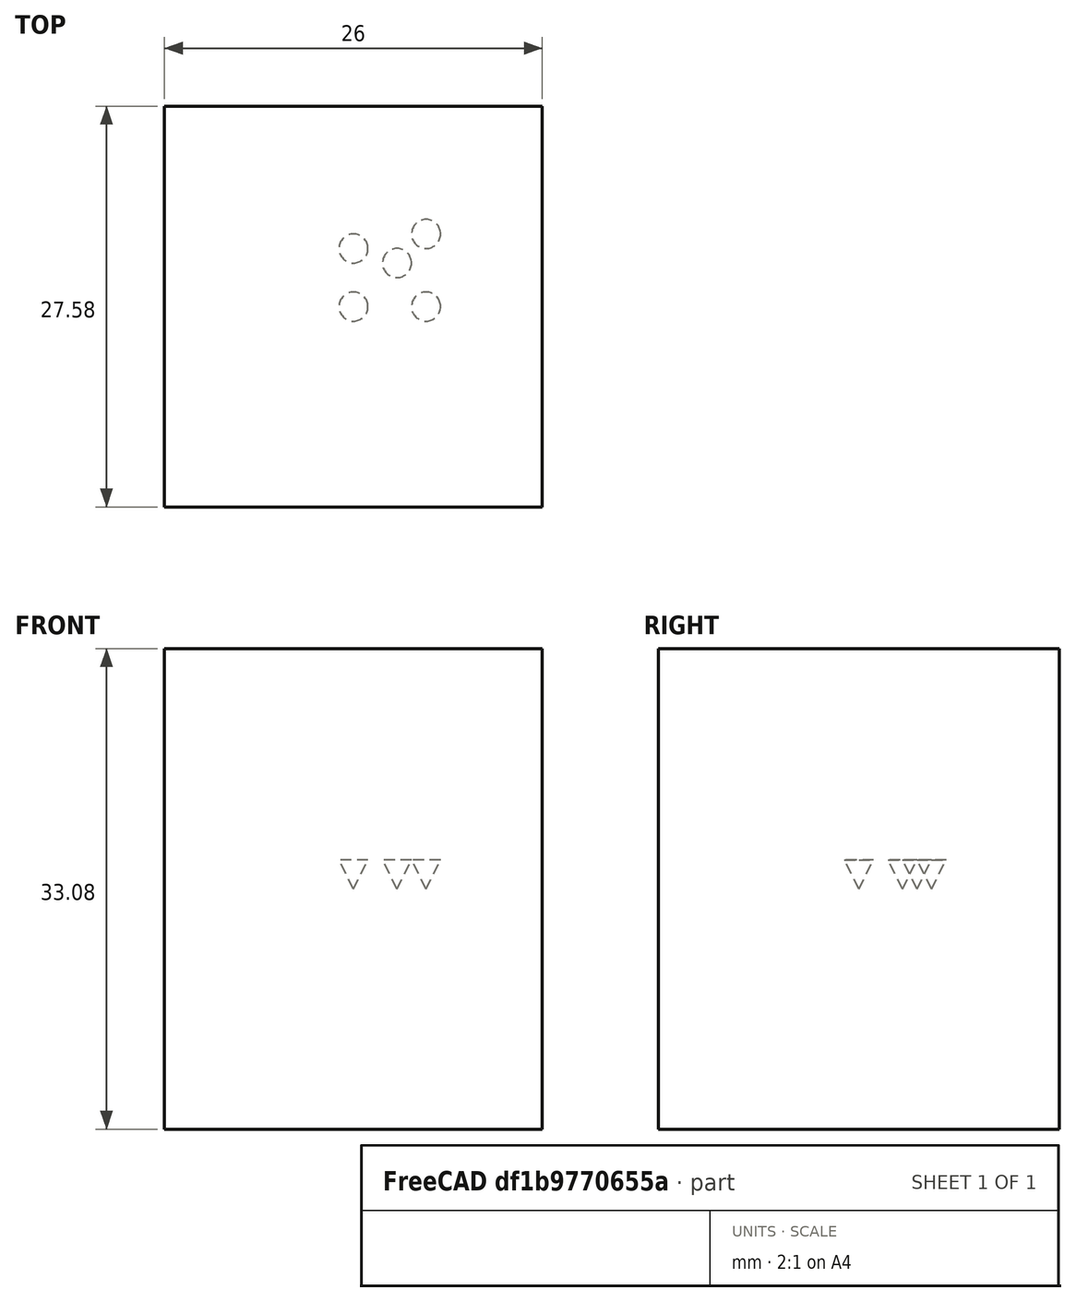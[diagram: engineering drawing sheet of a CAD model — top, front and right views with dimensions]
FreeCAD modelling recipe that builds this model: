
FCSTD DOCUMENT  (FreeCAD 0.21R33694 (Git))
Label: PointArray
License: All rights reserved
objects: App::DocumentObjectGroupPython×1251, Part::Vertex×5, Part::FeaturePython×2, App::Part×2, Part::Cone×1, Part::Compound×1
note: 9 computed .brp shape members not serialized (recipe doc carries the construction recipe); baked Part::Feature solids carry a one-line shape summary decoded from their .brp

FEATURE [App::DocumentObjectGroupPython] HALFPI  # scripted group (container) (typed FeaturePython)
  name = HALFPI
  value = pi/2.
FEATURE [App::DocumentObjectGroupPython] PI  # scripted group (container) (typed FeaturePython)
  name = PI
  value = 1.*pi
FEATURE [App::DocumentObjectGroupPython] TWOPI  # scripted group (container) (typed FeaturePython)
  name = TWOPI
  value = 2.*pi
FEATURE [App::DocumentObjectGroupPython] Constants  # scripted group (container) (typed FeaturePython)
  Group = -> [HALFPI,PI,TWOPI]
FEATURE [App::DocumentObjectGroupPython] Variables  # scripted group (container) (typed FeaturePython)
FEATURE [App::DocumentObjectGroupPython] Quantities  # scripted group (container) (typed FeaturePython)
FEATURE [App::DocumentObjectGroupPython] Isotopes  # scripted group (container) (typed FeaturePython)
FEATURE [App::DocumentObjectGroupPython] Elements  # scripted group (container) (typed FeaturePython)
FEATURE [App::DocumentObjectGroupPython] Matrix  # scripted group (container) (typed FeaturePython)
FEATURE [App::DocumentObjectGroupPython] Surfaces  # scripted group (container) (typed FeaturePython)
FEATURE [App::DocumentObjectGroupPython] Opticals  # scripted group (container) (typed FeaturePython)
  Group = -> [Matrix,Surfaces]
FEATURE [App::DocumentObjectGroupPython] G4Isotopes  # scripted group (container) (typed FeaturePython)
FEATURE [App::DocumentObjectGroupPython] H_element  # scripted group (container) (typed FeaturePython)
  Z = 1
  atom_value = 1.008
  formula = H
  name = H_element
FEATURE [App::DocumentObjectGroupPython] He_element  # scripted group (container) (typed FeaturePython)
  Z = 2
  atom_value = 4.0026
  formula = He
  name = He_element
FEATURE [App::DocumentObjectGroupPython] Li_element  # scripted group (container) (typed FeaturePython)
  Z = 3
  atom_value = 6.94
  formula = Li
  name = Li_element
FEATURE [App::DocumentObjectGroupPython] Be_element  # scripted group (container) (typed FeaturePython)
  Z = 4
  atom_value = 9.01218
  formula = Be
  name = Be_element
FEATURE [App::DocumentObjectGroupPython] B_element  # scripted group (container) (typed FeaturePython)
  Z = 5
  atom_value = 10.81
  formula = B
  name = B_element
FEATURE [App::DocumentObjectGroupPython] C_element  # scripted group (container) (typed FeaturePython)
  Z = 6
  atom_value = 12.011
  formula = C
  name = C_element
FEATURE [App::DocumentObjectGroupPython] N_element  # scripted group (container) (typed FeaturePython)
  Z = 7
  atom_value = 14.007
  formula = N
  name = N_element
FEATURE [App::DocumentObjectGroupPython] O_element  # scripted group (container) (typed FeaturePython)
  Z = 8
  atom_value = 15.999
  formula = O
  name = O_element
FEATURE [App::DocumentObjectGroupPython] F_element  # scripted group (container) (typed FeaturePython)
  Z = 9
  atom_value = 18.9984
  formula = F
  name = F_element
FEATURE [App::DocumentObjectGroupPython] Ne_element  # scripted group (container) (typed FeaturePython)
  Z = 10
  atom_value = 20.1797
  formula = Ne
  name = Ne_element
FEATURE [App::DocumentObjectGroupPython] Na_element  # scripted group (container) (typed FeaturePython)
  Z = 11
  atom_value = 22.9898
  formula = Na
  name = Na_element
FEATURE [App::DocumentObjectGroupPython] Mg_element  # scripted group (container) (typed FeaturePython)
  Z = 12
  atom_value = 24.305
  formula = Mg
  name = Mg_element
FEATURE [App::DocumentObjectGroupPython] Al_element  # scripted group (container) (typed FeaturePython)
  Z = 13
  atom_value = 26.9815
  formula = Al
  name = Al_element
FEATURE [App::DocumentObjectGroupPython] Si_element  # scripted group (container) (typed FeaturePython)
  Z = 14
  atom_value = 28.085
  formula = Si
  name = Si_element
FEATURE [App::DocumentObjectGroupPython] P_element  # scripted group (container) (typed FeaturePython)
  Z = 15
  atom_value = 30.9738
  formula = P
  name = P_element
FEATURE [App::DocumentObjectGroupPython] S_element  # scripted group (container) (typed FeaturePython)
  Z = 16
  atom_value = 32.06
  formula = S
  name = S_element
FEATURE [App::DocumentObjectGroupPython] Cl_element  # scripted group (container) (typed FeaturePython)
  Z = 17
  atom_value = 35.45
  formula = Cl
  name = Cl_element
FEATURE [App::DocumentObjectGroupPython] Ar_element  # scripted group (container) (typed FeaturePython)
  Z = 18
  atom_value = 39.95
  formula = Ar
  name = Ar_element
FEATURE [App::DocumentObjectGroupPython] K_element  # scripted group (container) (typed FeaturePython)
  Z = 19
  atom_value = 39.0983
  formula = K
  name = K_element
FEATURE [App::DocumentObjectGroupPython] Ca_element  # scripted group (container) (typed FeaturePython)
  Z = 20
  atom_value = 40.078
  formula = Ca
  name = Ca_element
FEATURE [App::DocumentObjectGroupPython] Sc_element  # scripted group (container) (typed FeaturePython)
  Z = 21
  atom_value = 44.9559
  formula = Sc
  name = Sc_element
FEATURE [App::DocumentObjectGroupPython] Ti_element  # scripted group (container) (typed FeaturePython)
  Z = 22
  atom_value = 47.867
  formula = Ti
  name = Ti_element
FEATURE [App::DocumentObjectGroupPython] V_element  # scripted group (container) (typed FeaturePython)
  Z = 23
  atom_value = 50.9415
  formula = V
  name = V_element
FEATURE [App::DocumentObjectGroupPython] Cr_element  # scripted group (container) (typed FeaturePython)
  Z = 24
  atom_value = 51.9961
  formula = Cr
  name = Cr_element
FEATURE [App::DocumentObjectGroupPython] Mn_element  # scripted group (container) (typed FeaturePython)
  Z = 25
  atom_value = 54.938
  formula = Mn
  name = Mn_element
FEATURE [App::DocumentObjectGroupPython] Fe_element  # scripted group (container) (typed FeaturePython)
  Z = 26
  atom_value = 55.845
  formula = Fe
  name = Fe_element
FEATURE [App::DocumentObjectGroupPython] Co_element  # scripted group (container) (typed FeaturePython)
  Z = 27
  atom_value = 58.9332
  formula = Co
  name = Co_element
FEATURE [App::DocumentObjectGroupPython] Ni_element  # scripted group (container) (typed FeaturePython)
  Z = 28
  atom_value = 58.6934
  formula = Ni
  name = Ni_element
FEATURE [App::DocumentObjectGroupPython] Cu_element  # scripted group (container) (typed FeaturePython)
  Z = 29
  atom_value = 63.546
  formula = Cu
  name = Cu_element
FEATURE [App::DocumentObjectGroupPython] Zn_element  # scripted group (container) (typed FeaturePython)
  Z = 30
  atom_value = 65.38
  formula = Zn
  name = Zn_element
FEATURE [App::DocumentObjectGroupPython] Ga_element  # scripted group (container) (typed FeaturePython)
  Z = 31
  atom_value = 69.723
  formula = Ga
  name = Ga_element
FEATURE [App::DocumentObjectGroupPython] Ge_element  # scripted group (container) (typed FeaturePython)
  Z = 32
  atom_value = 72.63
  formula = Ge
  name = Ge_element
FEATURE [App::DocumentObjectGroupPython] As_element  # scripted group (container) (typed FeaturePython)
  Z = 33
  atom_value = 74.9216
  formula = As
  name = As_element
FEATURE [App::DocumentObjectGroupPython] Se_element  # scripted group (container) (typed FeaturePython)
  Z = 34
  atom_value = 78.971
  formula = Se
  name = Se_element
FEATURE [App::DocumentObjectGroupPython] Br_element  # scripted group (container) (typed FeaturePython)
  Z = 35
  atom_value = 79.904
  formula = Br
  name = Br_element
FEATURE [App::DocumentObjectGroupPython] Kr_element  # scripted group (container) (typed FeaturePython)
  Z = 36
  atom_value = 83.798
  formula = Kr
  name = Kr_element
FEATURE [App::DocumentObjectGroupPython] Rb_element  # scripted group (container) (typed FeaturePython)
  Z = 37
  atom_value = 85.4678
  formula = Rb
  name = Rb_element
FEATURE [App::DocumentObjectGroupPython] Sr_element  # scripted group (container) (typed FeaturePython)
  Z = 38
  atom_value = 87.62
  formula = Sr
  name = Sr_element
FEATURE [App::DocumentObjectGroupPython] Y_element  # scripted group (container) (typed FeaturePython)
  Z = 39
  atom_value = 88.9058
  formula = Y
  name = Y_element
FEATURE [App::DocumentObjectGroupPython] Zr_element  # scripted group (container) (typed FeaturePython)
  Z = 40
  atom_value = 91.224
  formula = Zr
  name = Zr_element
FEATURE [App::DocumentObjectGroupPython] Nb_element  # scripted group (container) (typed FeaturePython)
  Z = 41
  atom_value = 92.9064
  formula = Nb
  name = Nb_element
FEATURE [App::DocumentObjectGroupPython] Mo_element  # scripted group (container) (typed FeaturePython)
  Z = 42
  atom_value = 95.95
  formula = Mo
  name = Mo_element
FEATURE [App::DocumentObjectGroupPython] Tc_element  # scripted group (container) (typed FeaturePython)
  Z = 43
  atom_value = 97
  formula = Tc
  name = Tc_element
FEATURE [App::DocumentObjectGroupPython] Ru_element  # scripted group (container) (typed FeaturePython)
  Z = 44
  atom_value = 101.07
  formula = Ru
  name = Ru_element
FEATURE [App::DocumentObjectGroupPython] Rh_element  # scripted group (container) (typed FeaturePython)
  Z = 45
  atom_value = 102.905
  formula = Rh
  name = Rh_element
FEATURE [App::DocumentObjectGroupPython] Pd_element  # scripted group (container) (typed FeaturePython)
  Z = 46
  atom_value = 106.42
  formula = Pd
  name = Pd_element
FEATURE [App::DocumentObjectGroupPython] Ag_element  # scripted group (container) (typed FeaturePython)
  Z = 47
  atom_value = 107.868
  formula = Ag
  name = Ag_element
FEATURE [App::DocumentObjectGroupPython] Cd_element  # scripted group (container) (typed FeaturePython)
  Z = 48
  atom_value = 112.414
  formula = Cd
  name = Cd_element
FEATURE [App::DocumentObjectGroupPython] In_element  # scripted group (container) (typed FeaturePython)
  Z = 49
  atom_value = 114.818
  formula = In
  name = In_element
FEATURE [App::DocumentObjectGroupPython] Sn_element  # scripted group (container) (typed FeaturePython)
  Z = 50
  atom_value = 118.71
  formula = Sn
  name = Sn_element
FEATURE [App::DocumentObjectGroupPython] Sb_element  # scripted group (container) (typed FeaturePython)
  Z = 51
  atom_value = 121.76
  formula = Sb
  name = Sb_element
FEATURE [App::DocumentObjectGroupPython] Te_element  # scripted group (container) (typed FeaturePython)
  Z = 52
  atom_value = 127.6
  formula = Te
  name = Te_element
FEATURE [App::DocumentObjectGroupPython] I_element  # scripted group (container) (typed FeaturePython)
  Z = 53
  atom_value = 126.904
  formula = I
  name = I_element
FEATURE [App::DocumentObjectGroupPython] Xe_element  # scripted group (container) (typed FeaturePython)
  Z = 54
  atom_value = 131.293
  formula = Xe
  name = Xe_element
FEATURE [App::DocumentObjectGroupPython] Cs_element  # scripted group (container) (typed FeaturePython)
  Z = 55
  atom_value = 132.905
  formula = Cs
  name = Cs_element
FEATURE [App::DocumentObjectGroupPython] Ba_element  # scripted group (container) (typed FeaturePython)
  Z = 56
  atom_value = 137.327
  formula = Ba
  name = Ba_element
FEATURE [App::DocumentObjectGroupPython] La_element  # scripted group (container) (typed FeaturePython)
  Z = 57
  atom_value = 138.905
  formula = La
  name = La_element
FEATURE [App::DocumentObjectGroupPython] Ce_element  # scripted group (container) (typed FeaturePython)
  Z = 58
  atom_value = 140.116
  formula = Ce
  name = Ce_element
FEATURE [App::DocumentObjectGroupPython] Pr_element  # scripted group (container) (typed FeaturePython)
  Z = 59
  atom_value = 140.908
  formula = Pr
  name = Pr_element
FEATURE [App::DocumentObjectGroupPython] Nd_element  # scripted group (container) (typed FeaturePython)
  Z = 60
  atom_value = 144.242
  formula = Nd
  name = Nd_element
FEATURE [App::DocumentObjectGroupPython] Pm_element  # scripted group (container) (typed FeaturePython)
  Z = 61
  atom_value = 145
  formula = Pm
  name = Pm_element
FEATURE [App::DocumentObjectGroupPython] Sm_element  # scripted group (container) (typed FeaturePython)
  Z = 62
  atom_value = 150.36
  formula = Sm
  name = Sm_element
FEATURE [App::DocumentObjectGroupPython] Eu_element  # scripted group (container) (typed FeaturePython)
  Z = 63
  atom_value = 151.964
  formula = Eu
  name = Eu_element
FEATURE [App::DocumentObjectGroupPython] Gd_element  # scripted group (container) (typed FeaturePython)
  Z = 64
  atom_value = 157.25
  formula = Gd
  name = Gd_element
FEATURE [App::DocumentObjectGroupPython] Tb_element  # scripted group (container) (typed FeaturePython)
  Z = 65
  atom_value = 158.925
  formula = Tb
  name = Tb_element
FEATURE [App::DocumentObjectGroupPython] Dy_element  # scripted group (container) (typed FeaturePython)
  Z = 66
  atom_value = 162.5
  formula = Dy
  name = Dy_element
FEATURE [App::DocumentObjectGroupPython] Ho_element  # scripted group (container) (typed FeaturePython)
  Z = 67
  atom_value = 164.93
  formula = Ho
  name = Ho_element
FEATURE [App::DocumentObjectGroupPython] Er_element  # scripted group (container) (typed FeaturePython)
  Z = 68
  atom_value = 167.259
  formula = Er
  name = Er_element
FEATURE [App::DocumentObjectGroupPython] Tm_element  # scripted group (container) (typed FeaturePython)
  Z = 69
  atom_value = 168.934
  formula = Tm
  name = Tm_element
FEATURE [App::DocumentObjectGroupPython] Yb_element  # scripted group (container) (typed FeaturePython)
  Z = 70
  atom_value = 173.045
  formula = Yb
  name = Yb_element
FEATURE [App::DocumentObjectGroupPython] Lu_element  # scripted group (container) (typed FeaturePython)
  Z = 71
  atom_value = 174.967
  formula = Lu
  name = Lu_element
FEATURE [App::DocumentObjectGroupPython] Hf_element  # scripted group (container) (typed FeaturePython)
  Z = 72
  atom_value = 178.49
  formula = Hf
  name = Hf_element
FEATURE [App::DocumentObjectGroupPython] Ta_element  # scripted group (container) (typed FeaturePython)
  Z = 73
  atom_value = 180.948
  formula = Ta
  name = Ta_element
FEATURE [App::DocumentObjectGroupPython] W_element  # scripted group (container) (typed FeaturePython)
  Z = 74
  atom_value = 183.84
  formula = W
  name = W_element
FEATURE [App::DocumentObjectGroupPython] Re_element  # scripted group (container) (typed FeaturePython)
  Z = 75
  atom_value = 186.207
  formula = Re
  name = Re_element
FEATURE [App::DocumentObjectGroupPython] Os_element  # scripted group (container) (typed FeaturePython)
  Z = 76
  atom_value = 190.23
  formula = Os
  name = Os_element
FEATURE [App::DocumentObjectGroupPython] Ir_element  # scripted group (container) (typed FeaturePython)
  Z = 77
  atom_value = 192.217
  formula = Ir
  name = Ir_element
FEATURE [App::DocumentObjectGroupPython] Pt_element  # scripted group (container) (typed FeaturePython)
  Z = 78
  atom_value = 195.084
  formula = Pt
  name = Pt_element
FEATURE [App::DocumentObjectGroupPython] Au_element  # scripted group (container) (typed FeaturePython)
  Z = 79
  atom_value = 196.967
  formula = Au
  name = Au_element
FEATURE [App::DocumentObjectGroupPython] Hg_element  # scripted group (container) (typed FeaturePython)
  Z = 80
  atom_value = 200.592
  formula = Hg
  name = Hg_element
FEATURE [App::DocumentObjectGroupPython] Tl_element  # scripted group (container) (typed FeaturePython)
  Z = 81
  atom_value = 204.38
  formula = Tl
  name = Tl_element
FEATURE [App::DocumentObjectGroupPython] Pb_element  # scripted group (container) (typed FeaturePython)
  Z = 82
  atom_value = 207.2
  formula = Pb
  name = Pb_element
FEATURE [App::DocumentObjectGroupPython] Bi_element  # scripted group (container) (typed FeaturePython)
  Z = 83
  atom_value = 208.98
  formula = Bi
  name = Bi_element
FEATURE [App::DocumentObjectGroupPython] Po_element  # scripted group (container) (typed FeaturePython)
  Z = 84
  atom_value = 209
  formula = Po
  name = Po_element
FEATURE [App::DocumentObjectGroupPython] At_element  # scripted group (container) (typed FeaturePython)
  Z = 85
  atom_value = 210
  formula = At
  name = At_element
FEATURE [App::DocumentObjectGroupPython] Rn_element  # scripted group (container) (typed FeaturePython)
  Z = 86
  atom_value = 222
  formula = Rn
  name = Rn_element
FEATURE [App::DocumentObjectGroupPython] Fr_element  # scripted group (container) (typed FeaturePython)
  Z = 87
  atom_value = 223
  formula = Fr
  name = Fr_element
FEATURE [App::DocumentObjectGroupPython] Ra_element  # scripted group (container) (typed FeaturePython)
  Z = 88
  atom_value = 226
  formula = Ra
  name = Ra_element
FEATURE [App::DocumentObjectGroupPython] Ac_element  # scripted group (container) (typed FeaturePython)
  Z = 89
  atom_value = 227
  formula = Ac
  name = Ac_element
FEATURE [App::DocumentObjectGroupPython] Th_element  # scripted group (container) (typed FeaturePython)
  Z = 90
  atom_value = 232.038
  formula = Th
  name = Th_element
FEATURE [App::DocumentObjectGroupPython] Pa_element  # scripted group (container) (typed FeaturePython)
  Z = 91
  atom_value = 231.036
  formula = Pa
  name = Pa_element
FEATURE [App::DocumentObjectGroupPython] U_element  # scripted group (container) (typed FeaturePython)
  Z = 92
  atom_value = 238.029
  formula = U
  name = U_element
FEATURE [App::DocumentObjectGroupPython] Np_element  # scripted group (container) (typed FeaturePython)
  Z = 93
  atom_value = 237
  formula = Np
  name = Np_element
FEATURE [App::DocumentObjectGroupPython] Pu_element  # scripted group (container) (typed FeaturePython)
  Z = 94
  atom_value = 244
  formula = Pu
  name = Pu_element
FEATURE [App::DocumentObjectGroupPython] Am_element  # scripted group (container) (typed FeaturePython)
  Z = 95
  atom_value = 243
  formula = Am
  name = Am_element
FEATURE [App::DocumentObjectGroupPython] Cm_element  # scripted group (container) (typed FeaturePython)
  Z = 96
  atom_value = 247
  formula = Cm
  name = Cm_element
FEATURE [App::DocumentObjectGroupPython] Bk_element  # scripted group (container) (typed FeaturePython)
  Z = 97
  atom_value = 247
  formula = Bk
  name = Bk_element
FEATURE [App::DocumentObjectGroupPython] Cf_element  # scripted group (container) (typed FeaturePython)
  Z = 98
  atom_value = 251
  formula = Cf
  name = Cf_element
FEATURE [App::DocumentObjectGroupPython] G4Elements  # scripted group (container) (typed FeaturePython)
  Group = -> [H_element,He_element,Li_element,Be_element,B_element,C_element,N_element,O_element,F_element,Ne_element,Na_element,Mg_element,Al_element,Si_element,P_element,S_element,Cl_element,Ar_element,K_element,Ca_element,Sc_element,Ti_element,V_element,Cr_element,Mn_element,Fe_element,Co_element,Ni_element,Cu_element,Zn_element,Ga_element,Ge_element,As_element,Se_element,Br_element,Kr_element,Rb_element,+61 more]
FEATURE [App::DocumentObjectGroupPython] H_element001  label="H_element : 0.101"  # scripted group (container) (typed FeaturePython)
  n = 0.101327
FEATURE [App::DocumentObjectGroupPython] C_element001  label="C_element : 0.775"  # scripted group (container) (typed FeaturePython)
  n = 0.7755
FEATURE [App::DocumentObjectGroupPython] N_element001  label="N_element : 0.035"  # scripted group (container) (typed FeaturePython)
  n = 0.035057
FEATURE [App::DocumentObjectGroupPython] O_element001  label="O_element : 0.052"  # scripted group (container) (typed FeaturePython)
  n = 0.0523159
FEATURE [App::DocumentObjectGroupPython] F_element001  label="F_element : 0.017"  # scripted group (container) (typed FeaturePython)
  n = 0.017422
FEATURE [App::DocumentObjectGroupPython] Ca_element001  label="Ca_element : 0.018"  # scripted group (container) (typed FeaturePython)
  n = 0.018378
FEATURE [App::DocumentObjectGroupPython] G4_A_150_TISSUE  label="G4_A-150_TISSUE"  # scripted group (container) (typed FeaturePython)
  Dunit = g/cm3
  Dvalue = 1.127
  Group = -> [H_element001,C_element001,N_element001,O_element001,F_element001,Ca_element001]
  conduct = 2
  density = 1
  expand = 3
  formula = G4_A-150_TISSUE
  name = G4_A-150_TISSUE
  specific = 4
FEATURE [App::DocumentObjectGroupPython] C_element002  label="C_element : 3"  # scripted group (container) (typed FeaturePython)
  n = 3
  ref = C_element
FEATURE [App::DocumentObjectGroupPython] H_element002  label="H_element : 6"  # scripted group (container) (typed FeaturePython)
  n = 6
  ref = H_element
FEATURE [App::DocumentObjectGroupPython] O_element002  label="O_element : 1"  # scripted group (container) (typed FeaturePython)
  n = 1
  ref = O_element
FEATURE [App::DocumentObjectGroupPython] G4_ACETONE  # scripted group (container) (typed FeaturePython)
  Dunit = g/cm3
  Dvalue = 0.7899
  Group = -> [C_element002,H_element002,O_element002]
  conduct = 2
  density = 1
  expand = 3
  formula = G4_ACETONE
  name = G4_ACETONE
  specific = 4
FEATURE [App::DocumentObjectGroupPython] C_element003  label="C_element : 2"  # scripted group (container) (typed FeaturePython)
  n = 2
  ref = C_element
FEATURE [App::DocumentObjectGroupPython] H_element003  label="H_element : 2"  # scripted group (container) (typed FeaturePython)
  n = 2
  ref = H_element
FEATURE [App::DocumentObjectGroupPython] G4_ACETYLENE  # scripted group (container) (typed FeaturePython)
  Dunit = g/cm3
  Dvalue = 0.0010967
  Group = -> [C_element003,H_element003]
  conduct = 2
  density = 1
  expand = 3
  formula = G4_ACETYLENE
  name = G4_ACETYLENE
  specific = 4
FEATURE [App::DocumentObjectGroupPython] C_element004  label="C_element : 5"  # scripted group (container) (typed FeaturePython)
  n = 5
  ref = C_element
FEATURE [App::DocumentObjectGroupPython] H_element004  label="H_element : 5"  # scripted group (container) (typed FeaturePython)
  n = 5
  ref = H_element
FEATURE [App::DocumentObjectGroupPython] N_element002  label="N_element : 5"  # scripted group (container) (typed FeaturePython)
  n = 5
  ref = N_element
FEATURE [App::DocumentObjectGroupPython] G4_ADENINE  # scripted group (container) (typed FeaturePython)
  Dunit = g/cm3
  Dvalue = 1.6
  Group = -> [C_element004,H_element004,N_element002]
  conduct = 2
  density = 1
  expand = 3
  formula = G4_ADENINE
  name = G4_ADENINE
  specific = 4
FEATURE [App::DocumentObjectGroupPython] H_element005  label="H_element : 0.114"  # scripted group (container) (typed FeaturePython)
  n = 0.114
FEATURE [App::DocumentObjectGroupPython] C_element005  label="C_element : 0.598"  # scripted group (container) (typed FeaturePython)
  n = 0.598
FEATURE [App::DocumentObjectGroupPython] N_element003  label="N_element : 0.007"  # scripted group (container) (typed FeaturePython)
  n = 0.007
FEATURE [App::DocumentObjectGroupPython] O_element003  label="O_element : 0.278"  # scripted group (container) (typed FeaturePython)
  n = 0.278
FEATURE [App::DocumentObjectGroupPython] Na_element001  label="Na_element : 0.001"  # scripted group (container) (typed FeaturePython)
  n = 0.001
FEATURE [App::DocumentObjectGroupPython] S_element001  label="S_element : 0.001"  # scripted group (container) (typed FeaturePython)
  n = 0.001
FEATURE [App::DocumentObjectGroupPython] Cl_element001  label="Cl_element : 0.001"  # scripted group (container) (typed FeaturePython)
  n = 0.001
FEATURE [App::DocumentObjectGroupPython] G4_ADIPOSE_TISSUE_ICRP  # scripted group (container) (typed FeaturePython)
  Dunit = g/cm3
  Dvalue = 0.95
  Group = -> [H_element005,C_element005,N_element003,O_element003,Na_element001,S_element001,Cl_element001]
  conduct = 2
  density = 1
  expand = 3
  formula = G4_ADIPOSE_TISSUE_ICRP
  name = G4_ADIPOSE_TISSUE_ICRP
  specific = 4
FEATURE [App::DocumentObjectGroupPython] C_element006  label="C_element : 0.000"  # scripted group (container) (typed FeaturePython)
  n = 0.000124
FEATURE [App::DocumentObjectGroupPython] N_element004  label="N_element : 0.755"  # scripted group (container) (typed FeaturePython)
  n = 0.755268
FEATURE [App::DocumentObjectGroupPython] O_element004  label="O_element : 0.232"  # scripted group (container) (typed FeaturePython)
  n = 0.231781
FEATURE [App::DocumentObjectGroupPython] Ar_element001  label="Ar_element : 0.013"  # scripted group (container) (typed FeaturePython)
  n = 0.012827
FEATURE [App::DocumentObjectGroupPython] G4_AIR  # scripted group (container) (typed FeaturePython)
  Dunit = g/cm3
  Dvalue = 0.00120479
  Group = -> [C_element006,N_element004,O_element004,Ar_element001]
  conduct = 2
  density = 1
  expand = 3
  formula = G4_AIR
  name = G4_AIR
  specific = 4
FEATURE [App::DocumentObjectGroupPython] C_element007  label="C_element : 006"  # scripted group (container) (typed FeaturePython)
  n = 3
  ref = C_element
FEATURE [App::DocumentObjectGroupPython] H_element006  label="H_element : 7"  # scripted group (container) (typed FeaturePython)
  n = 7
  ref = H_element
FEATURE [App::DocumentObjectGroupPython] N_element005  label="N_element : 1"  # scripted group (container) (typed FeaturePython)
  n = 1
  ref = N_element
FEATURE [App::DocumentObjectGroupPython] O_element005  label="O_element : 2"  # scripted group (container) (typed FeaturePython)
  n = 2
  ref = O_element
FEATURE [App::DocumentObjectGroupPython] G4_ALANINE  # scripted group (container) (typed FeaturePython)
  Dunit = g/cm3
  Dvalue = 1.42
  Group = -> [C_element007,H_element006,N_element005,O_element005]
  conduct = 2
  density = 1
  expand = 3
  formula = G4_ALANINE
  name = G4_ALANINE
  specific = 4
FEATURE [App::DocumentObjectGroupPython] Al_element001  label="Al_element : 2"  # scripted group (container) (typed FeaturePython)
  n = 2
  ref = Al_element
FEATURE [App::DocumentObjectGroupPython] O_element006  label="O_element : 3"  # scripted group (container) (typed FeaturePython)
  n = 3
  ref = O_element
FEATURE [App::DocumentObjectGroupPython] G4_ALUMINUM_OXIDE  # scripted group (container) (typed FeaturePython)
  Dunit = g/cm3
  Dvalue = 3.97
  Group = -> [Al_element001,O_element006]
  conduct = 2
  density = 1
  expand = 3
  formula = G4_ALUMINUM_OXIDE
  name = G4_ALUMINUM_OXIDE
  specific = 4
FEATURE [App::DocumentObjectGroupPython] H_element007  label="H_element : 0.106"  # scripted group (container) (typed FeaturePython)
  n = 0.10593
FEATURE [App::DocumentObjectGroupPython] C_element008  label="C_element : 0.789"  # scripted group (container) (typed FeaturePython)
  n = 0.788974
FEATURE [App::DocumentObjectGroupPython] O_element007  label="O_element : 0.105"  # scripted group (container) (typed FeaturePython)
  n = 0.105096
FEATURE [App::DocumentObjectGroupPython] G4_AMBER  # scripted group (container) (typed FeaturePython)
  Dunit = g/cm3
  Dvalue = 1.1
  Group = -> [H_element007,C_element008,O_element007]
  conduct = 2
  density = 1
  expand = 3
  formula = G4_AMBER
  name = G4_AMBER
  specific = 4
FEATURE [App::DocumentObjectGroupPython] N_element006  label="N_element : 006"  # scripted group (container) (typed FeaturePython)
  n = 1
  ref = N_element
FEATURE [App::DocumentObjectGroupPython] H_element008  label="H_element : 3"  # scripted group (container) (typed FeaturePython)
  n = 3
  ref = H_element
FEATURE [App::DocumentObjectGroupPython] G4_AMMONIA  # scripted group (container) (typed FeaturePython)
  Dunit = g/cm3
  Dvalue = 0.000826019
  Group = -> [N_element006,H_element008]
  conduct = 2
  density = 1
  expand = 3
  formula = G4_AMMONIA
  name = G4_AMMONIA
  specific = 4
FEATURE [App::DocumentObjectGroupPython] C_element009  label="C_element : 6"  # scripted group (container) (typed FeaturePython)
  n = 6
  ref = C_element
FEATURE [App::DocumentObjectGroupPython] H_element009  label="H_element : 008"  # scripted group (container) (typed FeaturePython)
  n = 7
  ref = H_element
FEATURE [App::DocumentObjectGroupPython] N_element007  label="N_element : 007"  # scripted group (container) (typed FeaturePython)
  n = 1
  ref = N_element
FEATURE [App::DocumentObjectGroupPython] G4_ANILINE  # scripted group (container) (typed FeaturePython)
  Dunit = g/cm3
  Dvalue = 1.0235
  Group = -> [C_element009,H_element009,N_element007]
  conduct = 2
  density = 1
  expand = 3
  formula = G4_ANILINE
  name = G4_ANILINE
  specific = 4
FEATURE [App::DocumentObjectGroupPython] C_element010  label="C_element : 14"  # scripted group (container) (typed FeaturePython)
  n = 14
  ref = C_element
FEATURE [App::DocumentObjectGroupPython] H_element010  label="H_element : 10"  # scripted group (container) (typed FeaturePython)
  n = 10
  ref = H_element
FEATURE [App::DocumentObjectGroupPython] G4_ANTHRACENE  # scripted group (container) (typed FeaturePython)
  Dunit = g/cm3
  Dvalue = 1.283
  Group = -> [C_element010,H_element010]
  conduct = 2
  density = 1
  expand = 3
  formula = G4_ANTHRACENE
  name = G4_ANTHRACENE
  specific = 4
FEATURE [App::DocumentObjectGroupPython] H_element011  label="H_element : 0.065"  # scripted group (container) (typed FeaturePython)
  n = 0.0654709
FEATURE [App::DocumentObjectGroupPython] C_element011  label="C_element : 0.537"  # scripted group (container) (typed FeaturePython)
  n = 0.536944
FEATURE [App::DocumentObjectGroupPython] N_element008  label="N_element : 0.021"  # scripted group (container) (typed FeaturePython)
  n = 0.0215
FEATURE [App::DocumentObjectGroupPython] O_element008  label="O_element : 0.032"  # scripted group (container) (typed FeaturePython)
  n = 0.032085
FEATURE [App::DocumentObjectGroupPython] F_element002  label="F_element : 0.167"  # scripted group (container) (typed FeaturePython)
  n = 0.167411
FEATURE [App::DocumentObjectGroupPython] Ca_element002  label="Ca_element : 0.177"  # scripted group (container) (typed FeaturePython)
  n = 0.176589
FEATURE [App::DocumentObjectGroupPython] G4_B_100_BONE  label="G4_B-100_BONE"  # scripted group (container) (typed FeaturePython)
  Dunit = g/cm3
  Dvalue = 1.45
  Group = -> [H_element011,C_element011,N_element008,O_element008,F_element002,Ca_element002]
  conduct = 2
  density = 1
  expand = 3
  formula = G4_B-100_BONE
  name = G4_B-100_BONE
  specific = 4
FEATURE [App::DocumentObjectGroupPython] H_element012  label="H_element : 0.057"  # scripted group (container) (typed FeaturePython)
  n = 0.057441
FEATURE [App::DocumentObjectGroupPython] C_element012  label="C_element : 0.790"  # scripted group (container) (typed FeaturePython)
  n = 0.774591
FEATURE [App::DocumentObjectGroupPython] O_element009  label="O_element : 0.168"  # scripted group (container) (typed FeaturePython)
  n = 0.167968
FEATURE [App::DocumentObjectGroupPython] G4_BAKELITE  # scripted group (container) (typed FeaturePython)
  Dunit = g/cm3
  Dvalue = 1.25
  Group = -> [H_element012,C_element012,O_element009]
  conduct = 2
  density = 1
  expand = 3
  formula = G4_BAKELITE
  name = G4_BAKELITE
  specific = 4
FEATURE [App::DocumentObjectGroupPython] Ba_element001  label="Ba_element : 1"  # scripted group (container) (typed FeaturePython)
  n = 1
  ref = Ba_element
FEATURE [App::DocumentObjectGroupPython] F_element003  label="F_element : 2"  # scripted group (container) (typed FeaturePython)
  n = 2
  ref = F_element
FEATURE [App::DocumentObjectGroupPython] G4_BARIUM_FLUORIDE  # scripted group (container) (typed FeaturePython)
  Dunit = g/cm3
  Dvalue = 4.89
  Group = -> [Ba_element001,F_element003]
  conduct = 2
  density = 1
  expand = 3
  formula = G4_BARIUM_FLUORIDE
  name = G4_BARIUM_FLUORIDE
  specific = 4
FEATURE [App::DocumentObjectGroupPython] Ba_element002  label="Ba_element : 002"  # scripted group (container) (typed FeaturePython)
  n = 1
  ref = Ba_element
FEATURE [App::DocumentObjectGroupPython] S_element002  label="S_element : 1"  # scripted group (container) (typed FeaturePython)
  n = 1
  ref = S_element
FEATURE [App::DocumentObjectGroupPython] O_element010  label="O_element : 4"  # scripted group (container) (typed FeaturePython)
  n = 4
  ref = O_element
FEATURE [App::DocumentObjectGroupPython] G4_BARIUM_SULFATE  # scripted group (container) (typed FeaturePython)
  Dunit = g/cm3
  Dvalue = 4.5
  Group = -> [Ba_element002,S_element002,O_element010]
  conduct = 2
  density = 1
  expand = 3
  formula = G4_BARIUM_SULFATE
  name = G4_BARIUM_SULFATE
  specific = 4
FEATURE [App::DocumentObjectGroupPython] C_element013  label="C_element : 007"  # scripted group (container) (typed FeaturePython)
  n = 6
  ref = C_element
FEATURE [App::DocumentObjectGroupPython] H_element013  label="H_element : 009"  # scripted group (container) (typed FeaturePython)
  n = 6
  ref = H_element
FEATURE [App::DocumentObjectGroupPython] G4_BENZENE  # scripted group (container) (typed FeaturePython)
  Dunit = g/cm3
  Dvalue = 0.87865
  Group = -> [C_element013,H_element013]
  conduct = 2
  density = 1
  expand = 3
  formula = G4_BENZENE
  name = G4_BENZENE
  specific = 4
FEATURE [App::DocumentObjectGroupPython] Be_element001  label="Be_element : 1"  # scripted group (container) (typed FeaturePython)
  n = 1
  ref = Be_element
FEATURE [App::DocumentObjectGroupPython] O_element011  label="O_element : 005"  # scripted group (container) (typed FeaturePython)
  n = 1
  ref = O_element
FEATURE [App::DocumentObjectGroupPython] G4_BERYLLIUM_OXIDE  # scripted group (container) (typed FeaturePython)
  Dunit = g/cm3
  Dvalue = 3.01
  Group = -> [Be_element001,O_element011]
  conduct = 2
  density = 1
  expand = 3
  formula = G4_BERYLLIUM_OXIDE
  name = G4_BERYLLIUM_OXIDE
  specific = 4
FEATURE [App::DocumentObjectGroupPython] Bi_element001  label="Bi_element : 4"  # scripted group (container) (typed FeaturePython)
  n = 4
  ref = Bi_element
FEATURE [App::DocumentObjectGroupPython] Ge_element001  label="Ge_element : 3"  # scripted group (container) (typed FeaturePython)
  n = 3
  ref = Ge_element
FEATURE [App::DocumentObjectGroupPython] O_element012  label="O_element : 12"  # scripted group (container) (typed FeaturePython)
  n = 12
  ref = O_element
FEATURE [App::DocumentObjectGroupPython] G4_BGO  # scripted group (container) (typed FeaturePython)
  Dunit = g/cm3
  Dvalue = 7.13
  Group = -> [Bi_element001,Ge_element001,O_element012]
  conduct = 2
  density = 1
  expand = 3
  formula = G4_BGO
  name = G4_BGO
  specific = 4
FEATURE [App::DocumentObjectGroupPython] H_element014  label="H_element : 0.102"  # scripted group (container) (typed FeaturePython)
  n = 0.102
FEATURE [App::DocumentObjectGroupPython] C_element014  label="C_element : 0.110"  # scripted group (container) (typed FeaturePython)
  n = 0.11
FEATURE [App::DocumentObjectGroupPython] N_element009  label="N_element : 0.033"  # scripted group (container) (typed FeaturePython)
  n = 0.033
FEATURE [App::DocumentObjectGroupPython] O_element013  label="O_element : 0.745"  # scripted group (container) (typed FeaturePython)
  n = 0.745
FEATURE [App::DocumentObjectGroupPython] Na_element002  label="Na_element : 0.002"  # scripted group (container) (typed FeaturePython)
  n = 0.001
FEATURE [App::DocumentObjectGroupPython] P_element001  label="P_element : 0.001"  # scripted group (container) (typed FeaturePython)
  n = 0.001
FEATURE [App::DocumentObjectGroupPython] S_element003  label="S_element : 0.002"  # scripted group (container) (typed FeaturePython)
  n = 0.002
FEATURE [App::DocumentObjectGroupPython] Cl_element002  label="Cl_element : 0.003"  # scripted group (container) (typed FeaturePython)
  n = 0.003
FEATURE [App::DocumentObjectGroupPython] K_element001  label="K_element : 0.002"  # scripted group (container) (typed FeaturePython)
  n = 0.002
FEATURE [App::DocumentObjectGroupPython] Fe_element001  label="Fe_element : 0.001"  # scripted group (container) (typed FeaturePython)
  n = 0.001
FEATURE [App::DocumentObjectGroupPython] G4_BLOOD_ICRP  # scripted group (container) (typed FeaturePython)
  Dunit = g/cm3
  Dvalue = 1.06
  Group = -> [H_element014,C_element014,N_element009,O_element013,Na_element002,P_element001,S_element003,Cl_element002,K_element001,Fe_element001]
  conduct = 2
  density = 1
  expand = 3
  formula = G4_BLOOD_ICRP
  name = G4_BLOOD_ICRP
  specific = 4
FEATURE [App::DocumentObjectGroupPython] H_element015  label="H_element : 0.064"  # scripted group (container) (typed FeaturePython)
  n = 0.064
FEATURE [App::DocumentObjectGroupPython] C_element015  label="C_element : 0.278"  # scripted group (container) (typed FeaturePython)
  n = 0.278
FEATURE [App::DocumentObjectGroupPython] N_element010  label="N_element : 0.027"  # scripted group (container) (typed FeaturePython)
  n = 0.027
FEATURE [App::DocumentObjectGroupPython] O_element014  label="O_element : 0.410"  # scripted group (container) (typed FeaturePython)
  n = 0.41
FEATURE [App::DocumentObjectGroupPython] Mg_element001  label="Mg_element : 0.002"  # scripted group (container) (typed FeaturePython)
  n = 0.002
FEATURE [App::DocumentObjectGroupPython] P_element002  label="P_element : 0.070"  # scripted group (container) (typed FeaturePython)
  n = 0.07
FEATURE [App::DocumentObjectGroupPython] S_element004  label="S_element : 0.003"  # scripted group (container) (typed FeaturePython)
  n = 0.002
FEATURE [App::DocumentObjectGroupPython] Ca_element003  label="Ca_element : 0.147"  # scripted group (container) (typed FeaturePython)
  n = 0.147
FEATURE [App::DocumentObjectGroupPython] G4_BONE_COMPACT_ICRU  # scripted group (container) (typed FeaturePython)
  Dunit = g/cm3
  Dvalue = 1.85
  Group = -> [H_element015,C_element015,N_element010,O_element014,Mg_element001,P_element002,S_element004,Ca_element003]
  conduct = 2
  density = 1
  expand = 3
  formula = G4_BONE_COMPACT_ICRU
  name = G4_BONE_COMPACT_ICRU
  specific = 4
FEATURE [App::DocumentObjectGroupPython] H_element016  label="H_element : 0.034"  # scripted group (container) (typed FeaturePython)
  n = 0.034
FEATURE [App::DocumentObjectGroupPython] C_element016  label="C_element : 0.155"  # scripted group (container) (typed FeaturePython)
  n = 0.155
FEATURE [App::DocumentObjectGroupPython] N_element011  label="N_element : 0.042"  # scripted group (container) (typed FeaturePython)
  n = 0.042
FEATURE [App::DocumentObjectGroupPython] O_element015  label="O_element : 0.435"  # scripted group (container) (typed FeaturePython)
  n = 0.435
FEATURE [App::DocumentObjectGroupPython] Na_element003  label="Na_element : 0.003"  # scripted group (container) (typed FeaturePython)
  n = 0.001
FEATURE [App::DocumentObjectGroupPython] Mg_element002  label="Mg_element : 0.003"  # scripted group (container) (typed FeaturePython)
  n = 0.002
FEATURE [App::DocumentObjectGroupPython] P_element003  label="P_element : 0.103"  # scripted group (container) (typed FeaturePython)
  n = 0.103
FEATURE [App::DocumentObjectGroupPython] S_element005  label="S_element : 0.004"  # scripted group (container) (typed FeaturePython)
  n = 0.003
FEATURE [App::DocumentObjectGroupPython] Ca_element004  label="Ca_element : 0.225"  # scripted group (container) (typed FeaturePython)
  n = 0.225
FEATURE [App::DocumentObjectGroupPython] G4_BONE_CORTICAL_ICRP  # scripted group (container) (typed FeaturePython)
  Dunit = g/cm3
  Dvalue = 1.92
  Group = -> [H_element016,C_element016,N_element011,O_element015,Na_element003,Mg_element002,P_element003,S_element005,Ca_element004]
  conduct = 2
  density = 1
  expand = 3
  formula = G4_BONE_CORTICAL_ICRP
  name = G4_BONE_CORTICAL_ICRP
  specific = 4
FEATURE [App::DocumentObjectGroupPython] B_element001  label="B_element : 4"  # scripted group (container) (typed FeaturePython)
  n = 4
  ref = B_element
FEATURE [App::DocumentObjectGroupPython] C_element017  label="C_element : 1"  # scripted group (container) (typed FeaturePython)
  n = 1
  ref = C_element
FEATURE [App::DocumentObjectGroupPython] G4_BORON_CARBIDE  # scripted group (container) (typed FeaturePython)
  Dunit = g/cm3
  Dvalue = 2.52
  Group = -> [B_element001,C_element017]
  conduct = 2
  density = 1
  expand = 3
  formula = G4_BORON_CARBIDE
  name = G4_BORON_CARBIDE
  specific = 4
FEATURE [App::DocumentObjectGroupPython] B_element002  label="B_element : 2"  # scripted group (container) (typed FeaturePython)
  n = 2
  ref = B_element
FEATURE [App::DocumentObjectGroupPython] O_element016  label="O_element : 006"  # scripted group (container) (typed FeaturePython)
  n = 3
  ref = O_element
FEATURE [App::DocumentObjectGroupPython] G4_BORON_OXIDE  # scripted group (container) (typed FeaturePython)
  Dunit = g/cm3
  Dvalue = 1.812
  Group = -> [B_element002,O_element016]
  conduct = 2
  density = 1
  expand = 3
  formula = G4_BORON_OXIDE
  name = G4_BORON_OXIDE
  specific = 4
FEATURE [App::DocumentObjectGroupPython] H_element017  label="H_element : 0.107"  # scripted group (container) (typed FeaturePython)
  n = 0.107
FEATURE [App::DocumentObjectGroupPython] C_element018  label="C_element : 0.145"  # scripted group (container) (typed FeaturePython)
  n = 0.145
FEATURE [App::DocumentObjectGroupPython] N_element012  label="N_element : 0.022"  # scripted group (container) (typed FeaturePython)
  n = 0.022
FEATURE [App::DocumentObjectGroupPython] O_element017  label="O_element : 0.712"  # scripted group (container) (typed FeaturePython)
  n = 0.712
FEATURE [App::DocumentObjectGroupPython] Na_element004  label="Na_element : 0.004"  # scripted group (container) (typed FeaturePython)
  n = 0.002
FEATURE [App::DocumentObjectGroupPython] P_element004  label="P_element : 0.004"  # scripted group (container) (typed FeaturePython)
  n = 0.004
FEATURE [App::DocumentObjectGroupPython] S_element006  label="S_element : 0.005"  # scripted group (container) (typed FeaturePython)
  n = 0.002
FEATURE [App::DocumentObjectGroupPython] Cl_element003  label="Cl_element : 0.004"  # scripted group (container) (typed FeaturePython)
  n = 0.003
FEATURE [App::DocumentObjectGroupPython] K_element002  label="K_element : 0.003"  # scripted group (container) (typed FeaturePython)
  n = 0.003
FEATURE [App::DocumentObjectGroupPython] G4_BRAIN_ICRP  # scripted group (container) (typed FeaturePython)
  Dunit = g/cm3
  Dvalue = 1.04
  Group = -> [H_element017,C_element018,N_element012,O_element017,Na_element004,P_element004,S_element006,Cl_element003,K_element002]
  conduct = 2
  density = 1
  expand = 3
  formula = G4_BRAIN_ICRP
  name = G4_BRAIN_ICRP
  specific = 4
FEATURE [App::DocumentObjectGroupPython] C_element019  label="C_element : 4"  # scripted group (container) (typed FeaturePython)
  n = 4
  ref = C_element
FEATURE [App::DocumentObjectGroupPython] H_element018  label="H_element : 010"  # scripted group (container) (typed FeaturePython)
  n = 10
  ref = H_element
FEATURE [App::DocumentObjectGroupPython] G4_BUTANE  # scripted group (container) (typed FeaturePython)
  Dunit = g/cm3
  Dvalue = 0.00249343
  Group = -> [C_element019,H_element018]
  conduct = 2
  density = 1
  expand = 3
  formula = G4_BUTANE
  name = G4_BUTANE
  specific = 4
FEATURE [App::DocumentObjectGroupPython] C_element020  label="C_element : 008"  # scripted group (container) (typed FeaturePython)
  n = 4
  ref = C_element
FEATURE [App::DocumentObjectGroupPython] H_element019  label="H_element : 011"  # scripted group (container) (typed FeaturePython)
  n = 10
  ref = H_element
FEATURE [App::DocumentObjectGroupPython] O_element018  label="O_element : 007"  # scripted group (container) (typed FeaturePython)
  n = 1
  ref = O_element
FEATURE [App::DocumentObjectGroupPython] G4_N_BUTYL_ALCOHOL  label="G4_N-BUTYL_ALCOHOL"  # scripted group (container) (typed FeaturePython)
  Dunit = g/cm3
  Dvalue = 0.8098
  Group = -> [C_element020,H_element019,O_element018]
  conduct = 2
  density = 1
  expand = 3
  formula = G4_N-BUTYL_ALCOHOL
  name = G4_N-BUTYL_ALCOHOL
  specific = 4
FEATURE [App::DocumentObjectGroupPython] H_element020  label="H_element : 0.025"  # scripted group (container) (typed FeaturePython)
  n = 0.02468
FEATURE [App::DocumentObjectGroupPython] C_element021  label="C_element : 0.502"  # scripted group (container) (typed FeaturePython)
  n = 0.501611
FEATURE [App::DocumentObjectGroupPython] O_element019  label="O_element : 0.005"  # scripted group (container) (typed FeaturePython)
  n = 0.004527
FEATURE [App::DocumentObjectGroupPython] F_element004  label="F_element : 0.465"  # scripted group (container) (typed FeaturePython)
  n = 0.465209
FEATURE [App::DocumentObjectGroupPython] Si_element001  label="Si_element : 0.004"  # scripted group (container) (typed FeaturePython)
  n = 0.003973
FEATURE [App::DocumentObjectGroupPython] G4_C_552  label="G4_C-552"  # scripted group (container) (typed FeaturePython)
  Dunit = g/cm3
  Dvalue = 1.76
  Group = -> [H_element020,C_element021,O_element019,F_element004,Si_element001]
  conduct = 2
  density = 1
  expand = 3
  formula = G4_C-552
  name = G4_C-552
  specific = 4
FEATURE [App::DocumentObjectGroupPython] Cd_element001  label="Cd_element : 1"  # scripted group (container) (typed FeaturePython)
  n = 1
  ref = Cd_element
FEATURE [App::DocumentObjectGroupPython] Te_element001  label="Te_element : 1"  # scripted group (container) (typed FeaturePython)
  n = 1
  ref = Te_element
FEATURE [App::DocumentObjectGroupPython] G4_CADMIUM_TELLURIDE  # scripted group (container) (typed FeaturePython)
  Dunit = g/cm3
  Dvalue = 6.2
  Group = -> [Cd_element001,Te_element001]
  conduct = 2
  density = 1
  expand = 3
  formula = G4_CADMIUM_TELLURIDE
  name = G4_CADMIUM_TELLURIDE
  specific = 4
FEATURE [App::DocumentObjectGroupPython] Cd_element002  label="Cd_element : 002"  # scripted group (container) (typed FeaturePython)
  n = 1
  ref = Cd_element
FEATURE [App::DocumentObjectGroupPython] W_element001  label="W_element : 1"  # scripted group (container) (typed FeaturePython)
  n = 1
  ref = W_element
FEATURE [App::DocumentObjectGroupPython] O_element020  label="O_element : 008"  # scripted group (container) (typed FeaturePython)
  n = 4
  ref = O_element
FEATURE [App::DocumentObjectGroupPython] G4_CADMIUM_TUNGSTATE  # scripted group (container) (typed FeaturePython)
  Dunit = g/cm3
  Dvalue = 7.9
  Group = -> [Cd_element002,W_element001,O_element020]
  conduct = 2
  density = 1
  expand = 3
  formula = G4_CADMIUM_TUNGSTATE
  name = G4_CADMIUM_TUNGSTATE
  specific = 4
FEATURE [App::DocumentObjectGroupPython] Ca_element005  label="Ca_element : 1"  # scripted group (container) (typed FeaturePython)
  n = 1
  ref = Ca_element
FEATURE [App::DocumentObjectGroupPython] C_element022  label="C_element : 009"  # scripted group (container) (typed FeaturePython)
  n = 1
  ref = C_element
FEATURE [App::DocumentObjectGroupPython] O_element021  label="O_element : 009"  # scripted group (container) (typed FeaturePython)
  n = 3
  ref = O_element
FEATURE [App::DocumentObjectGroupPython] G4_CALCIUM_CARBONATE  # scripted group (container) (typed FeaturePython)
  Dunit = g/cm3
  Dvalue = 2.8
  Group = -> [Ca_element005,C_element022,O_element021]
  conduct = 2
  density = 1
  expand = 3
  formula = G4_CALCIUM_CARBONATE
  name = G4_CALCIUM_CARBONATE
  specific = 4
FEATURE [App::DocumentObjectGroupPython] Ca_element006  label="Ca_element : 002"  # scripted group (container) (typed FeaturePython)
  n = 1
  ref = Ca_element
FEATURE [App::DocumentObjectGroupPython] F_element005  label="F_element : 003"  # scripted group (container) (typed FeaturePython)
  n = 2
  ref = F_element
FEATURE [App::DocumentObjectGroupPython] G4_CALCIUM_FLUORIDE  # scripted group (container) (typed FeaturePython)
  Dunit = g/cm3
  Dvalue = 3.18
  Group = -> [Ca_element006,F_element005]
  conduct = 2
  density = 1
  expand = 3
  formula = G4_CALCIUM_FLUORIDE
  name = G4_CALCIUM_FLUORIDE
  specific = 4
FEATURE [App::DocumentObjectGroupPython] Ca_element007  label="Ca_element : 003"  # scripted group (container) (typed FeaturePython)
  n = 1
  ref = Ca_element
FEATURE [App::DocumentObjectGroupPython] O_element022  label="O_element : 010"  # scripted group (container) (typed FeaturePython)
  n = 1
  ref = O_element
FEATURE [App::DocumentObjectGroupPython] G4_CALCIUM_OXIDE  # scripted group (container) (typed FeaturePython)
  Dunit = g/cm3
  Dvalue = 3.3
  Group = -> [Ca_element007,O_element022]
  conduct = 2
  density = 1
  expand = 3
  formula = G4_CALCIUM_OXIDE
  name = G4_CALCIUM_OXIDE
  specific = 4
FEATURE [App::DocumentObjectGroupPython] Ca_element008  label="Ca_element : 004"  # scripted group (container) (typed FeaturePython)
  n = 1
  ref = Ca_element
FEATURE [App::DocumentObjectGroupPython] S_element007  label="S_element : 002"  # scripted group (container) (typed FeaturePython)
  n = 1
  ref = S_element
FEATURE [App::DocumentObjectGroupPython] O_element023  label="O_element : 011"  # scripted group (container) (typed FeaturePython)
  n = 4
  ref = O_element
FEATURE [App::DocumentObjectGroupPython] G4_CALCIUM_SULFATE  # scripted group (container) (typed FeaturePython)
  Dunit = g/cm3
  Dvalue = 2.96
  Group = -> [Ca_element008,S_element007,O_element023]
  conduct = 2
  density = 1
  expand = 3
  formula = G4_CALCIUM_SULFATE
  name = G4_CALCIUM_SULFATE
  specific = 4
FEATURE [App::DocumentObjectGroupPython] Ca_element009  label="Ca_element : 005"  # scripted group (container) (typed FeaturePython)
  n = 1
  ref = Ca_element
FEATURE [App::DocumentObjectGroupPython] W_element002  label="W_element : 002"  # scripted group (container) (typed FeaturePython)
  n = 1
  ref = W_element
FEATURE [App::DocumentObjectGroupPython] O_element024  label="O_element : 012"  # scripted group (container) (typed FeaturePython)
  n = 4
  ref = O_element
FEATURE [App::DocumentObjectGroupPython] G4_CALCIUM_TUNGSTATE  # scripted group (container) (typed FeaturePython)
  Dunit = g/cm3
  Dvalue = 6.062
  Group = -> [Ca_element009,W_element002,O_element024]
  conduct = 2
  density = 1
  expand = 3
  formula = G4_CALCIUM_TUNGSTATE
  name = G4_CALCIUM_TUNGSTATE
  specific = 4
FEATURE [App::DocumentObjectGroupPython] C_element023  label="C_element : 010"  # scripted group (container) (typed FeaturePython)
  n = 1
  ref = C_element
FEATURE [App::DocumentObjectGroupPython] O_element025  label="O_element : 013"  # scripted group (container) (typed FeaturePython)
  n = 2
  ref = O_element
FEATURE [App::DocumentObjectGroupPython] G4_CARBON_DIOXIDE  # scripted group (container) (typed FeaturePython)
  Dunit = g/cm3
  Dvalue = 0.00184212
  Group = -> [C_element023,O_element025]
  conduct = 2
  density = 1
  expand = 3
  formula = G4_CARBON_DIOXIDE
  name = G4_CARBON_DIOXIDE
  specific = 4
FEATURE [App::DocumentObjectGroupPython] C_element024  label="C_element : 011"  # scripted group (container) (typed FeaturePython)
  n = 1
  ref = C_element
FEATURE [App::DocumentObjectGroupPython] Cl_element004  label="Cl_element : 4"  # scripted group (container) (typed FeaturePython)
  n = 4
  ref = Cl_element
FEATURE [App::DocumentObjectGroupPython] G4_CARBON_TETRACHLORIDE  # scripted group (container) (typed FeaturePython)
  Dunit = g/cm3
  Dvalue = 1.594
  Group = -> [C_element024,Cl_element004]
  conduct = 2
  density = 1
  expand = 3
  formula = G4_CARBON_TETRACHLORIDE
  name = G4_CARBON_TETRACHLORIDE
  specific = 4
FEATURE [App::DocumentObjectGroupPython] C_element025  label="C_element : 012"  # scripted group (container) (typed FeaturePython)
  n = 6
  ref = C_element
FEATURE [App::DocumentObjectGroupPython] H_element021  label="H_element : 012"  # scripted group (container) (typed FeaturePython)
  n = 10
  ref = H_element
FEATURE [App::DocumentObjectGroupPython] O_element026  label="O_element : 5"  # scripted group (container) (typed FeaturePython)
  n = 5
  ref = O_element
FEATURE [App::DocumentObjectGroupPython] G4_CELLULOSE_CELLOPHANE  # scripted group (container) (typed FeaturePython)
  Dunit = g/cm3
  Dvalue = 1.42
  Group = -> [C_element025,H_element021,O_element026]
  conduct = 2
  density = 1
  expand = 3
  formula = G4_CELLULOSE_CELLOPHANE
  name = G4_CELLULOSE_CELLOPHANE
  specific = 4
FEATURE [App::DocumentObjectGroupPython] H_element022  label="H_element : 0.067"  # scripted group (container) (typed FeaturePython)
  n = 0.067125
FEATURE [App::DocumentObjectGroupPython] C_element026  label="C_element : 0.545"  # scripted group (container) (typed FeaturePython)
  n = 0.545403
FEATURE [App::DocumentObjectGroupPython] O_element027  label="O_element : 0.387"  # scripted group (container) (typed FeaturePython)
  n = 0.387472
FEATURE [App::DocumentObjectGroupPython] G4_CELLULOSE_BUTYRATE  # scripted group (container) (typed FeaturePython)
  Dunit = g/cm3
  Dvalue = 1.2
  Group = -> [H_element022,C_element026,O_element027]
  conduct = 2
  density = 1
  expand = 3
  formula = G4_CELLULOSE_BUTYRATE
  name = G4_CELLULOSE_BUTYRATE
  specific = 4
FEATURE [App::DocumentObjectGroupPython] H_element023  label="H_element : 0.029"  # scripted group (container) (typed FeaturePython)
  n = 0.029216
FEATURE [App::DocumentObjectGroupPython] C_element027  label="C_element : 0.271"  # scripted group (container) (typed FeaturePython)
  n = 0.271296
FEATURE [App::DocumentObjectGroupPython] N_element013  label="N_element : 0.121"  # scripted group (container) (typed FeaturePython)
  n = 0.121276
FEATURE [App::DocumentObjectGroupPython] O_element028  label="O_element : 0.578"  # scripted group (container) (typed FeaturePython)
  n = 0.578212
FEATURE [App::DocumentObjectGroupPython] G4_CELLULOSE_NITRATE  # scripted group (container) (typed FeaturePython)
  Dunit = g/cm3
  Dvalue = 1.49
  Group = -> [H_element023,C_element027,N_element013,O_element028]
  conduct = 2
  density = 1
  expand = 3
  formula = G4_CELLULOSE_NITRATE
  name = G4_CELLULOSE_NITRATE
  specific = 4
FEATURE [App::DocumentObjectGroupPython] H_element024  label="H_element : 0.108"  # scripted group (container) (typed FeaturePython)
  n = 0.107596
FEATURE [App::DocumentObjectGroupPython] N_element014  label="N_element : 0.001"  # scripted group (container) (typed FeaturePython)
  n = 0.0008
FEATURE [App::DocumentObjectGroupPython] O_element029  label="O_element : 0.875"  # scripted group (container) (typed FeaturePython)
  n = 0.874976
FEATURE [App::DocumentObjectGroupPython] S_element008  label="S_element : 0.015"  # scripted group (container) (typed FeaturePython)
  n = 0.014627
FEATURE [App::DocumentObjectGroupPython] Ce_element001  label="Ce_element : 0.002"  # scripted group (container) (typed FeaturePython)
  n = 0.002001
FEATURE [App::DocumentObjectGroupPython] G4_CERIC_SULFATE  # scripted group (container) (typed FeaturePython)
  Dunit = g/cm3
  Dvalue = 1.03
  Group = -> [H_element024,N_element014,O_element029,S_element008,Ce_element001]
  conduct = 2
  density = 1
  expand = 3
  formula = G4_CERIC_SULFATE
  name = G4_CERIC_SULFATE
  specific = 4
FEATURE [App::DocumentObjectGroupPython] Cs_element001  label="Cs_element : 1"  # scripted group (container) (typed FeaturePython)
  n = 1
  ref = Cs_element
FEATURE [App::DocumentObjectGroupPython] F_element006  label="F_element : 1"  # scripted group (container) (typed FeaturePython)
  n = 1
  ref = F_element
FEATURE [App::DocumentObjectGroupPython] G4_CESIUM_FLUORIDE  # scripted group (container) (typed FeaturePython)
  Dunit = g/cm3
  Dvalue = 4.115
  Group = -> [Cs_element001,F_element006]
  conduct = 2
  density = 1
  expand = 3
  formula = G4_CESIUM_FLUORIDE
  name = G4_CESIUM_FLUORIDE
  specific = 4
FEATURE [App::DocumentObjectGroupPython] Cs_element002  label="Cs_element : 002"  # scripted group (container) (typed FeaturePython)
  n = 1
  ref = Cs_element
FEATURE [App::DocumentObjectGroupPython] I_element001  label="I_element : 1"  # scripted group (container) (typed FeaturePython)
  n = 1
  ref = I_element
FEATURE [App::DocumentObjectGroupPython] G4_CESIUM_IODIDE  # scripted group (container) (typed FeaturePython)
  Dunit = g/cm3
  Dvalue = 4.51
  Group = -> [Cs_element002,I_element001]
  conduct = 2
  density = 1
  expand = 3
  formula = G4_CESIUM_IODIDE
  name = G4_CESIUM_IODIDE
  specific = 4
FEATURE [App::DocumentObjectGroupPython] C_element028  label="C_element : 013"  # scripted group (container) (typed FeaturePython)
  n = 6
  ref = C_element
FEATURE [App::DocumentObjectGroupPython] H_element025  label="H_element : 013"  # scripted group (container) (typed FeaturePython)
  n = 5
  ref = H_element
FEATURE [App::DocumentObjectGroupPython] Cl_element005  label="Cl_element : 1"  # scripted group (container) (typed FeaturePython)
  n = 1
  ref = Cl_element
FEATURE [App::DocumentObjectGroupPython] G4_CHLOROBENZENE  # scripted group (container) (typed FeaturePython)
  Dunit = g/cm3
  Dvalue = 1.1058
  Group = -> [C_element028,H_element025,Cl_element005]
  conduct = 2
  density = 1
  expand = 3
  formula = G4_CHLOROBENZENE
  name = G4_CHLOROBENZENE
  specific = 4
FEATURE [App::DocumentObjectGroupPython] C_element029  label="C_element : 014"  # scripted group (container) (typed FeaturePython)
  n = 1
  ref = C_element
FEATURE [App::DocumentObjectGroupPython] H_element026  label="H_element : 1"  # scripted group (container) (typed FeaturePython)
  n = 1
  ref = H_element
FEATURE [App::DocumentObjectGroupPython] Cl_element006  label="Cl_element : 3"  # scripted group (container) (typed FeaturePython)
  n = 3
  ref = Cl_element
FEATURE [App::DocumentObjectGroupPython] G4_CHLOROFORM  # scripted group (container) (typed FeaturePython)
  Dunit = g/cm3
  Dvalue = 1.4832
  Group = -> [C_element029,H_element026,Cl_element006]
  conduct = 2
  density = 1
  expand = 3
  formula = G4_CHLOROFORM
  name = G4_CHLOROFORM
  specific = 4
FEATURE [App::DocumentObjectGroupPython] H_element027  label="H_element : 0.010"  # scripted group (container) (typed FeaturePython)
  n = 0.01
FEATURE [App::DocumentObjectGroupPython] C_element030  label="C_element : 0.001"  # scripted group (container) (typed FeaturePython)
  n = 0.001
FEATURE [App::DocumentObjectGroupPython] O_element030  label="O_element : 0.529"  # scripted group (container) (typed FeaturePython)
  n = 0.529107
FEATURE [App::DocumentObjectGroupPython] Na_element005  label="Na_element : 0.016"  # scripted group (container) (typed FeaturePython)
  n = 0.016
FEATURE [App::DocumentObjectGroupPython] Mg_element003  label="Mg_element : 0.004"  # scripted group (container) (typed FeaturePython)
  n = 0.002
FEATURE [App::DocumentObjectGroupPython] Al_element002  label="Al_element : 0.034"  # scripted group (container) (typed FeaturePython)
  n = 0.033872
FEATURE [App::DocumentObjectGroupPython] Si_element002  label="Si_element : 0.337"  # scripted group (container) (typed FeaturePython)
  n = 0.337021
FEATURE [App::DocumentObjectGroupPython] K_element003  label="K_element : 0.013"  # scripted group (container) (typed FeaturePython)
  n = 0.013
FEATURE [App::DocumentObjectGroupPython] Ca_element010  label="Ca_element : 0.044"  # scripted group (container) (typed FeaturePython)
  n = 0.044
FEATURE [App::DocumentObjectGroupPython] Fe_element002  label="Fe_element : 0.014"  # scripted group (container) (typed FeaturePython)
  n = 0.014
FEATURE [App::DocumentObjectGroupPython] G4_CONCRETE  # scripted group (container) (typed FeaturePython)
  Dunit = g/cm3
  Dvalue = 2.3
  Group = -> [H_element027,C_element030,O_element030,Na_element005,Mg_element003,Al_element002,Si_element002,K_element003,Ca_element010,Fe_element002]
  conduct = 2
  density = 1
  expand = 3
  formula = G4_CONCRETE
  name = G4_CONCRETE
  specific = 4
FEATURE [App::DocumentObjectGroupPython] C_element031  label="C_element : 015"  # scripted group (container) (typed FeaturePython)
  n = 6
  ref = C_element
FEATURE [App::DocumentObjectGroupPython] H_element028  label="H_element : 12"  # scripted group (container) (typed FeaturePython)
  n = 12
  ref = H_element
FEATURE [App::DocumentObjectGroupPython] G4_CYCLOHEXANE  # scripted group (container) (typed FeaturePython)
  Dunit = g/cm3
  Dvalue = 0.779
  Group = -> [C_element031,H_element028]
  conduct = 2
  density = 1
  expand = 3
  formula = G4_CYCLOHEXANE
  name = G4_CYCLOHEXANE
  specific = 4
FEATURE [App::DocumentObjectGroupPython] C_element032  label="C_element : 016"  # scripted group (container) (typed FeaturePython)
  n = 6
  ref = C_element
FEATURE [App::DocumentObjectGroupPython] H_element029  label="H_element : 4"  # scripted group (container) (typed FeaturePython)
  n = 4
  ref = H_element
FEATURE [App::DocumentObjectGroupPython] Cl_element007  label="Cl_element : 2"  # scripted group (container) (typed FeaturePython)
  n = 2
  ref = Cl_element
FEATURE [App::DocumentObjectGroupPython] G4_1_2_DICHLOROBENZENE  label="G4_1.2-DICHLOROBENZENE"  # scripted group (container) (typed FeaturePython)
  Dunit = g/cm3
  Dvalue = 1.3048
  Group = -> [C_element032,H_element029,Cl_element007]
  conduct = 2
  density = 1
  expand = 3
  formula = G4_1.2-DICHLOROBENZENE
  name = G4_1.2-DICHLOROBENZENE
  specific = 4
FEATURE [App::DocumentObjectGroupPython] C_element033  label="C_element : 017"  # scripted group (container) (typed FeaturePython)
  n = 4
  ref = C_element
FEATURE [App::DocumentObjectGroupPython] H_element030  label="H_element : 8"  # scripted group (container) (typed FeaturePython)
  n = 8
  ref = H_element
FEATURE [App::DocumentObjectGroupPython] O_element031  label="O_element : 014"  # scripted group (container) (typed FeaturePython)
  n = 1
  ref = O_element
FEATURE [App::DocumentObjectGroupPython] Cl_element008  label="Cl_element : 005"  # scripted group (container) (typed FeaturePython)
  n = 2
  ref = Cl_element
FEATURE [App::DocumentObjectGroupPython] G4_DICHLORODIETHYL_ETHER  # scripted group (container) (typed FeaturePython)
  Dunit = g/cm3
  Dvalue = 1.2199
  Group = -> [C_element033,H_element030,O_element031,Cl_element008]
  conduct = 2
  density = 1
  expand = 3
  formula = G4_DICHLORODIETHYL_ETHER
  name = G4_DICHLORODIETHYL_ETHER
  specific = 4
FEATURE [App::DocumentObjectGroupPython] C_element034  label="C_element : 018"  # scripted group (container) (typed FeaturePython)
  n = 2
  ref = C_element
FEATURE [App::DocumentObjectGroupPython] H_element031  label="H_element : 014"  # scripted group (container) (typed FeaturePython)
  n = 4
  ref = H_element
FEATURE [App::DocumentObjectGroupPython] Cl_element009  label="Cl_element : 006"  # scripted group (container) (typed FeaturePython)
  n = 2
  ref = Cl_element
FEATURE [App::DocumentObjectGroupPython] G4_1_2_DICHLOROETHANE  label="G4_1.2-DICHLOROETHANE"  # scripted group (container) (typed FeaturePython)
  Dunit = g/cm3
  Dvalue = 1.2351
  Group = -> [C_element034,H_element031,Cl_element009]
  conduct = 2
  density = 1
  expand = 3
  formula = G4_1.2-DICHLOROETHANE
  name = G4_1.2-DICHLOROETHANE
  specific = 4
FEATURE [App::DocumentObjectGroupPython] C_element035  label="C_element : 019"  # scripted group (container) (typed FeaturePython)
  n = 4
  ref = C_element
FEATURE [App::DocumentObjectGroupPython] H_element032  label="H_element : 015"  # scripted group (container) (typed FeaturePython)
  n = 10
  ref = H_element
FEATURE [App::DocumentObjectGroupPython] O_element032  label="O_element : 015"  # scripted group (container) (typed FeaturePython)
  n = 1
  ref = O_element
FEATURE [App::DocumentObjectGroupPython] G4_DIETHYL_ETHER  # scripted group (container) (typed FeaturePython)
  Dunit = g/cm3
  Dvalue = 0.71378
  Group = -> [C_element035,H_element032,O_element032]
  conduct = 2
  density = 1
  expand = 3
  formula = G4_DIETHYL_ETHER
  name = G4_DIETHYL_ETHER
  specific = 4
FEATURE [App::DocumentObjectGroupPython] C_element036  label="C_element : 020"  # scripted group (container) (typed FeaturePython)
  n = 3
  ref = C_element
FEATURE [App::DocumentObjectGroupPython] H_element033  label="H_element : 016"  # scripted group (container) (typed FeaturePython)
  n = 7
  ref = H_element
FEATURE [App::DocumentObjectGroupPython] N_element015  label="N_element : 008"  # scripted group (container) (typed FeaturePython)
  n = 1
  ref = N_element
FEATURE [App::DocumentObjectGroupPython] O_element033  label="O_element : 016"  # scripted group (container) (typed FeaturePython)
  n = 1
  ref = O_element
FEATURE [App::DocumentObjectGroupPython] G4_N_N_DIMETHYL_FORMAMIDE  label="G4_N.N-DIMETHYL_FORMAMIDE"  # scripted group (container) (typed FeaturePython)
  Dunit = g/cm3
  Dvalue = 0.9487
  Group = -> [C_element036,H_element033,N_element015,O_element033]
  conduct = 2
  density = 1
  expand = 3
  formula = G4_N.N-DIMETHYL_FORMAMIDE
  name = G4_N.N-DIMETHYL_FORMAMIDE
  specific = 4
FEATURE [App::DocumentObjectGroupPython] C_element037  label="C_element : 021"  # scripted group (container) (typed FeaturePython)
  n = 2
  ref = C_element
FEATURE [App::DocumentObjectGroupPython] H_element034  label="H_element : 017"  # scripted group (container) (typed FeaturePython)
  n = 6
  ref = H_element
FEATURE [App::DocumentObjectGroupPython] O_element034  label="O_element : 017"  # scripted group (container) (typed FeaturePython)
  n = 1
  ref = O_element
FEATURE [App::DocumentObjectGroupPython] S_element009  label="S_element : 003"  # scripted group (container) (typed FeaturePython)
  n = 1
  ref = S_element
FEATURE [App::DocumentObjectGroupPython] G4_DIMETHYL_SULFOXIDE  # scripted group (container) (typed FeaturePython)
  Dunit = g/cm3
  Dvalue = 1.1014
  Group = -> [C_element037,H_element034,O_element034,S_element009]
  conduct = 2
  density = 1
  expand = 3
  formula = G4_DIMETHYL_SULFOXIDE
  name = G4_DIMETHYL_SULFOXIDE
  specific = 4
FEATURE [App::DocumentObjectGroupPython] C_element038  label="C_element : 022"  # scripted group (container) (typed FeaturePython)
  n = 2
  ref = C_element
FEATURE [App::DocumentObjectGroupPython] H_element035  label="H_element : 018"  # scripted group (container) (typed FeaturePython)
  n = 6
  ref = H_element
FEATURE [App::DocumentObjectGroupPython] G4_ETHANE  # scripted group (container) (typed FeaturePython)
  Dunit = g/cm3
  Dvalue = 0.00125324
  Group = -> [C_element038,H_element035]
  conduct = 2
  density = 1
  expand = 3
  formula = G4_ETHANE
  name = G4_ETHANE
  specific = 4
FEATURE [App::DocumentObjectGroupPython] C_element039  label="C_element : 023"  # scripted group (container) (typed FeaturePython)
  n = 2
  ref = C_element
FEATURE [App::DocumentObjectGroupPython] H_element036  label="H_element : 019"  # scripted group (container) (typed FeaturePython)
  n = 6
  ref = H_element
FEATURE [App::DocumentObjectGroupPython] O_element035  label="O_element : 018"  # scripted group (container) (typed FeaturePython)
  n = 1
  ref = O_element
FEATURE [App::DocumentObjectGroupPython] G4_ETHYL_ALCOHOL  # scripted group (container) (typed FeaturePython)
  Dunit = g/cm3
  Dvalue = 0.7893
  Group = -> [C_element039,H_element036,O_element035]
  conduct = 2
  density = 1
  expand = 3
  formula = G4_ETHYL_ALCOHOL
  name = G4_ETHYL_ALCOHOL
  specific = 4
FEATURE [App::DocumentObjectGroupPython] H_element037  label="H_element : 0.090"  # scripted group (container) (typed FeaturePython)
  n = 0.090027
FEATURE [App::DocumentObjectGroupPython] C_element040  label="C_element : 0.585"  # scripted group (container) (typed FeaturePython)
  n = 0.585182
FEATURE [App::DocumentObjectGroupPython] O_element036  label="O_element : 0.325"  # scripted group (container) (typed FeaturePython)
  n = 0.324791
FEATURE [App::DocumentObjectGroupPython] G4_ETHYL_CELLULOSE  # scripted group (container) (typed FeaturePython)
  Dunit = g/cm3
  Dvalue = 1.13
  Group = -> [H_element037,C_element040,O_element036]
  conduct = 2
  density = 1
  expand = 3
  formula = G4_ETHYL_CELLULOSE
  name = G4_ETHYL_CELLULOSE
  specific = 4
FEATURE [App::DocumentObjectGroupPython] C_element041  label="C_element : 024"  # scripted group (container) (typed FeaturePython)
  n = 2
  ref = C_element
FEATURE [App::DocumentObjectGroupPython] H_element038  label="H_element : 020"  # scripted group (container) (typed FeaturePython)
  n = 4
  ref = H_element
FEATURE [App::DocumentObjectGroupPython] G4_ETHYLENE  # scripted group (container) (typed FeaturePython)
  Dunit = g/cm3
  Dvalue = 0.00117497
  Group = -> [C_element041,H_element038]
  conduct = 2
  density = 1
  expand = 3
  formula = G4_ETHYLENE
  name = G4_ETHYLENE
  specific = 4
FEATURE [App::DocumentObjectGroupPython] H_element039  label="H_element : 0.096"  # scripted group (container) (typed FeaturePython)
  n = 0.096
FEATURE [App::DocumentObjectGroupPython] C_element042  label="C_element : 0.195"  # scripted group (container) (typed FeaturePython)
  n = 0.195
FEATURE [App::DocumentObjectGroupPython] N_element016  label="N_element : 0.057"  # scripted group (container) (typed FeaturePython)
  n = 0.057
FEATURE [App::DocumentObjectGroupPython] O_element037  label="O_element : 0.646"  # scripted group (container) (typed FeaturePython)
  n = 0.646
FEATURE [App::DocumentObjectGroupPython] Na_element006  label="Na_element : 0.017"  # scripted group (container) (typed FeaturePython)
  n = 0.001
FEATURE [App::DocumentObjectGroupPython] P_element005  label="P_element : 0.104"  # scripted group (container) (typed FeaturePython)
  n = 0.001
FEATURE [App::DocumentObjectGroupPython] S_element010  label="S_element : 0.016"  # scripted group (container) (typed FeaturePython)
  n = 0.003
FEATURE [App::DocumentObjectGroupPython] Cl_element010  label="Cl_element : 0.005"  # scripted group (container) (typed FeaturePython)
  n = 0.001
FEATURE [App::DocumentObjectGroupPython] G4_EYE_LENS_ICRP  # scripted group (container) (typed FeaturePython)
  Dunit = g/cm3
  Dvalue = 1.07
  Group = -> [H_element039,C_element042,N_element016,O_element037,Na_element006,P_element005,S_element010,Cl_element010]
  conduct = 2
  density = 1
  expand = 3
  formula = G4_EYE_LENS_ICRP
  name = G4_EYE_LENS_ICRP
  specific = 4
FEATURE [App::DocumentObjectGroupPython] Fe_element003  label="Fe_element : 2"  # scripted group (container) (typed FeaturePython)
  n = 2
  ref = Fe_element
FEATURE [App::DocumentObjectGroupPython] O_element038  label="O_element : 019"  # scripted group (container) (typed FeaturePython)
  n = 3
  ref = O_element
FEATURE [App::DocumentObjectGroupPython] G4_FERRIC_OXIDE  # scripted group (container) (typed FeaturePython)
  Dunit = g/cm3
  Dvalue = 5.2
  Group = -> [Fe_element003,O_element038]
  conduct = 2
  density = 1
  expand = 3
  formula = G4_FERRIC_OXIDE
  name = G4_FERRIC_OXIDE
  specific = 4
FEATURE [App::DocumentObjectGroupPython] Fe_element004  label="Fe_element : 1"  # scripted group (container) (typed FeaturePython)
  n = 1
  ref = Fe_element
FEATURE [App::DocumentObjectGroupPython] B_element003  label="B_element : 1"  # scripted group (container) (typed FeaturePython)
  n = 1
  ref = B_element
FEATURE [App::DocumentObjectGroupPython] G4_FERROBORIDE  # scripted group (container) (typed FeaturePython)
  Dunit = g/cm3
  Dvalue = 7.15
  Group = -> [Fe_element004,B_element003]
  conduct = 2
  density = 1
  expand = 3
  formula = G4_FERROBORIDE
  name = G4_FERROBORIDE
  specific = 4
FEATURE [App::DocumentObjectGroupPython] Fe_element005  label="Fe_element : 003"  # scripted group (container) (typed FeaturePython)
  n = 1
  ref = Fe_element
FEATURE [App::DocumentObjectGroupPython] O_element039  label="O_element : 020"  # scripted group (container) (typed FeaturePython)
  n = 1
  ref = O_element
FEATURE [App::DocumentObjectGroupPython] G4_FERROUS_OXIDE  # scripted group (container) (typed FeaturePython)
  Dunit = g/cm3
  Dvalue = 5.7
  Group = -> [Fe_element005,O_element039]
  conduct = 2
  density = 1
  expand = 3
  formula = G4_FERROUS_OXIDE
  name = G4_FERROUS_OXIDE
  specific = 4
FEATURE [App::DocumentObjectGroupPython] H_element040  label="H_element : 0.115"  # scripted group (container) (typed FeaturePython)
  n = 0.108259
FEATURE [App::DocumentObjectGroupPython] N_element017  label="N_element : 0.000"  # scripted group (container) (typed FeaturePython)
  n = 2.7e-05
FEATURE [App::DocumentObjectGroupPython] O_element040  label="O_element : 0.879"  # scripted group (container) (typed FeaturePython)
  n = 0.878636
FEATURE [App::DocumentObjectGroupPython] Na_element007  label="Na_element : 0.000"  # scripted group (container) (typed FeaturePython)
  n = 2.2e-05
FEATURE [App::DocumentObjectGroupPython] S_element011  label="S_element : 0.013"  # scripted group (container) (typed FeaturePython)
  n = 0.012968
FEATURE [App::DocumentObjectGroupPython] Cl_element011  label="Cl_element : 0.000"  # scripted group (container) (typed FeaturePython)
  n = 3.4e-05
FEATURE [App::DocumentObjectGroupPython] Fe_element006  label="Fe_element : 0.000"  # scripted group (container) (typed FeaturePython)
  n = 5.4e-05
FEATURE [App::DocumentObjectGroupPython] G4_FERROUS_SULFATE  # scripted group (container) (typed FeaturePython)
  Dunit = g/cm3
  Dvalue = 1.024
  Group = -> [H_element040,N_element017,O_element040,Na_element007,S_element011,Cl_element011,Fe_element006]
  conduct = 2
  density = 1
  expand = 3
  formula = G4_FERROUS_SULFATE
  name = G4_FERROUS_SULFATE
  specific = 4
FEATURE [App::DocumentObjectGroupPython] C_element043  label="C_element : 0.099"  # scripted group (container) (typed FeaturePython)
  n = 0.099335
FEATURE [App::DocumentObjectGroupPython] F_element007  label="F_element : 0.314"  # scripted group (container) (typed FeaturePython)
  n = 0.314247
FEATURE [App::DocumentObjectGroupPython] Cl_element012  label="Cl_element : 0.586"  # scripted group (container) (typed FeaturePython)
  n = 0.586418
FEATURE [App::DocumentObjectGroupPython] G4_FREON_12  label="G4_FREON-12"  # scripted group (container) (typed FeaturePython)
  Dunit = g/cm3
  Dvalue = 1.12
  Group = -> [C_element043,F_element007,Cl_element012]
  conduct = 2
  density = 1
  expand = 3
  formula = G4_FREON-12
  name = G4_FREON-12
  specific = 4
FEATURE [App::DocumentObjectGroupPython] C_element044  label="C_element : 0.057"  # scripted group (container) (typed FeaturePython)
  n = 0.057245
FEATURE [App::DocumentObjectGroupPython] F_element008  label="F_element : 0.181"  # scripted group (container) (typed FeaturePython)
  n = 0.181096
FEATURE [App::DocumentObjectGroupPython] Br_element001  label="Br_element : 0.762"  # scripted group (container) (typed FeaturePython)
  n = 0.761659
FEATURE [App::DocumentObjectGroupPython] G4_FREON_12B2  label="G4_FREON-12B2"  # scripted group (container) (typed FeaturePython)
  Dunit = g/cm3
  Dvalue = 1.8
  Group = -> [C_element044,F_element008,Br_element001]
  conduct = 2
  density = 1
  expand = 3
  formula = G4_FREON-12B2
  name = G4_FREON-12B2
  specific = 4
FEATURE [App::DocumentObjectGroupPython] C_element045  label="C_element : 0.115"  # scripted group (container) (typed FeaturePython)
  n = 0.114983
FEATURE [App::DocumentObjectGroupPython] F_element009  label="F_element : 0.546"  # scripted group (container) (typed FeaturePython)
  n = 0.545621
FEATURE [App::DocumentObjectGroupPython] Cl_element013  label="Cl_element : 0.339"  # scripted group (container) (typed FeaturePython)
  n = 0.339396
FEATURE [App::DocumentObjectGroupPython] G4_FREON_13  label="G4_FREON-13"  # scripted group (container) (typed FeaturePython)
  Dunit = g/cm3
  Dvalue = 0.95
  Group = -> [C_element045,F_element009,Cl_element013]
  conduct = 2
  density = 1
  expand = 3
  formula = G4_FREON-13
  name = G4_FREON-13
  specific = 4
FEATURE [App::DocumentObjectGroupPython] C_element046  label="C_element : 025"  # scripted group (container) (typed FeaturePython)
  n = 1
  ref = C_element
FEATURE [App::DocumentObjectGroupPython] F_element010  label="F_element : 3"  # scripted group (container) (typed FeaturePython)
  n = 3
  ref = F_element
FEATURE [App::DocumentObjectGroupPython] Br_element002  label="Br_element : 1"  # scripted group (container) (typed FeaturePython)
  n = 1
  ref = Br_element
FEATURE [App::DocumentObjectGroupPython] G4_FREON_13B1  label="G4_FREON-13B1"  # scripted group (container) (typed FeaturePython)
  Dunit = g/cm3
  Dvalue = 1.5
  Group = -> [C_element046,F_element010,Br_element002]
  conduct = 2
  density = 1
  expand = 3
  formula = G4_FREON-13B1
  name = G4_FREON-13B1
  specific = 4
FEATURE [App::DocumentObjectGroupPython] C_element047  label="C_element : 0.061"  # scripted group (container) (typed FeaturePython)
  n = 0.061309
FEATURE [App::DocumentObjectGroupPython] F_element011  label="F_element : 0.291"  # scripted group (container) (typed FeaturePython)
  n = 0.290924
FEATURE [App::DocumentObjectGroupPython] I_element002  label="I_element : 0.648"  # scripted group (container) (typed FeaturePython)
  n = 0.647767
FEATURE [App::DocumentObjectGroupPython] G4_FREON_13I1  label="G4_FREON-13I1"  # scripted group (container) (typed FeaturePython)
  Dunit = g/cm3
  Dvalue = 1.8
  Group = -> [C_element047,F_element011,I_element002]
  conduct = 2
  density = 1
  expand = 3
  formula = G4_FREON-13I1
  name = G4_FREON-13I1
  specific = 4
FEATURE [App::DocumentObjectGroupPython] Gd_element001  label="Gd_element : 2"  # scripted group (container) (typed FeaturePython)
  n = 2
  ref = Gd_element
FEATURE [App::DocumentObjectGroupPython] O_element041  label="O_element : 021"  # scripted group (container) (typed FeaturePython)
  n = 2
  ref = O_element
FEATURE [App::DocumentObjectGroupPython] S_element012  label="S_element : 004"  # scripted group (container) (typed FeaturePython)
  n = 1
  ref = S_element
FEATURE [App::DocumentObjectGroupPython] G4_GADOLINIUM_OXYSULFIDE  # scripted group (container) (typed FeaturePython)
  Dunit = g/cm3
  Dvalue = 7.44
  Group = -> [Gd_element001,O_element041,S_element012]
  conduct = 2
  density = 1
  expand = 3
  formula = G4_GADOLINIUM_OXYSULFIDE
  name = G4_GADOLINIUM_OXYSULFIDE
  specific = 4
FEATURE [App::DocumentObjectGroupPython] Ga_element001  label="Ga_element : 1"  # scripted group (container) (typed FeaturePython)
  n = 1
  ref = Ga_element
FEATURE [App::DocumentObjectGroupPython] As_element001  label="As_element : 1"  # scripted group (container) (typed FeaturePython)
  n = 1
  ref = As_element
FEATURE [App::DocumentObjectGroupPython] G4_GALLIUM_ARSENIDE  # scripted group (container) (typed FeaturePython)
  Dunit = g/cm3
  Dvalue = 5.31
  Group = -> [Ga_element001,As_element001]
  conduct = 2
  density = 1
  expand = 3
  formula = G4_GALLIUM_ARSENIDE
  name = G4_GALLIUM_ARSENIDE
  specific = 4
FEATURE [App::DocumentObjectGroupPython] H_element041  label="H_element : 0.081"  # scripted group (container) (typed FeaturePython)
  n = 0.08118
FEATURE [App::DocumentObjectGroupPython] C_element048  label="C_element : 0.416"  # scripted group (container) (typed FeaturePython)
  n = 0.41606
FEATURE [App::DocumentObjectGroupPython] N_element018  label="N_element : 0.111"  # scripted group (container) (typed FeaturePython)
  n = 0.11124
FEATURE [App::DocumentObjectGroupPython] O_element042  label="O_element : 0.381"  # scripted group (container) (typed FeaturePython)
  n = 0.38064
FEATURE [App::DocumentObjectGroupPython] S_element013  label="S_element : 0.011"  # scripted group (container) (typed FeaturePython)
  n = 0.01088
FEATURE [App::DocumentObjectGroupPython] G4_GEL_PHOTO_EMULSION  # scripted group (container) (typed FeaturePython)
  Dunit = g/cm3
  Dvalue = 1.2914
  Group = -> [H_element041,C_element048,N_element018,O_element042,S_element013]
  conduct = 2
  density = 1
  expand = 3
  formula = G4_GEL_PHOTO_EMULSION
  name = G4_GEL_PHOTO_EMULSION
  specific = 4
FEATURE [App::DocumentObjectGroupPython] B_element004  label="B_element : 0.040"  # scripted group (container) (typed FeaturePython)
  n = 0.0400639
FEATURE [App::DocumentObjectGroupPython] O_element043  label="O_element : 0.540"  # scripted group (container) (typed FeaturePython)
  n = 0.539561
FEATURE [App::DocumentObjectGroupPython] Na_element008  label="Na_element : 0.028"  # scripted group (container) (typed FeaturePython)
  n = 0.0281909
FEATURE [App::DocumentObjectGroupPython] Al_element003  label="Al_element : 0.012"  # scripted group (container) (typed FeaturePython)
  n = 0.011644
FEATURE [App::DocumentObjectGroupPython] Si_element003  label="Si_element : 0.377"  # scripted group (container) (typed FeaturePython)
  n = 0.377219
FEATURE [App::DocumentObjectGroupPython] K_element004  label="K_element : 0.014"  # scripted group (container) (typed FeaturePython)
  n = 0.00332099
FEATURE [App::DocumentObjectGroupPython] G4_Pyrex_Glass  # scripted group (container) (typed FeaturePython)
  Dunit = g/cm3
  Dvalue = 2.23
  Group = -> [B_element004,O_element043,Na_element008,Al_element003,Si_element003,K_element004]
  conduct = 2
  density = 1
  expand = 3
  formula = G4_Pyrex_Glass
  name = G4_Pyrex_Glass
  specific = 4
FEATURE [App::DocumentObjectGroupPython] O_element044  label="O_element : 0.156"  # scripted group (container) (typed FeaturePython)
  n = 0.156453
FEATURE [App::DocumentObjectGroupPython] Si_element004  label="Si_element : 0.081"  # scripted group (container) (typed FeaturePython)
  n = 0.080866
FEATURE [App::DocumentObjectGroupPython] Ti_element001  label="Ti_element : 0.008"  # scripted group (container) (typed FeaturePython)
  n = 0.008092
FEATURE [App::DocumentObjectGroupPython] As_element002  label="As_element : 0.003"  # scripted group (container) (typed FeaturePython)
  n = 0.002651
FEATURE [App::DocumentObjectGroupPython] Pb_element001  label="Pb_element : 0.752"  # scripted group (container) (typed FeaturePython)
  n = 0.751938
FEATURE [App::DocumentObjectGroupPython] G4_GLASS_LEAD  # scripted group (container) (typed FeaturePython)
  Dunit = g/cm3
  Dvalue = 6.22
  Group = -> [O_element044,Si_element004,Ti_element001,As_element002,Pb_element001]
  conduct = 2
  density = 1
  expand = 3
  formula = G4_GLASS_LEAD
  name = G4_GLASS_LEAD
  specific = 4
FEATURE [App::DocumentObjectGroupPython] O_element045  label="O_element : 0.460"  # scripted group (container) (typed FeaturePython)
  n = 0.4598
FEATURE [App::DocumentObjectGroupPython] Na_element009  label="Na_element : 0.096"  # scripted group (container) (typed FeaturePython)
  n = 0.0964411
FEATURE [App::DocumentObjectGroupPython] Si_element005  label="Si_element : 0.378"  # scripted group (container) (typed FeaturePython)
  n = 0.336553
FEATURE [App::DocumentObjectGroupPython] Ca_element011  label="Ca_element : 0.107"  # scripted group (container) (typed FeaturePython)
  n = 0.107205
FEATURE [App::DocumentObjectGroupPython] G4_GLASS_PLATE  # scripted group (container) (typed FeaturePython)
  Dunit = g/cm3
  Dvalue = 2.4
  Group = -> [O_element045,Na_element009,Si_element005,Ca_element011]
  conduct = 2
  density = 1
  expand = 3
  formula = G4_GLASS_PLATE
  name = G4_GLASS_PLATE
  specific = 4
FEATURE [App::DocumentObjectGroupPython] C_element049  label="C_element : 026"  # scripted group (container) (typed FeaturePython)
  n = 5
  ref = C_element
FEATURE [App::DocumentObjectGroupPython] H_element042  label="H_element : 021"  # scripted group (container) (typed FeaturePython)
  n = 10
  ref = H_element
FEATURE [App::DocumentObjectGroupPython] N_element019  label="N_element : 2"  # scripted group (container) (typed FeaturePython)
  n = 2
  ref = N_element
FEATURE [App::DocumentObjectGroupPython] O_element046  label="O_element : 022"  # scripted group (container) (typed FeaturePython)
  n = 3
  ref = O_element
FEATURE [App::DocumentObjectGroupPython] G4_GLUTAMINE  # scripted group (container) (typed FeaturePython)
  Dunit = g/cm3
  Dvalue = 1.46
  Group = -> [C_element049,H_element042,N_element019,O_element046]
  conduct = 2
  density = 1
  expand = 3
  formula = G4_GLUTAMINE
  name = G4_GLUTAMINE
  specific = 4
FEATURE [App::DocumentObjectGroupPython] C_element050  label="C_element : 027"  # scripted group (container) (typed FeaturePython)
  n = 3
  ref = C_element
FEATURE [App::DocumentObjectGroupPython] H_element043  label="H_element : 022"  # scripted group (container) (typed FeaturePython)
  n = 8
  ref = H_element
FEATURE [App::DocumentObjectGroupPython] O_element047  label="O_element : 023"  # scripted group (container) (typed FeaturePython)
  n = 3
  ref = O_element
FEATURE [App::DocumentObjectGroupPython] G4_GLYCEROL  # scripted group (container) (typed FeaturePython)
  Dunit = g/cm3
  Dvalue = 1.2613
  Group = -> [C_element050,H_element043,O_element047]
  conduct = 2
  density = 1
  expand = 3
  formula = G4_GLYCEROL
  name = G4_GLYCEROL
  specific = 4
FEATURE [App::DocumentObjectGroupPython] C_element051  label="C_element : 028"  # scripted group (container) (typed FeaturePython)
  n = 5
  ref = C_element
FEATURE [App::DocumentObjectGroupPython] H_element044  label="H_element : 023"  # scripted group (container) (typed FeaturePython)
  n = 5
  ref = H_element
FEATURE [App::DocumentObjectGroupPython] N_element020  label="N_element : 009"  # scripted group (container) (typed FeaturePython)
  n = 5
  ref = N_element
FEATURE [App::DocumentObjectGroupPython] O_element048  label="O_element : 024"  # scripted group (container) (typed FeaturePython)
  n = 1
  ref = O_element
FEATURE [App::DocumentObjectGroupPython] G4_GUANINE  # scripted group (container) (typed FeaturePython)
  Dunit = g/cm3
  Dvalue = 2.2
  Group = -> [C_element051,H_element044,N_element020,O_element048]
  conduct = 2
  density = 1
  expand = 3
  formula = G4_GUANINE
  name = G4_GUANINE
  specific = 4
FEATURE [App::DocumentObjectGroupPython] Ca_element012  label="Ca_element : 006"  # scripted group (container) (typed FeaturePython)
  n = 1
  ref = Ca_element
FEATURE [App::DocumentObjectGroupPython] S_element014  label="S_element : 005"  # scripted group (container) (typed FeaturePython)
  n = 1
  ref = S_element
FEATURE [App::DocumentObjectGroupPython] O_element049  label="O_element : 6"  # scripted group (container) (typed FeaturePython)
  n = 6
  ref = O_element
FEATURE [App::DocumentObjectGroupPython] H_element045  label="H_element : 024"  # scripted group (container) (typed FeaturePython)
  n = 4
  ref = H_element
FEATURE [App::DocumentObjectGroupPython] G4_GYPSUM  # scripted group (container) (typed FeaturePython)
  Dunit = g/cm3
  Dvalue = 2.32
  Group = -> [Ca_element012,S_element014,O_element049,H_element045]
  conduct = 2
  density = 1
  expand = 3
  formula = G4_GYPSUM
  name = G4_GYPSUM
  specific = 4
FEATURE [App::DocumentObjectGroupPython] C_element052  label="C_element : 7"  # scripted group (container) (typed FeaturePython)
  n = 7
  ref = C_element
FEATURE [App::DocumentObjectGroupPython] H_element046  label="H_element : 16"  # scripted group (container) (typed FeaturePython)
  n = 16
  ref = H_element
FEATURE [App::DocumentObjectGroupPython] G4_N_HEPTANE  label="G4_N-HEPTANE"  # scripted group (container) (typed FeaturePython)
  Dunit = g/cm3
  Dvalue = 0.68376
  Group = -> [C_element052,H_element046]
  conduct = 2
  density = 1
  expand = 3
  formula = G4_N-HEPTANE
  name = G4_N-HEPTANE
  specific = 4
FEATURE [App::DocumentObjectGroupPython] C_element053  label="C_element : 029"  # scripted group (container) (typed FeaturePython)
  n = 6
  ref = C_element
FEATURE [App::DocumentObjectGroupPython] H_element047  label="H_element : 14"  # scripted group (container) (typed FeaturePython)
  n = 14
  ref = H_element
FEATURE [App::DocumentObjectGroupPython] G4_N_HEXANE  label="G4_N-HEXANE"  # scripted group (container) (typed FeaturePython)
  Dunit = g/cm3
  Dvalue = 0.6603
  Group = -> [C_element053,H_element047]
  conduct = 2
  density = 1
  expand = 3
  formula = G4_N-HEXANE
  name = G4_N-HEXANE
  specific = 4
FEATURE [App::DocumentObjectGroupPython] C_element054  label="C_element : 22"  # scripted group (container) (typed FeaturePython)
  n = 22
  ref = C_element
FEATURE [App::DocumentObjectGroupPython] H_element048  label="H_element : 025"  # scripted group (container) (typed FeaturePython)
  n = 10
  ref = H_element
FEATURE [App::DocumentObjectGroupPython] N_element021  label="N_element : 010"  # scripted group (container) (typed FeaturePython)
  n = 2
  ref = N_element
FEATURE [App::DocumentObjectGroupPython] O_element050  label="O_element : 025"  # scripted group (container) (typed FeaturePython)
  n = 5
  ref = O_element
FEATURE [App::DocumentObjectGroupPython] G4_KAPTON  # scripted group (container) (typed FeaturePython)
  Dunit = g/cm3
  Dvalue = 1.42
  Group = -> [C_element054,H_element048,N_element021,O_element050]
  conduct = 2
  density = 1
  expand = 3
  formula = G4_KAPTON
  name = G4_KAPTON
  specific = 4
FEATURE [App::DocumentObjectGroupPython] La_element001  label="La_element : 1"  # scripted group (container) (typed FeaturePython)
  n = 1
  ref = La_element
FEATURE [App::DocumentObjectGroupPython] Br_element003  label="Br_element : 002"  # scripted group (container) (typed FeaturePython)
  n = 1
  ref = Br_element
FEATURE [App::DocumentObjectGroupPython] O_element051  label="O_element : 026"  # scripted group (container) (typed FeaturePython)
  n = 1
  ref = O_element
FEATURE [App::DocumentObjectGroupPython] G4_LANTHANUM_OXYBROMIDE  # scripted group (container) (typed FeaturePython)
  Dunit = g/cm3
  Dvalue = 6.28
  Group = -> [La_element001,Br_element003,O_element051]
  conduct = 2
  density = 1
  expand = 3
  formula = G4_LANTHANUM_OXYBROMIDE
  name = G4_LANTHANUM_OXYBROMIDE
  specific = 4
FEATURE [App::DocumentObjectGroupPython] La_element002  label="La_element : 2"  # scripted group (container) (typed FeaturePython)
  n = 2
  ref = La_element
FEATURE [App::DocumentObjectGroupPython] O_element052  label="O_element : 027"  # scripted group (container) (typed FeaturePython)
  n = 2
  ref = O_element
FEATURE [App::DocumentObjectGroupPython] S_element015  label="S_element : 006"  # scripted group (container) (typed FeaturePython)
  n = 1
  ref = S_element
FEATURE [App::DocumentObjectGroupPython] G4_LANTHANUM_OXYSULFIDE  # scripted group (container) (typed FeaturePython)
  Dunit = g/cm3
  Dvalue = 5.86
  Group = -> [La_element002,O_element052,S_element015]
  conduct = 2
  density = 1
  expand = 3
  formula = G4_LANTHANUM_OXYSULFIDE
  name = G4_LANTHANUM_OXYSULFIDE
  specific = 4
FEATURE [App::DocumentObjectGroupPython] O_element053  label="O_element : 0.072"  # scripted group (container) (typed FeaturePython)
  n = 0.071682
FEATURE [App::DocumentObjectGroupPython] Pb_element002  label="Pb_element : 0.928"  # scripted group (container) (typed FeaturePython)
  n = 0.928318
FEATURE [App::DocumentObjectGroupPython] G4_LEAD_OXIDE  # scripted group (container) (typed FeaturePython)
  Dunit = g/cm3
  Dvalue = 9.53
  Group = -> [O_element053,Pb_element002]
  conduct = 2
  density = 1
  expand = 3
  formula = G4_LEAD_OXIDE
  name = G4_LEAD_OXIDE
  specific = 4
FEATURE [App::DocumentObjectGroupPython] Li_element001  label="Li_element : 1"  # scripted group (container) (typed FeaturePython)
  n = 1
  ref = Li_element
FEATURE [App::DocumentObjectGroupPython] N_element022  label="N_element : 011"  # scripted group (container) (typed FeaturePython)
  n = 1
  ref = N_element
FEATURE [App::DocumentObjectGroupPython] H_element049  label="H_element : 026"  # scripted group (container) (typed FeaturePython)
  n = 2
  ref = H_element
FEATURE [App::DocumentObjectGroupPython] G4_LITHIUM_AMIDE  # scripted group (container) (typed FeaturePython)
  Dunit = g/cm3
  Dvalue = 1.178
  Group = -> [Li_element001,N_element022,H_element049]
  conduct = 2
  density = 1
  expand = 3
  formula = G4_LITHIUM_AMIDE
  name = G4_LITHIUM_AMIDE
  specific = 4
FEATURE [App::DocumentObjectGroupPython] Li_element002  label="Li_element : 2"  # scripted group (container) (typed FeaturePython)
  n = 2
  ref = Li_element
FEATURE [App::DocumentObjectGroupPython] C_element055  label="C_element : 030"  # scripted group (container) (typed FeaturePython)
  n = 1
  ref = C_element
FEATURE [App::DocumentObjectGroupPython] O_element054  label="O_element : 028"  # scripted group (container) (typed FeaturePython)
  n = 3
  ref = O_element
FEATURE [App::DocumentObjectGroupPython] G4_LITHIUM_CARBONATE  # scripted group (container) (typed FeaturePython)
  Dunit = g/cm3
  Dvalue = 2.11
  Group = -> [Li_element002,C_element055,O_element054]
  conduct = 2
  density = 1
  expand = 3
  formula = G4_LITHIUM_CARBONATE
  name = G4_LITHIUM_CARBONATE
  specific = 4
FEATURE [App::DocumentObjectGroupPython] Li_element003  label="Li_element : 003"  # scripted group (container) (typed FeaturePython)
  n = 1
  ref = Li_element
FEATURE [App::DocumentObjectGroupPython] F_element012  label="F_element : 004"  # scripted group (container) (typed FeaturePython)
  n = 1
  ref = F_element
FEATURE [App::DocumentObjectGroupPython] G4_LITHIUM_FLUORIDE  # scripted group (container) (typed FeaturePython)
  Dunit = g/cm3
  Dvalue = 2.635
  Group = -> [Li_element003,F_element012]
  conduct = 2
  density = 1
  expand = 3
  formula = G4_LITHIUM_FLUORIDE
  name = G4_LITHIUM_FLUORIDE
  specific = 4
FEATURE [App::DocumentObjectGroupPython] Li_element004  label="Li_element : 004"  # scripted group (container) (typed FeaturePython)
  n = 1
  ref = Li_element
FEATURE [App::DocumentObjectGroupPython] H_element050  label="H_element : 027"  # scripted group (container) (typed FeaturePython)
  n = 1
  ref = H_element
FEATURE [App::DocumentObjectGroupPython] G4_LITHIUM_HYDRIDE  # scripted group (container) (typed FeaturePython)
  Dunit = g/cm3
  Dvalue = 0.82
  Group = -> [Li_element004,H_element050]
  conduct = 2
  density = 1
  expand = 3
  formula = G4_LITHIUM_HYDRIDE
  name = G4_LITHIUM_HYDRIDE
  specific = 4
FEATURE [App::DocumentObjectGroupPython] Li_element005  label="Li_element : 005"  # scripted group (container) (typed FeaturePython)
  n = 1
  ref = Li_element
FEATURE [App::DocumentObjectGroupPython] I_element003  label="I_element : 002"  # scripted group (container) (typed FeaturePython)
  n = 1
  ref = I_element
FEATURE [App::DocumentObjectGroupPython] G4_LITHIUM_IODIDE  # scripted group (container) (typed FeaturePython)
  Dunit = g/cm3
  Dvalue = 3.494
  Group = -> [Li_element005,I_element003]
  conduct = 2
  density = 1
  expand = 3
  formula = G4_LITHIUM_IODIDE
  name = G4_LITHIUM_IODIDE
  specific = 4
FEATURE [App::DocumentObjectGroupPython] Li_element006  label="Li_element : 006"  # scripted group (container) (typed FeaturePython)
  n = 2
  ref = Li_element
FEATURE [App::DocumentObjectGroupPython] O_element055  label="O_element : 029"  # scripted group (container) (typed FeaturePython)
  n = 1
  ref = O_element
FEATURE [App::DocumentObjectGroupPython] G4_LITHIUM_OXIDE  # scripted group (container) (typed FeaturePython)
  Dunit = g/cm3
  Dvalue = 2.013
  Group = -> [Li_element006,O_element055]
  conduct = 2
  density = 1
  expand = 3
  formula = G4_LITHIUM_OXIDE
  name = G4_LITHIUM_OXIDE
  specific = 4
FEATURE [App::DocumentObjectGroupPython] Li_element007  label="Li_element : 007"  # scripted group (container) (typed FeaturePython)
  n = 2
  ref = Li_element
FEATURE [App::DocumentObjectGroupPython] B_element005  label="B_element : 005"  # scripted group (container) (typed FeaturePython)
  n = 4
  ref = B_element
FEATURE [App::DocumentObjectGroupPython] O_element056  label="O_element : 7"  # scripted group (container) (typed FeaturePython)
  n = 7
  ref = O_element
FEATURE [App::DocumentObjectGroupPython] G4_LITHIUM_TETRABORATE  # scripted group (container) (typed FeaturePython)
  Dunit = g/cm3
  Dvalue = 2.44
  Group = -> [Li_element007,B_element005,O_element056]
  conduct = 2
  density = 1
  expand = 3
  formula = G4_LITHIUM_TETRABORATE
  name = G4_LITHIUM_TETRABORATE
  specific = 4
FEATURE [App::DocumentObjectGroupPython] H_element051  label="H_element : 0.105"  # scripted group (container) (typed FeaturePython)
  n = 0.105
FEATURE [App::DocumentObjectGroupPython] C_element056  label="C_element : 0.083"  # scripted group (container) (typed FeaturePython)
  n = 0.083
FEATURE [App::DocumentObjectGroupPython] N_element023  label="N_element : 0.023"  # scripted group (container) (typed FeaturePython)
  n = 0.023
FEATURE [App::DocumentObjectGroupPython] O_element057  label="O_element : 0.779"  # scripted group (container) (typed FeaturePython)
  n = 0.779
FEATURE [App::DocumentObjectGroupPython] Na_element010  label="Na_element : 0.097"  # scripted group (container) (typed FeaturePython)
  n = 0.002
FEATURE [App::DocumentObjectGroupPython] P_element006  label="P_element : 0.105"  # scripted group (container) (typed FeaturePython)
  n = 0.001
FEATURE [App::DocumentObjectGroupPython] S_element016  label="S_element : 0.017"  # scripted group (container) (typed FeaturePython)
  n = 0.002
FEATURE [App::DocumentObjectGroupPython] Cl_element014  label="Cl_element : 0.587"  # scripted group (container) (typed FeaturePython)
  n = 0.003
FEATURE [App::DocumentObjectGroupPython] K_element005  label="K_element : 0.015"  # scripted group (container) (typed FeaturePython)
  n = 0.002
FEATURE [App::DocumentObjectGroupPython] G4_LUNG_ICRP  # scripted group (container) (typed FeaturePython)
  Dunit = g/cm3
  Dvalue = 1.04
  Group = -> [H_element051,C_element056,N_element023,O_element057,Na_element010,P_element006,S_element016,Cl_element014,K_element005]
  conduct = 2
  density = 1
  expand = 3
  formula = G4_LUNG_ICRP
  name = G4_LUNG_ICRP
  specific = 4
FEATURE [App::DocumentObjectGroupPython] H_element052  label="H_element : 0.116"  # scripted group (container) (typed FeaturePython)
  n = 0.114318
FEATURE [App::DocumentObjectGroupPython] C_element057  label="C_element : 0.656"  # scripted group (container) (typed FeaturePython)
  n = 0.655824
FEATURE [App::DocumentObjectGroupPython] O_element058  label="O_element : 0.092"  # scripted group (container) (typed FeaturePython)
  n = 0.0921831
FEATURE [App::DocumentObjectGroupPython] Mg_element004  label="Mg_element : 0.135"  # scripted group (container) (typed FeaturePython)
  n = 0.134792
FEATURE [App::DocumentObjectGroupPython] Ca_element013  label="Ca_element : 0.003"  # scripted group (container) (typed FeaturePython)
  n = 0.002883
FEATURE [App::DocumentObjectGroupPython] G4_M3_WAX  # scripted group (container) (typed FeaturePython)
  Dunit = g/cm3
  Dvalue = 1.05
  Group = -> [H_element052,C_element057,O_element058,Mg_element004,Ca_element013]
  conduct = 2
  density = 1
  expand = 3
  formula = G4_M3_WAX
  name = G4_M3_WAX
  specific = 4
FEATURE [App::DocumentObjectGroupPython] Mg_element005  label="Mg_element : 1"  # scripted group (container) (typed FeaturePython)
  n = 1
  ref = Mg_element
FEATURE [App::DocumentObjectGroupPython] C_element058  label="C_element : 031"  # scripted group (container) (typed FeaturePython)
  n = 1
  ref = C_element
FEATURE [App::DocumentObjectGroupPython] O_element059  label="O_element : 030"  # scripted group (container) (typed FeaturePython)
  n = 3
  ref = O_element
FEATURE [App::DocumentObjectGroupPython] G4_MAGNESIUM_CARBONATE  # scripted group (container) (typed FeaturePython)
  Dunit = g/cm3
  Dvalue = 2.958
  Group = -> [Mg_element005,C_element058,O_element059]
  conduct = 2
  density = 1
  expand = 3
  formula = G4_MAGNESIUM_CARBONATE
  name = G4_MAGNESIUM_CARBONATE
  specific = 4
FEATURE [App::DocumentObjectGroupPython] Mg_element006  label="Mg_element : 002"  # scripted group (container) (typed FeaturePython)
  n = 1
  ref = Mg_element
FEATURE [App::DocumentObjectGroupPython] F_element013  label="F_element : 005"  # scripted group (container) (typed FeaturePython)
  n = 2
  ref = F_element
FEATURE [App::DocumentObjectGroupPython] G4_MAGNESIUM_FLUORIDE  # scripted group (container) (typed FeaturePython)
  Dunit = g/cm3
  Dvalue = 3
  Group = -> [Mg_element006,F_element013]
  conduct = 2
  density = 1
  expand = 3
  formula = G4_MAGNESIUM_FLUORIDE
  name = G4_MAGNESIUM_FLUORIDE
  specific = 4
FEATURE [App::DocumentObjectGroupPython] Mg_element007  label="Mg_element : 003"  # scripted group (container) (typed FeaturePython)
  n = 1
  ref = Mg_element
FEATURE [App::DocumentObjectGroupPython] O_element060  label="O_element : 031"  # scripted group (container) (typed FeaturePython)
  n = 1
  ref = O_element
FEATURE [App::DocumentObjectGroupPython] G4_MAGNESIUM_OXIDE  # scripted group (container) (typed FeaturePython)
  Dunit = g/cm3
  Dvalue = 3.58
  Group = -> [Mg_element007,O_element060]
  conduct = 2
  density = 1
  expand = 3
  formula = G4_MAGNESIUM_OXIDE
  name = G4_MAGNESIUM_OXIDE
  specific = 4
FEATURE [App::DocumentObjectGroupPython] Mg_element008  label="Mg_element : 004"  # scripted group (container) (typed FeaturePython)
  n = 1
  ref = Mg_element
FEATURE [App::DocumentObjectGroupPython] B_element006  label="B_element : 006"  # scripted group (container) (typed FeaturePython)
  n = 4
  ref = B_element
FEATURE [App::DocumentObjectGroupPython] O_element061  label="O_element : 032"  # scripted group (container) (typed FeaturePython)
  n = 7
  ref = O_element
FEATURE [App::DocumentObjectGroupPython] G4_MAGNESIUM_TETRABORATE  # scripted group (container) (typed FeaturePython)
  Dunit = g/cm3
  Dvalue = 2.53
  Group = -> [Mg_element008,B_element006,O_element061]
  conduct = 2
  density = 1
  expand = 3
  formula = G4_MAGNESIUM_TETRABORATE
  name = G4_MAGNESIUM_TETRABORATE
  specific = 4
FEATURE [App::DocumentObjectGroupPython] Hg_element001  label="Hg_element : 1"  # scripted group (container) (typed FeaturePython)
  n = 1
  ref = Hg_element
FEATURE [App::DocumentObjectGroupPython] I_element004  label="I_element : 2"  # scripted group (container) (typed FeaturePython)
  n = 2
  ref = I_element
FEATURE [App::DocumentObjectGroupPython] G4_MERCURIC_IODIDE  # scripted group (container) (typed FeaturePython)
  Dunit = g/cm3
  Dvalue = 6.36
  Group = -> [Hg_element001,I_element004]
  conduct = 2
  density = 1
  expand = 3
  formula = G4_MERCURIC_IODIDE
  name = G4_MERCURIC_IODIDE
  specific = 4
FEATURE [App::DocumentObjectGroupPython] C_element059  label="C_element : 032"  # scripted group (container) (typed FeaturePython)
  n = 1
  ref = C_element
FEATURE [App::DocumentObjectGroupPython] H_element053  label="H_element : 028"  # scripted group (container) (typed FeaturePython)
  n = 4
  ref = H_element
FEATURE [App::DocumentObjectGroupPython] G4_METHANE  # scripted group (container) (typed FeaturePython)
  Dunit = g/cm3
  Dvalue = 0.000667151
  Group = -> [C_element059,H_element053]
  conduct = 2
  density = 1
  expand = 3
  formula = G4_METHANE
  name = G4_METHANE
  specific = 4
FEATURE [App::DocumentObjectGroupPython] C_element060  label="C_element : 033"  # scripted group (container) (typed FeaturePython)
  n = 1
  ref = C_element
FEATURE [App::DocumentObjectGroupPython] H_element054  label="H_element : 029"  # scripted group (container) (typed FeaturePython)
  n = 4
  ref = H_element
FEATURE [App::DocumentObjectGroupPython] O_element062  label="O_element : 033"  # scripted group (container) (typed FeaturePython)
  n = 1
  ref = O_element
FEATURE [App::DocumentObjectGroupPython] G4_METHANOL  # scripted group (container) (typed FeaturePython)
  Dunit = g/cm3
  Dvalue = 0.7914
  Group = -> [C_element060,H_element054,O_element062]
  conduct = 2
  density = 1
  expand = 3
  formula = G4_METHANOL
  name = G4_METHANOL
  specific = 4
FEATURE [App::DocumentObjectGroupPython] H_element055  label="H_element : 0.134"  # scripted group (container) (typed FeaturePython)
  n = 0.13404
FEATURE [App::DocumentObjectGroupPython] C_element061  label="C_element : 0.778"  # scripted group (container) (typed FeaturePython)
  n = 0.77796
FEATURE [App::DocumentObjectGroupPython] O_element063  label="O_element : 0.035"  # scripted group (container) (typed FeaturePython)
  n = 0.03502
FEATURE [App::DocumentObjectGroupPython] Mg_element009  label="Mg_element : 0.039"  # scripted group (container) (typed FeaturePython)
  n = 0.038594
FEATURE [App::DocumentObjectGroupPython] Ti_element002  label="Ti_element : 0.014"  # scripted group (container) (typed FeaturePython)
  n = 0.014386
FEATURE [App::DocumentObjectGroupPython] G4_MIX_D_WAX  # scripted group (container) (typed FeaturePython)
  Dunit = g/cm3
  Dvalue = 0.99
  Group = -> [H_element055,C_element061,O_element063,Mg_element009,Ti_element002]
  conduct = 2
  density = 1
  expand = 3
  formula = G4_MIX_D_WAX
  name = G4_MIX_D_WAX
  specific = 4
FEATURE [App::DocumentObjectGroupPython] H_element056  label="H_element : 0.135"  # scripted group (container) (typed FeaturePython)
  n = 0.081192
FEATURE [App::DocumentObjectGroupPython] C_element062  label="C_element : 0.583"  # scripted group (container) (typed FeaturePython)
  n = 0.583442
FEATURE [App::DocumentObjectGroupPython] N_element024  label="N_element : 0.018"  # scripted group (container) (typed FeaturePython)
  n = 0.017798
FEATURE [App::DocumentObjectGroupPython] O_element064  label="O_element : 0.186"  # scripted group (container) (typed FeaturePython)
  n = 0.186381
FEATURE [App::DocumentObjectGroupPython] Mg_element010  label="Mg_element : 0.130"  # scripted group (container) (typed FeaturePython)
  n = 0.130287
FEATURE [App::DocumentObjectGroupPython] Cl_element015  label="Cl_element : 0.588"  # scripted group (container) (typed FeaturePython)
  n = 0.0009
FEATURE [App::DocumentObjectGroupPython] G4_MS20_TISSUE  # scripted group (container) (typed FeaturePython)
  Dunit = g/cm3
  Dvalue = 1
  Group = -> [H_element056,C_element062,N_element024,O_element064,Mg_element010,Cl_element015]
  conduct = 2
  density = 1
  expand = 3
  formula = G4_MS20_TISSUE
  name = G4_MS20_TISSUE
  specific = 4
FEATURE [App::DocumentObjectGroupPython] H_element057  label="H_element : 0.136"  # scripted group (container) (typed FeaturePython)
  n = 0.102
FEATURE [App::DocumentObjectGroupPython] C_element063  label="C_element : 0.143"  # scripted group (container) (typed FeaturePython)
  n = 0.143
FEATURE [App::DocumentObjectGroupPython] N_element025  label="N_element : 0.034"  # scripted group (container) (typed FeaturePython)
  n = 0.034
FEATURE [App::DocumentObjectGroupPython] O_element065  label="O_element : 0.710"  # scripted group (container) (typed FeaturePython)
  n = 0.71
FEATURE [App::DocumentObjectGroupPython] Na_element011  label="Na_element : 0.098"  # scripted group (container) (typed FeaturePython)
  n = 0.001
FEATURE [App::DocumentObjectGroupPython] P_element007  label="P_element : 0.002"  # scripted group (container) (typed FeaturePython)
  n = 0.002
FEATURE [App::DocumentObjectGroupPython] S_element017  label="S_element : 0.018"  # scripted group (container) (typed FeaturePython)
  n = 0.003
FEATURE [App::DocumentObjectGroupPython] Cl_element016  label="Cl_element : 0.589"  # scripted group (container) (typed FeaturePython)
  n = 0.001
FEATURE [App::DocumentObjectGroupPython] K_element006  label="K_element : 0.004"  # scripted group (container) (typed FeaturePython)
  n = 0.004
FEATURE [App::DocumentObjectGroupPython] G4_MUSCLE_SKELETAL_ICRP  # scripted group (container) (typed FeaturePython)
  Dunit = g/cm3
  Dvalue = 1.05
  Group = -> [H_element057,C_element063,N_element025,O_element065,Na_element011,P_element007,S_element017,Cl_element016,K_element006]
  conduct = 2
  density = 1
  expand = 3
  formula = G4_MUSCLE_SKELETAL_ICRP
  name = G4_MUSCLE_SKELETAL_ICRP
  specific = 4
FEATURE [App::DocumentObjectGroupPython] H_element058  label="H_element : 0.137"  # scripted group (container) (typed FeaturePython)
  n = 0.102102
FEATURE [App::DocumentObjectGroupPython] C_element064  label="C_element : 0.123"  # scripted group (container) (typed FeaturePython)
  n = 0.123123
FEATURE [App::DocumentObjectGroupPython] N_element026  label="N_element : 0.756"  # scripted group (container) (typed FeaturePython)
  n = 0.035035
FEATURE [App::DocumentObjectGroupPython] O_element066  label="O_element : 0.730"  # scripted group (container) (typed FeaturePython)
  n = 0.72973
FEATURE [App::DocumentObjectGroupPython] Na_element012  label="Na_element : 0.099"  # scripted group (container) (typed FeaturePython)
  n = 0.001001
FEATURE [App::DocumentObjectGroupPython] P_element008  label="P_element : 0.106"  # scripted group (container) (typed FeaturePython)
  n = 0.002002
FEATURE [App::DocumentObjectGroupPython] S_element018  label="S_element : 0.019"  # scripted group (container) (typed FeaturePython)
  n = 0.004004
FEATURE [App::DocumentObjectGroupPython] K_element007  label="K_element : 0.016"  # scripted group (container) (typed FeaturePython)
  n = 0.003003
FEATURE [App::DocumentObjectGroupPython] G4_MUSCLE_STRIATED_ICRU  # scripted group (container) (typed FeaturePython)
  Dunit = g/cm3
  Dvalue = 1.04
  Group = -> [H_element058,C_element064,N_element026,O_element066,Na_element012,P_element008,S_element018,K_element007]
  conduct = 2
  density = 1
  expand = 3
  formula = G4_MUSCLE_STRIATED_ICRU
  name = G4_MUSCLE_STRIATED_ICRU
  specific = 4
FEATURE [App::DocumentObjectGroupPython] H_element059  label="H_element : 0.098"  # scripted group (container) (typed FeaturePython)
  n = 0.0982341
FEATURE [App::DocumentObjectGroupPython] C_element065  label="C_element : 0.156"  # scripted group (container) (typed FeaturePython)
  n = 0.156214
FEATURE [App::DocumentObjectGroupPython] N_element027  label="N_element : 0.757"  # scripted group (container) (typed FeaturePython)
  n = 0.035451
FEATURE [App::DocumentObjectGroupPython] O_element067  label="O_element : 0.880"  # scripted group (container) (typed FeaturePython)
  n = 0.710101
FEATURE [App::DocumentObjectGroupPython] G4_MUSCLE_WITH_SUCROSE  # scripted group (container) (typed FeaturePython)
  Dunit = g/cm3
  Dvalue = 1.11
  Group = -> [H_element059,C_element065,N_element027,O_element067]
  conduct = 2
  density = 1
  expand = 3
  formula = G4_MUSCLE_WITH_SUCROSE
  name = G4_MUSCLE_WITH_SUCROSE
  specific = 4
FEATURE [App::DocumentObjectGroupPython] H_element060  label="H_element : 0.138"  # scripted group (container) (typed FeaturePython)
  n = 0.101969
FEATURE [App::DocumentObjectGroupPython] C_element066  label="C_element : 0.120"  # scripted group (container) (typed FeaturePython)
  n = 0.120058
FEATURE [App::DocumentObjectGroupPython] N_element028  label="N_element : 0.758"  # scripted group (container) (typed FeaturePython)
  n = 0.035451
FEATURE [App::DocumentObjectGroupPython] O_element068  label="O_element : 0.743"  # scripted group (container) (typed FeaturePython)
  n = 0.742522
FEATURE [App::DocumentObjectGroupPython] G4_MUSCLE_WITHOUT_SUCROSE  # scripted group (container) (typed FeaturePython)
  Dunit = g/cm3
  Dvalue = 1.07
  Group = -> [H_element060,C_element066,N_element028,O_element068]
  conduct = 2
  density = 1
  expand = 3
  formula = G4_MUSCLE_WITHOUT_SUCROSE
  name = G4_MUSCLE_WITHOUT_SUCROSE
  specific = 4
FEATURE [App::DocumentObjectGroupPython] C_element067  label="C_element : 10"  # scripted group (container) (typed FeaturePython)
  n = 10
  ref = C_element
FEATURE [App::DocumentObjectGroupPython] H_element061  label="H_element : 030"  # scripted group (container) (typed FeaturePython)
  n = 8
  ref = H_element
FEATURE [App::DocumentObjectGroupPython] G4_NAPHTHALENE  # scripted group (container) (typed FeaturePython)
  Dunit = g/cm3
  Dvalue = 1.145
  Group = -> [C_element067,H_element061]
  conduct = 2
  density = 1
  expand = 3
  formula = G4_NAPHTHALENE
  name = G4_NAPHTHALENE
  specific = 4
FEATURE [App::DocumentObjectGroupPython] C_element068  label="C_element : 034"  # scripted group (container) (typed FeaturePython)
  n = 6
  ref = C_element
FEATURE [App::DocumentObjectGroupPython] H_element062  label="H_element : 031"  # scripted group (container) (typed FeaturePython)
  n = 5
  ref = H_element
FEATURE [App::DocumentObjectGroupPython] N_element029  label="N_element : 012"  # scripted group (container) (typed FeaturePython)
  n = 1
  ref = N_element
FEATURE [App::DocumentObjectGroupPython] O_element069  label="O_element : 034"  # scripted group (container) (typed FeaturePython)
  n = 2
  ref = O_element
FEATURE [App::DocumentObjectGroupPython] G4_NITROBENZENE  # scripted group (container) (typed FeaturePython)
  Dunit = g/cm3
  Dvalue = 1.19867
  Group = -> [C_element068,H_element062,N_element029,O_element069]
  conduct = 2
  density = 1
  expand = 3
  formula = G4_NITROBENZENE
  name = G4_NITROBENZENE
  specific = 4
FEATURE [App::DocumentObjectGroupPython] N_element030  label="N_element : 013"  # scripted group (container) (typed FeaturePython)
  n = 2
  ref = N_element
FEATURE [App::DocumentObjectGroupPython] O_element070  label="O_element : 035"  # scripted group (container) (typed FeaturePython)
  n = 1
  ref = O_element
FEATURE [App::DocumentObjectGroupPython] G4_NITROUS_OXIDE  # scripted group (container) (typed FeaturePython)
  Dunit = g/cm3
  Dvalue = 0.00183094
  Group = -> [N_element030,O_element070]
  conduct = 2
  density = 1
  expand = 3
  formula = G4_NITROUS_OXIDE
  name = G4_NITROUS_OXIDE
  specific = 4
FEATURE [App::DocumentObjectGroupPython] H_element063  label="H_element : 0.104"  # scripted group (container) (typed FeaturePython)
  n = 0.103509
FEATURE [App::DocumentObjectGroupPython] C_element069  label="C_element : 0.648"  # scripted group (container) (typed FeaturePython)
  n = 0.648416
FEATURE [App::DocumentObjectGroupPython] N_element031  label="N_element : 0.100"  # scripted group (container) (typed FeaturePython)
  n = 0.0995361
FEATURE [App::DocumentObjectGroupPython] O_element071  label="O_element : 0.149"  # scripted group (container) (typed FeaturePython)
  n = 0.148539
FEATURE [App::DocumentObjectGroupPython] G4_NYLON_8062  label="G4_NYLON-8062"  # scripted group (container) (typed FeaturePython)
  Dunit = g/cm3
  Dvalue = 1.08
  Group = -> [H_element063,C_element069,N_element031,O_element071]
  conduct = 2
  density = 1
  expand = 3
  formula = G4_NYLON-8062
  name = G4_NYLON-8062
  specific = 4
FEATURE [App::DocumentObjectGroupPython] C_element070  label="C_element : 035"  # scripted group (container) (typed FeaturePython)
  n = 6
  ref = C_element
FEATURE [App::DocumentObjectGroupPython] H_element064  label="H_element : 11"  # scripted group (container) (typed FeaturePython)
  n = 11
  ref = H_element
FEATURE [App::DocumentObjectGroupPython] N_element032  label="N_element : 014"  # scripted group (container) (typed FeaturePython)
  n = 1
  ref = N_element
FEATURE [App::DocumentObjectGroupPython] O_element072  label="O_element : 036"  # scripted group (container) (typed FeaturePython)
  n = 1
  ref = O_element
FEATURE [App::DocumentObjectGroupPython] G4_NYLON_6_6  label="G4_NYLON-6-6"  # scripted group (container) (typed FeaturePython)
  Dunit = g/cm3
  Dvalue = 1.14
  Group = -> [C_element070,H_element064,N_element032,O_element072]
  conduct = 2
  density = 1
  expand = 3
  formula = G4_NYLON-6-6
  name = G4_NYLON-6-6
  specific = 4
FEATURE [App::DocumentObjectGroupPython] H_element065  label="H_element : 0.139"  # scripted group (container) (typed FeaturePython)
  n = 0.107062
FEATURE [App::DocumentObjectGroupPython] C_element071  label="C_element : 0.680"  # scripted group (container) (typed FeaturePython)
  n = 0.680449
FEATURE [App::DocumentObjectGroupPython] N_element033  label="N_element : 0.099"  # scripted group (container) (typed FeaturePython)
  n = 0.099189
FEATURE [App::DocumentObjectGroupPython] O_element073  label="O_element : 0.113"  # scripted group (container) (typed FeaturePython)
  n = 0.1133
FEATURE [App::DocumentObjectGroupPython] G4_NYLON_6_10  label="G4_NYLON-6-10"  # scripted group (container) (typed FeaturePython)
  Dunit = g/cm3
  Dvalue = 1.14
  Group = -> [H_element065,C_element071,N_element033,O_element073]
  conduct = 2
  density = 1
  expand = 3
  formula = G4_NYLON-6-10
  name = G4_NYLON-6-10
  specific = 4
FEATURE [App::DocumentObjectGroupPython] H_element066  label="H_element : 0.140"  # scripted group (container) (typed FeaturePython)
  n = 0.115476
FEATURE [App::DocumentObjectGroupPython] C_element072  label="C_element : 0.721"  # scripted group (container) (typed FeaturePython)
  n = 0.720818
FEATURE [App::DocumentObjectGroupPython] N_element034  label="N_element : 0.076"  # scripted group (container) (typed FeaturePython)
  n = 0.0764169
FEATURE [App::DocumentObjectGroupPython] O_element074  label="O_element : 0.087"  # scripted group (container) (typed FeaturePython)
  n = 0.0872889
FEATURE [App::DocumentObjectGroupPython] G4_NYLON_11_RILSAN  label="G4_NYLON-11_RILSAN"  # scripted group (container) (typed FeaturePython)
  Dunit = g/cm3
  Dvalue = 1.425
  Group = -> [H_element066,C_element072,N_element034,O_element074]
  conduct = 2
  density = 1
  expand = 3
  formula = G4_NYLON-11_RILSAN
  name = G4_NYLON-11_RILSAN
  specific = 4
FEATURE [App::DocumentObjectGroupPython] C_element073  label="C_element : 8"  # scripted group (container) (typed FeaturePython)
  n = 8
  ref = C_element
FEATURE [App::DocumentObjectGroupPython] H_element067  label="H_element : 18"  # scripted group (container) (typed FeaturePython)
  n = 18
  ref = H_element
FEATURE [App::DocumentObjectGroupPython] G4_OCTANE  # scripted group (container) (typed FeaturePython)
  Dunit = g/cm3
  Dvalue = 0.7026
  Group = -> [C_element073,H_element067]
  conduct = 2
  density = 1
  expand = 3
  formula = G4_OCTANE
  name = G4_OCTANE
  specific = 4
FEATURE [App::DocumentObjectGroupPython] C_element074  label="C_element : 25"  # scripted group (container) (typed FeaturePython)
  n = 25
  ref = C_element
FEATURE [App::DocumentObjectGroupPython] H_element068  label="H_element : 52"  # scripted group (container) (typed FeaturePython)
  n = 52
  ref = H_element
FEATURE [App::DocumentObjectGroupPython] G4_PARAFFIN  # scripted group (container) (typed FeaturePython)
  Dunit = g/cm3
  Dvalue = 0.93
  Group = -> [C_element074,H_element068]
  conduct = 2
  density = 1
  expand = 3
  formula = G4_PARAFFIN
  name = G4_PARAFFIN
  specific = 4
FEATURE [App::DocumentObjectGroupPython] C_element075  label="C_element : 036"  # scripted group (container) (typed FeaturePython)
  n = 5
  ref = C_element
FEATURE [App::DocumentObjectGroupPython] H_element069  label="H_element : 032"  # scripted group (container) (typed FeaturePython)
  n = 12
  ref = H_element
FEATURE [App::DocumentObjectGroupPython] G4_N_PENTANE  label="G4_N-PENTANE"  # scripted group (container) (typed FeaturePython)
  Dunit = g/cm3
  Dvalue = 0.6262
  Group = -> [C_element075,H_element069]
  conduct = 2
  density = 1
  expand = 3
  formula = G4_N-PENTANE
  name = G4_N-PENTANE
  specific = 4
FEATURE [App::DocumentObjectGroupPython] H_element070  label="H_element : 0.014"  # scripted group (container) (typed FeaturePython)
  n = 0.0141
FEATURE [App::DocumentObjectGroupPython] C_element076  label="C_element : 0.072"  # scripted group (container) (typed FeaturePython)
  n = 0.072261
FEATURE [App::DocumentObjectGroupPython] N_element035  label="N_element : 0.019"  # scripted group (container) (typed FeaturePython)
  n = 0.01932
FEATURE [App::DocumentObjectGroupPython] O_element075  label="O_element : 0.066"  # scripted group (container) (typed FeaturePython)
  n = 0.066101
FEATURE [App::DocumentObjectGroupPython] S_element019  label="S_element : 0.020"  # scripted group (container) (typed FeaturePython)
  n = 0.00189
FEATURE [App::DocumentObjectGroupPython] Br_element004  label="Br_element : 0.349"  # scripted group (container) (typed FeaturePython)
  n = 0.349103
FEATURE [App::DocumentObjectGroupPython] Ag_element001  label="Ag_element : 0.474"  # scripted group (container) (typed FeaturePython)
  n = 0.474105
FEATURE [App::DocumentObjectGroupPython] I_element005  label="I_element : 0.003"  # scripted group (container) (typed FeaturePython)
  n = 0.00312
FEATURE [App::DocumentObjectGroupPython] G4_PHOTO_EMULSION  # scripted group (container) (typed FeaturePython)
  Dunit = g/cm3
  Dvalue = 3.815
  Group = -> [H_element070,C_element076,N_element035,O_element075,S_element019,Br_element004,Ag_element001,I_element005]
  conduct = 2
  density = 1
  expand = 3
  formula = G4_PHOTO_EMULSION
  name = G4_PHOTO_EMULSION
  specific = 4
FEATURE [App::DocumentObjectGroupPython] C_element077  label="C_element : 9"  # scripted group (container) (typed FeaturePython)
  n = 9
  ref = C_element
FEATURE [App::DocumentObjectGroupPython] H_element071  label="H_element : 033"  # scripted group (container) (typed FeaturePython)
  n = 10
  ref = H_element
FEATURE [App::DocumentObjectGroupPython] G4_PLASTIC_SC_VINYLTOLUENE  # scripted group (container) (typed FeaturePython)
  Dunit = g/cm3
  Dvalue = 1.032
  Group = -> [C_element077,H_element071]
  conduct = 2
  density = 1
  expand = 3
  formula = G4_PLASTIC_SC_VINYLTOLUENE
  name = G4_PLASTIC_SC_VINYLTOLUENE
  specific = 4
FEATURE [App::DocumentObjectGroupPython] Pu_element001  label="Pu_element : 1"  # scripted group (container) (typed FeaturePython)
  n = 1
  ref = Pu_element
FEATURE [App::DocumentObjectGroupPython] O_element076  label="O_element : 037"  # scripted group (container) (typed FeaturePython)
  n = 2
  ref = O_element
FEATURE [App::DocumentObjectGroupPython] G4_PLUTONIUM_DIOXIDE  # scripted group (container) (typed FeaturePython)
  Dunit = g/cm3
  Dvalue = 11.46
  Group = -> [Pu_element001,O_element076]
  conduct = 2
  density = 1
  expand = 3
  formula = G4_PLUTONIUM_DIOXIDE
  name = G4_PLUTONIUM_DIOXIDE
  specific = 4
FEATURE [App::DocumentObjectGroupPython] C_element078  label="C_element : 037"  # scripted group (container) (typed FeaturePython)
  n = 3
  ref = C_element
FEATURE [App::DocumentObjectGroupPython] H_element072  label="H_element : 034"  # scripted group (container) (typed FeaturePython)
  n = 3
  ref = H_element
FEATURE [App::DocumentObjectGroupPython] N_element036  label="N_element : 015"  # scripted group (container) (typed FeaturePython)
  n = 1
  ref = N_element
FEATURE [App::DocumentObjectGroupPython] G4_POLYACRYLONITRILE  # scripted group (container) (typed FeaturePython)
  Dunit = g/cm3
  Dvalue = 1.17
  Group = -> [C_element078,H_element072,N_element036]
  conduct = 2
  density = 1
  expand = 3
  formula = G4_POLYACRYLONITRILE
  name = G4_POLYACRYLONITRILE
  specific = 4
FEATURE [App::DocumentObjectGroupPython] C_element079  label="C_element : 16"  # scripted group (container) (typed FeaturePython)
  n = 16
  ref = C_element
FEATURE [App::DocumentObjectGroupPython] H_element073  label="H_element : 035"  # scripted group (container) (typed FeaturePython)
  n = 14
  ref = H_element
FEATURE [App::DocumentObjectGroupPython] O_element077  label="O_element : 038"  # scripted group (container) (typed FeaturePython)
  n = 3
  ref = O_element
FEATURE [App::DocumentObjectGroupPython] G4_POLYCARBONATE  # scripted group (container) (typed FeaturePython)
  Dunit = g/cm3
  Dvalue = 1.2
  Group = -> [C_element079,H_element073,O_element077]
  conduct = 2
  density = 1
  expand = 3
  formula = G4_POLYCARBONATE
  name = G4_POLYCARBONATE
  specific = 4
FEATURE [App::DocumentObjectGroupPython] C_element080  label="C_element : 038"  # scripted group (container) (typed FeaturePython)
  n = 8
  ref = C_element
FEATURE [App::DocumentObjectGroupPython] H_element074  label="H_element : 036"  # scripted group (container) (typed FeaturePython)
  n = 7
  ref = H_element
FEATURE [App::DocumentObjectGroupPython] Cl_element017  label="Cl_element : 007"  # scripted group (container) (typed FeaturePython)
  n = 1
  ref = Cl_element
FEATURE [App::DocumentObjectGroupPython] G4_POLYCHLOROSTYRENE  # scripted group (container) (typed FeaturePython)
  Dunit = g/cm3
  Dvalue = 1.3
  Group = -> [C_element080,H_element074,Cl_element017]
  conduct = 2
  density = 1
  expand = 3
  formula = G4_POLYCHLOROSTYRENE
  name = G4_POLYCHLOROSTYRENE
  specific = 4
FEATURE [App::DocumentObjectGroupPython] C_element081  label="C_element : 039"  # scripted group (container) (typed FeaturePython)
  n = 1
  ref = C_element
FEATURE [App::DocumentObjectGroupPython] H_element075  label="H_element : 037"  # scripted group (container) (typed FeaturePython)
  n = 2
  ref = H_element
FEATURE [App::DocumentObjectGroupPython] G4_POLYETHYLENE  # scripted group (container) (typed FeaturePython)
  Dunit = g/cm3
  Dvalue = 0.94
  Group = -> [C_element081,H_element075]
  conduct = 2
  density = 1
  expand = 3
  formula = G4_POLYETHYLENE
  name = G4_POLYETHYLENE
  specific = 4
FEATURE [App::DocumentObjectGroupPython] C_element082  label="C_element : 040"  # scripted group (container) (typed FeaturePython)
  n = 10
  ref = C_element
FEATURE [App::DocumentObjectGroupPython] H_element076  label="H_element : 038"  # scripted group (container) (typed FeaturePython)
  n = 8
  ref = H_element
FEATURE [App::DocumentObjectGroupPython] O_element078  label="O_element : 039"  # scripted group (container) (typed FeaturePython)
  n = 4
  ref = O_element
FEATURE [App::DocumentObjectGroupPython] G4_MYLAR  # scripted group (container) (typed FeaturePython)
  Dunit = g/cm3
  Dvalue = 1.4
  Group = -> [C_element082,H_element076,O_element078]
  conduct = 2
  density = 1
  expand = 3
  formula = G4_MYLAR
  name = G4_MYLAR
  specific = 4
FEATURE [App::DocumentObjectGroupPython] C_element083  label="C_element : 041"  # scripted group (container) (typed FeaturePython)
  n = 5
  ref = C_element
FEATURE [App::DocumentObjectGroupPython] H_element077  label="H_element : 039"  # scripted group (container) (typed FeaturePython)
  n = 8
  ref = H_element
FEATURE [App::DocumentObjectGroupPython] O_element079  label="O_element : 040"  # scripted group (container) (typed FeaturePython)
  n = 2
  ref = O_element
FEATURE [App::DocumentObjectGroupPython] G4_PLEXIGLASS  # scripted group (container) (typed FeaturePython)
  Dunit = g/cm3
  Dvalue = 1.19
  Group = -> [C_element083,H_element077,O_element079]
  conduct = 2
  density = 1
  expand = 3
  formula = G4_PLEXIGLASS
  name = G4_PLEXIGLASS
  specific = 4
FEATURE [App::DocumentObjectGroupPython] C_element084  label="C_element : 042"  # scripted group (container) (typed FeaturePython)
  n = 1
  ref = C_element
FEATURE [App::DocumentObjectGroupPython] H_element078  label="H_element : 040"  # scripted group (container) (typed FeaturePython)
  n = 2
  ref = H_element
FEATURE [App::DocumentObjectGroupPython] O_element080  label="O_element : 041"  # scripted group (container) (typed FeaturePython)
  n = 1
  ref = O_element
FEATURE [App::DocumentObjectGroupPython] G4_POLYOXYMETHYLENE  # scripted group (container) (typed FeaturePython)
  Dunit = g/cm3
  Dvalue = 1.425
  Group = -> [C_element084,H_element078,O_element080]
  conduct = 2
  density = 1
  expand = 3
  formula = G4_POLYOXYMETHYLENE
  name = G4_POLYOXYMETHYLENE
  specific = 4
FEATURE [App::DocumentObjectGroupPython] C_element085  label="C_element : 043"  # scripted group (container) (typed FeaturePython)
  n = 2
  ref = C_element
FEATURE [App::DocumentObjectGroupPython] H_element079  label="H_element : 041"  # scripted group (container) (typed FeaturePython)
  n = 4
  ref = H_element
FEATURE [App::DocumentObjectGroupPython] G4_POLYPROPYLENE  # scripted group (container) (typed FeaturePython)
  Dunit = g/cm3
  Dvalue = 0.9
  Group = -> [C_element085,H_element079]
  conduct = 2
  density = 1
  expand = 3
  formula = G4_POLYPROPYLENE
  name = G4_POLYPROPYLENE
  specific = 4
FEATURE [App::DocumentObjectGroupPython] C_element086  label="C_element : 044"  # scripted group (container) (typed FeaturePython)
  n = 8
  ref = C_element
FEATURE [App::DocumentObjectGroupPython] H_element080  label="H_element : 042"  # scripted group (container) (typed FeaturePython)
  n = 8
  ref = H_element
FEATURE [App::DocumentObjectGroupPython] G4_POLYSTYRENE  # scripted group (container) (typed FeaturePython)
  Dunit = g/cm3
  Dvalue = 1.06
  Group = -> [C_element086,H_element080]
  conduct = 2
  density = 1
  expand = 3
  formula = G4_POLYSTYRENE
  name = G4_POLYSTYRENE
  specific = 4
FEATURE [App::DocumentObjectGroupPython] C_element087  label="C_element : 045"  # scripted group (container) (typed FeaturePython)
  n = 2
  ref = C_element
FEATURE [App::DocumentObjectGroupPython] F_element014  label="F_element : 4"  # scripted group (container) (typed FeaturePython)
  n = 4
  ref = F_element
FEATURE [App::DocumentObjectGroupPython] G4_TEFLON  # scripted group (container) (typed FeaturePython)
  Dunit = g/cm3
  Dvalue = 2.2
  Group = -> [C_element087,F_element014]
  conduct = 2
  density = 1
  expand = 3
  formula = G4_TEFLON
  name = G4_TEFLON
  specific = 4
FEATURE [App::DocumentObjectGroupPython] C_element088  label="C_element : 046"  # scripted group (container) (typed FeaturePython)
  n = 2
  ref = C_element
FEATURE [App::DocumentObjectGroupPython] F_element015  label="F_element : 006"  # scripted group (container) (typed FeaturePython)
  n = 3
  ref = F_element
FEATURE [App::DocumentObjectGroupPython] Cl_element018  label="Cl_element : 008"  # scripted group (container) (typed FeaturePython)
  n = 1
  ref = Cl_element
FEATURE [App::DocumentObjectGroupPython] G4_POLYTRIFLUOROCHLOROETHYLENE  # scripted group (container) (typed FeaturePython)
  Dunit = g/cm3
  Dvalue = 2.1
  Group = -> [C_element088,F_element015,Cl_element018]
  conduct = 2
  density = 1
  expand = 3
  formula = G4_POLYTRIFLUOROCHLOROETHYLENE
  name = G4_POLYTRIFLUOROCHLOROETHYLENE
  specific = 4
FEATURE [App::DocumentObjectGroupPython] C_element089  label="C_element : 047"  # scripted group (container) (typed FeaturePython)
  n = 4
  ref = C_element
FEATURE [App::DocumentObjectGroupPython] H_element081  label="H_element : 043"  # scripted group (container) (typed FeaturePython)
  n = 6
  ref = H_element
FEATURE [App::DocumentObjectGroupPython] O_element081  label="O_element : 042"  # scripted group (container) (typed FeaturePython)
  n = 2
  ref = O_element
FEATURE [App::DocumentObjectGroupPython] G4_POLYVINYL_ACETATE  # scripted group (container) (typed FeaturePython)
  Dunit = g/cm3
  Dvalue = 1.19
  Group = -> [C_element089,H_element081,O_element081]
  conduct = 2
  density = 1
  expand = 3
  formula = G4_POLYVINYL_ACETATE
  name = G4_POLYVINYL_ACETATE
  specific = 4
FEATURE [App::DocumentObjectGroupPython] C_element090  label="C_element : 048"  # scripted group (container) (typed FeaturePython)
  n = 2
  ref = C_element
FEATURE [App::DocumentObjectGroupPython] H_element082  label="H_element : 044"  # scripted group (container) (typed FeaturePython)
  n = 4
  ref = H_element
FEATURE [App::DocumentObjectGroupPython] O_element082  label="O_element : 043"  # scripted group (container) (typed FeaturePython)
  n = 1
  ref = O_element
FEATURE [App::DocumentObjectGroupPython] G4_POLYVINYL_ALCOHOL  # scripted group (container) (typed FeaturePython)
  Dunit = g/cm3
  Dvalue = 1.3
  Group = -> [C_element090,H_element082,O_element082]
  conduct = 2
  density = 1
  expand = 3
  formula = G4_POLYVINYL_ALCOHOL
  name = G4_POLYVINYL_ALCOHOL
  specific = 4
FEATURE [App::DocumentObjectGroupPython] C_element091  label="C_element : 049"  # scripted group (container) (typed FeaturePython)
  n = 8
  ref = C_element
FEATURE [App::DocumentObjectGroupPython] H_element083  label="H_element : 045"  # scripted group (container) (typed FeaturePython)
  n = 14
  ref = H_element
FEATURE [App::DocumentObjectGroupPython] O_element083  label="O_element : 044"  # scripted group (container) (typed FeaturePython)
  n = 2
  ref = O_element
FEATURE [App::DocumentObjectGroupPython] G4_POLYVINYL_BUTYRAL  # scripted group (container) (typed FeaturePython)
  Dunit = g/cm3
  Dvalue = 1.12
  Group = -> [C_element091,H_element083,O_element083]
  conduct = 2
  density = 1
  expand = 3
  formula = G4_POLYVINYL_BUTYRAL
  name = G4_POLYVINYL_BUTYRAL
  specific = 4
FEATURE [App::DocumentObjectGroupPython] C_element092  label="C_element : 050"  # scripted group (container) (typed FeaturePython)
  n = 2
  ref = C_element
FEATURE [App::DocumentObjectGroupPython] H_element084  label="H_element : 046"  # scripted group (container) (typed FeaturePython)
  n = 3
  ref = H_element
FEATURE [App::DocumentObjectGroupPython] Cl_element019  label="Cl_element : 009"  # scripted group (container) (typed FeaturePython)
  n = 1
  ref = Cl_element
FEATURE [App::DocumentObjectGroupPython] G4_POLYVINYL_CHLORIDE  # scripted group (container) (typed FeaturePython)
  Dunit = g/cm3
  Dvalue = 1.3
  Group = -> [C_element092,H_element084,Cl_element019]
  conduct = 2
  density = 1
  expand = 3
  formula = G4_POLYVINYL_CHLORIDE
  name = G4_POLYVINYL_CHLORIDE
  specific = 4
FEATURE [App::DocumentObjectGroupPython] C_element093  label="C_element : 051"  # scripted group (container) (typed FeaturePython)
  n = 2
  ref = C_element
FEATURE [App::DocumentObjectGroupPython] H_element085  label="H_element : 047"  # scripted group (container) (typed FeaturePython)
  n = 2
  ref = H_element
FEATURE [App::DocumentObjectGroupPython] Cl_element020  label="Cl_element : 010"  # scripted group (container) (typed FeaturePython)
  n = 2
  ref = Cl_element
FEATURE [App::DocumentObjectGroupPython] G4_POLYVINYLIDENE_CHLORIDE  # scripted group (container) (typed FeaturePython)
  Dunit = g/cm3
  Dvalue = 1.7
  Group = -> [C_element093,H_element085,Cl_element020]
  conduct = 2
  density = 1
  expand = 3
  formula = G4_POLYVINYLIDENE_CHLORIDE
  name = G4_POLYVINYLIDENE_CHLORIDE
  specific = 4
FEATURE [App::DocumentObjectGroupPython] C_element094  label="C_element : 052"  # scripted group (container) (typed FeaturePython)
  n = 2
  ref = C_element
FEATURE [App::DocumentObjectGroupPython] H_element086  label="H_element : 048"  # scripted group (container) (typed FeaturePython)
  n = 2
  ref = H_element
FEATURE [App::DocumentObjectGroupPython] F_element016  label="F_element : 007"  # scripted group (container) (typed FeaturePython)
  n = 2
  ref = F_element
FEATURE [App::DocumentObjectGroupPython] G4_POLYVINYLIDENE_FLUORIDE  # scripted group (container) (typed FeaturePython)
  Dunit = g/cm3
  Dvalue = 1.76
  Group = -> [C_element094,H_element086,F_element016]
  conduct = 2
  density = 1
  expand = 3
  formula = G4_POLYVINYLIDENE_FLUORIDE
  name = G4_POLYVINYLIDENE_FLUORIDE
  specific = 4
FEATURE [App::DocumentObjectGroupPython] C_element095  label="C_element : 053"  # scripted group (container) (typed FeaturePython)
  n = 6
  ref = C_element
FEATURE [App::DocumentObjectGroupPython] H_element087  label="H_element : 9"  # scripted group (container) (typed FeaturePython)
  n = 9
  ref = H_element
FEATURE [App::DocumentObjectGroupPython] N_element037  label="N_element : 016"  # scripted group (container) (typed FeaturePython)
  n = 1
  ref = N_element
FEATURE [App::DocumentObjectGroupPython] O_element084  label="O_element : 045"  # scripted group (container) (typed FeaturePython)
  n = 1
  ref = O_element
FEATURE [App::DocumentObjectGroupPython] G4_POLYVINYL_PYRROLIDONE  # scripted group (container) (typed FeaturePython)
  Dunit = g/cm3
  Dvalue = 1.25
  Group = -> [C_element095,H_element087,N_element037,O_element084]
  conduct = 2
  density = 1
  expand = 3
  formula = G4_POLYVINYL_PYRROLIDONE
  name = G4_POLYVINYL_PYRROLIDONE
  specific = 4
FEATURE [App::DocumentObjectGroupPython] K_element008  label="K_element : 1"  # scripted group (container) (typed FeaturePython)
  n = 1
  ref = K_element
FEATURE [App::DocumentObjectGroupPython] I_element006  label="I_element : 003"  # scripted group (container) (typed FeaturePython)
  n = 1
  ref = I_element
FEATURE [App::DocumentObjectGroupPython] G4_POTASSIUM_IODIDE  # scripted group (container) (typed FeaturePython)
  Dunit = g/cm3
  Dvalue = 3.13
  Group = -> [K_element008,I_element006]
  conduct = 2
  density = 1
  expand = 3
  formula = G4_POTASSIUM_IODIDE
  name = G4_POTASSIUM_IODIDE
  specific = 4
FEATURE [App::DocumentObjectGroupPython] K_element009  label="K_element : 2"  # scripted group (container) (typed FeaturePython)
  n = 2
  ref = K_element
FEATURE [App::DocumentObjectGroupPython] O_element085  label="O_element : 046"  # scripted group (container) (typed FeaturePython)
  n = 1
  ref = O_element
FEATURE [App::DocumentObjectGroupPython] G4_POTASSIUM_OXIDE  # scripted group (container) (typed FeaturePython)
  Dunit = g/cm3
  Dvalue = 2.32
  Group = -> [K_element009,O_element085]
  conduct = 2
  density = 1
  expand = 3
  formula = G4_POTASSIUM_OXIDE
  name = G4_POTASSIUM_OXIDE
  specific = 4
FEATURE [App::DocumentObjectGroupPython] C_element096  label="C_element : 054"  # scripted group (container) (typed FeaturePython)
  n = 3
  ref = C_element
FEATURE [App::DocumentObjectGroupPython] H_element088  label="H_element : 049"  # scripted group (container) (typed FeaturePython)
  n = 8
  ref = H_element
FEATURE [App::DocumentObjectGroupPython] G4_PROPANE  # scripted group (container) (typed FeaturePython)
  Dunit = g/cm3
  Dvalue = 0.00187939
  Group = -> [C_element096,H_element088]
  conduct = 2
  density = 1
  expand = 3
  formula = G4_PROPANE
  name = G4_PROPANE
  specific = 4
FEATURE [App::DocumentObjectGroupPython] C_element097  label="C_element : 055"  # scripted group (container) (typed FeaturePython)
  n = 3
  ref = C_element
FEATURE [App::DocumentObjectGroupPython] H_element089  label="H_element : 050"  # scripted group (container) (typed FeaturePython)
  n = 8
  ref = H_element
FEATURE [App::DocumentObjectGroupPython] G4_lPROPANE  # scripted group (container) (typed FeaturePython)
  Dunit = g/cm3
  Dvalue = 0.43
  Group = -> [C_element097,H_element089]
  conduct = 2
  density = 1
  expand = 3
  formula = G4_lPROPANE
  name = G4_lPROPANE
  specific = 4
FEATURE [App::DocumentObjectGroupPython] C_element098  label="C_element : 056"  # scripted group (container) (typed FeaturePython)
  n = 3
  ref = C_element
FEATURE [App::DocumentObjectGroupPython] H_element090  label="H_element : 051"  # scripted group (container) (typed FeaturePython)
  n = 8
  ref = H_element
FEATURE [App::DocumentObjectGroupPython] O_element086  label="O_element : 047"  # scripted group (container) (typed FeaturePython)
  n = 1
  ref = O_element
FEATURE [App::DocumentObjectGroupPython] G4_N_PROPYL_ALCOHOL  label="G4_N-PROPYL_ALCOHOL"  # scripted group (container) (typed FeaturePython)
  Dunit = g/cm3
  Dvalue = 0.8035
  Group = -> [C_element098,H_element090,O_element086]
  conduct = 2
  density = 1
  expand = 3
  formula = G4_N-PROPYL_ALCOHOL
  name = G4_N-PROPYL_ALCOHOL
  specific = 4
FEATURE [App::DocumentObjectGroupPython] C_element099  label="C_element : 057"  # scripted group (container) (typed FeaturePython)
  n = 5
  ref = C_element
FEATURE [App::DocumentObjectGroupPython] H_element091  label="H_element : 052"  # scripted group (container) (typed FeaturePython)
  n = 5
  ref = H_element
FEATURE [App::DocumentObjectGroupPython] N_element038  label="N_element : 017"  # scripted group (container) (typed FeaturePython)
  n = 1
  ref = N_element
FEATURE [App::DocumentObjectGroupPython] G4_PYRIDINE  # scripted group (container) (typed FeaturePython)
  Dunit = g/cm3
  Dvalue = 0.9819
  Group = -> [C_element099,H_element091,N_element038]
  conduct = 2
  density = 1
  expand = 3
  formula = G4_PYRIDINE
  name = G4_PYRIDINE
  specific = 4
FEATURE [App::DocumentObjectGroupPython] H_element092  label="H_element : 0.144"  # scripted group (container) (typed FeaturePython)
  n = 0.143711
FEATURE [App::DocumentObjectGroupPython] C_element100  label="C_element : 0.856"  # scripted group (container) (typed FeaturePython)
  n = 0.856289
FEATURE [App::DocumentObjectGroupPython] G4_RUBBER_BUTYL  # scripted group (container) (typed FeaturePython)
  Dunit = g/cm3
  Dvalue = 0.92
  Group = -> [H_element092,C_element100]
  conduct = 2
  density = 1
  expand = 3
  formula = G4_RUBBER_BUTYL
  name = G4_RUBBER_BUTYL
  specific = 4
FEATURE [App::DocumentObjectGroupPython] H_element093  label="H_element : 0.118"  # scripted group (container) (typed FeaturePython)
  n = 0.118371
FEATURE [App::DocumentObjectGroupPython] C_element101  label="C_element : 0.882"  # scripted group (container) (typed FeaturePython)
  n = 0.881629
FEATURE [App::DocumentObjectGroupPython] G4_RUBBER_NATURAL  # scripted group (container) (typed FeaturePython)
  Dunit = g/cm3
  Dvalue = 0.92
  Group = -> [H_element093,C_element101]
  conduct = 2
  density = 1
  expand = 3
  formula = G4_RUBBER_NATURAL
  name = G4_RUBBER_NATURAL
  specific = 4
FEATURE [App::DocumentObjectGroupPython] H_element094  label="H_element : 0.145"  # scripted group (container) (typed FeaturePython)
  n = 0.05692
FEATURE [App::DocumentObjectGroupPython] C_element102  label="C_element : 0.543"  # scripted group (container) (typed FeaturePython)
  n = 0.542646
FEATURE [App::DocumentObjectGroupPython] Cl_element021  label="Cl_element : 0.400"  # scripted group (container) (typed FeaturePython)
  n = 0.400434
FEATURE [App::DocumentObjectGroupPython] G4_RUBBER_NEOPRENE  # scripted group (container) (typed FeaturePython)
  Dunit = g/cm3
  Dvalue = 1.23
  Group = -> [H_element094,C_element102,Cl_element021]
  conduct = 2
  density = 1
  expand = 3
  formula = G4_RUBBER_NEOPRENE
  name = G4_RUBBER_NEOPRENE
  specific = 4
FEATURE [App::DocumentObjectGroupPython] Si_element006  label="Si_element : 1"  # scripted group (container) (typed FeaturePython)
  n = 1
  ref = Si_element
FEATURE [App::DocumentObjectGroupPython] O_element087  label="O_element : 048"  # scripted group (container) (typed FeaturePython)
  n = 2
  ref = O_element
FEATURE [App::DocumentObjectGroupPython] G4_SILICON_DIOXIDE  # scripted group (container) (typed FeaturePython)
  Dunit = g/cm3
  Dvalue = 2.32
  Group = -> [Si_element006,O_element087]
  conduct = 2
  density = 1
  expand = 3
  formula = G4_SILICON_DIOXIDE
  name = G4_SILICON_DIOXIDE
  specific = 4
FEATURE [App::DocumentObjectGroupPython] Ag_element002  label="Ag_element : 1"  # scripted group (container) (typed FeaturePython)
  n = 1
  ref = Ag_element
FEATURE [App::DocumentObjectGroupPython] Br_element005  label="Br_element : 003"  # scripted group (container) (typed FeaturePython)
  n = 1
  ref = Br_element
FEATURE [App::DocumentObjectGroupPython] G4_SILVER_BROMIDE  # scripted group (container) (typed FeaturePython)
  Dunit = g/cm3
  Dvalue = 6.473
  Group = -> [Ag_element002,Br_element005]
  conduct = 2
  density = 1
  expand = 3
  formula = G4_SILVER_BROMIDE
  name = G4_SILVER_BROMIDE
  specific = 4
FEATURE [App::DocumentObjectGroupPython] Ag_element003  label="Ag_element : 002"  # scripted group (container) (typed FeaturePython)
  n = 1
  ref = Ag_element
FEATURE [App::DocumentObjectGroupPython] Cl_element022  label="Cl_element : 011"  # scripted group (container) (typed FeaturePython)
  n = 1
  ref = Cl_element
FEATURE [App::DocumentObjectGroupPython] G4_SILVER_CHLORIDE  # scripted group (container) (typed FeaturePython)
  Dunit = g/cm3
  Dvalue = 5.56
  Group = -> [Ag_element003,Cl_element022]
  conduct = 2
  density = 1
  expand = 3
  formula = G4_SILVER_CHLORIDE
  name = G4_SILVER_CHLORIDE
  specific = 4
FEATURE [App::DocumentObjectGroupPython] Br_element006  label="Br_element : 0.423"  # scripted group (container) (typed FeaturePython)
  n = 0.422895
FEATURE [App::DocumentObjectGroupPython] Ag_element004  label="Ag_element : 0.574"  # scripted group (container) (typed FeaturePython)
  n = 0.573748
FEATURE [App::DocumentObjectGroupPython] I_element007  label="I_element : 0.649"  # scripted group (container) (typed FeaturePython)
  n = 0.003357
FEATURE [App::DocumentObjectGroupPython] G4_SILVER_HALIDES  # scripted group (container) (typed FeaturePython)
  Dunit = g/cm3
  Dvalue = 6.47
  Group = -> [Br_element006,Ag_element004,I_element007]
  conduct = 2
  density = 1
  expand = 3
  formula = G4_SILVER_HALIDES
  name = G4_SILVER_HALIDES
  specific = 4
FEATURE [App::DocumentObjectGroupPython] Ag_element005  label="Ag_element : 003"  # scripted group (container) (typed FeaturePython)
  n = 1
  ref = Ag_element
FEATURE [App::DocumentObjectGroupPython] I_element008  label="I_element : 004"  # scripted group (container) (typed FeaturePython)
  n = 1
  ref = I_element
FEATURE [App::DocumentObjectGroupPython] G4_SILVER_IODIDE  # scripted group (container) (typed FeaturePython)
  Dunit = g/cm3
  Dvalue = 6.01
  Group = -> [Ag_element005,I_element008]
  conduct = 2
  density = 1
  expand = 3
  formula = G4_SILVER_IODIDE
  name = G4_SILVER_IODIDE
  specific = 4
FEATURE [App::DocumentObjectGroupPython] H_element095  label="H_element : 0.100"  # scripted group (container) (typed FeaturePython)
  n = 0.1
FEATURE [App::DocumentObjectGroupPython] C_element103  label="C_element : 0.204"  # scripted group (container) (typed FeaturePython)
  n = 0.204
FEATURE [App::DocumentObjectGroupPython] N_element039  label="N_element : 0.759"  # scripted group (container) (typed FeaturePython)
  n = 0.042
FEATURE [App::DocumentObjectGroupPython] O_element088  label="O_element : 0.645"  # scripted group (container) (typed FeaturePython)
  n = 0.645
FEATURE [App::DocumentObjectGroupPython] Na_element013  label="Na_element : 0.100"  # scripted group (container) (typed FeaturePython)
  n = 0.002
FEATURE [App::DocumentObjectGroupPython] P_element009  label="P_element : 0.107"  # scripted group (container) (typed FeaturePython)
  n = 0.001
FEATURE [App::DocumentObjectGroupPython] S_element020  label="S_element : 0.021"  # scripted group (container) (typed FeaturePython)
  n = 0.002
FEATURE [App::DocumentObjectGroupPython] Cl_element023  label="Cl_element : 0.590"  # scripted group (container) (typed FeaturePython)
  n = 0.003
FEATURE [App::DocumentObjectGroupPython] K_element010  label="K_element : 0.001"  # scripted group (container) (typed FeaturePython)
  n = 0.001
FEATURE [App::DocumentObjectGroupPython] G4_SKIN_ICRP  # scripted group (container) (typed FeaturePython)
  Dunit = g/cm3
  Dvalue = 1.09
  Group = -> [H_element095,C_element103,N_element039,O_element088,Na_element013,P_element009,S_element020,Cl_element023,K_element010]
  conduct = 2
  density = 1
  expand = 3
  formula = G4_SKIN_ICRP
  name = G4_SKIN_ICRP
  specific = 4
FEATURE [App::DocumentObjectGroupPython] Na_element014  label="Na_element : 2"  # scripted group (container) (typed FeaturePython)
  n = 2
  ref = Na_element
FEATURE [App::DocumentObjectGroupPython] C_element104  label="C_element : 058"  # scripted group (container) (typed FeaturePython)
  n = 1
  ref = C_element
FEATURE [App::DocumentObjectGroupPython] O_element089  label="O_element : 049"  # scripted group (container) (typed FeaturePython)
  n = 3
  ref = O_element
FEATURE [App::DocumentObjectGroupPython] G4_SODIUM_CARBONATE  # scripted group (container) (typed FeaturePython)
  Dunit = g/cm3
  Dvalue = 2.532
  Group = -> [Na_element014,C_element104,O_element089]
  conduct = 2
  density = 1
  expand = 3
  formula = G4_SODIUM_CARBONATE
  name = G4_SODIUM_CARBONATE
  specific = 4
FEATURE [App::DocumentObjectGroupPython] Na_element015  label="Na_element : 1"  # scripted group (container) (typed FeaturePython)
  n = 1
  ref = Na_element
FEATURE [App::DocumentObjectGroupPython] I_element009  label="I_element : 005"  # scripted group (container) (typed FeaturePython)
  n = 1
  ref = I_element
FEATURE [App::DocumentObjectGroupPython] G4_SODIUM_IODIDE  # scripted group (container) (typed FeaturePython)
  Dunit = g/cm3
  Dvalue = 3.667
  Group = -> [Na_element015,I_element009]
  conduct = 2
  density = 1
  expand = 3
  formula = G4_SODIUM_IODIDE
  name = G4_SODIUM_IODIDE
  specific = 4
FEATURE [App::DocumentObjectGroupPython] Na_element016  label="Na_element : 003"  # scripted group (container) (typed FeaturePython)
  n = 2
  ref = Na_element
FEATURE [App::DocumentObjectGroupPython] O_element090  label="O_element : 050"  # scripted group (container) (typed FeaturePython)
  n = 1
  ref = O_element
FEATURE [App::DocumentObjectGroupPython] G4_SODIUM_MONOXIDE  # scripted group (container) (typed FeaturePython)
  Dunit = g/cm3
  Dvalue = 2.27
  Group = -> [Na_element016,O_element090]
  conduct = 2
  density = 1
  expand = 3
  formula = G4_SODIUM_MONOXIDE
  name = G4_SODIUM_MONOXIDE
  specific = 4
FEATURE [App::DocumentObjectGroupPython] Na_element017  label="Na_element : 004"  # scripted group (container) (typed FeaturePython)
  n = 1
  ref = Na_element
FEATURE [App::DocumentObjectGroupPython] N_element040  label="N_element : 018"  # scripted group (container) (typed FeaturePython)
  n = 1
  ref = N_element
FEATURE [App::DocumentObjectGroupPython] O_element091  label="O_element : 051"  # scripted group (container) (typed FeaturePython)
  n = 3
  ref = O_element
FEATURE [App::DocumentObjectGroupPython] G4_SODIUM_NITRATE  # scripted group (container) (typed FeaturePython)
  Dunit = g/cm3
  Dvalue = 2.261
  Group = -> [Na_element017,N_element040,O_element091]
  conduct = 2
  density = 1
  expand = 3
  formula = G4_SODIUM_NITRATE
  name = G4_SODIUM_NITRATE
  specific = 4
FEATURE [App::DocumentObjectGroupPython] C_element105  label="C_element : 059"  # scripted group (container) (typed FeaturePython)
  n = 14
  ref = C_element
FEATURE [App::DocumentObjectGroupPython] H_element096  label="H_element : 053"  # scripted group (container) (typed FeaturePython)
  n = 12
  ref = H_element
FEATURE [App::DocumentObjectGroupPython] G4_STILBENE  # scripted group (container) (typed FeaturePython)
  Dunit = g/cm3
  Dvalue = 0.9707
  Group = -> [C_element105,H_element096]
  conduct = 2
  density = 1
  expand = 3
  formula = G4_STILBENE
  name = G4_STILBENE
  specific = 4
FEATURE [App::DocumentObjectGroupPython] C_element106  label="C_element : 12"  # scripted group (container) (typed FeaturePython)
  n = 12
  ref = C_element
FEATURE [App::DocumentObjectGroupPython] H_element097  label="H_element : 22"  # scripted group (container) (typed FeaturePython)
  n = 22
  ref = H_element
FEATURE [App::DocumentObjectGroupPython] O_element092  label="O_element : 11"  # scripted group (container) (typed FeaturePython)
  n = 11
  ref = O_element
FEATURE [App::DocumentObjectGroupPython] G4_SUCROSE  # scripted group (container) (typed FeaturePython)
  Dunit = g/cm3
  Dvalue = 1.5805
  Group = -> [C_element106,H_element097,O_element092]
  conduct = 2
  density = 1
  expand = 3
  formula = G4_SUCROSE
  name = G4_SUCROSE
  specific = 4
FEATURE [App::DocumentObjectGroupPython] C_element107  label="C_element : 18"  # scripted group (container) (typed FeaturePython)
  n = 18
  ref = C_element
FEATURE [App::DocumentObjectGroupPython] H_element098  label="H_element : 054"  # scripted group (container) (typed FeaturePython)
  n = 14
  ref = H_element
FEATURE [App::DocumentObjectGroupPython] G4_TERPHENYL  # scripted group (container) (typed FeaturePython)
  Dunit = g/cm3
  Dvalue = 1.24
  Group = -> [C_element107,H_element098]
  conduct = 2
  density = 1
  expand = 3
  formula = G4_TERPHENYL
  name = G4_TERPHENYL
  specific = 4
FEATURE [App::DocumentObjectGroupPython] H_element099  label="H_element : 0.146"  # scripted group (container) (typed FeaturePython)
  n = 0.106
FEATURE [App::DocumentObjectGroupPython] C_element108  label="C_element : 0.883"  # scripted group (container) (typed FeaturePython)
  n = 0.099
FEATURE [App::DocumentObjectGroupPython] N_element041  label="N_element : 0.020"  # scripted group (container) (typed FeaturePython)
  n = 0.02
FEATURE [App::DocumentObjectGroupPython] O_element093  label="O_element : 0.766"  # scripted group (container) (typed FeaturePython)
  n = 0.766
FEATURE [App::DocumentObjectGroupPython] Na_element018  label="Na_element : 0.101"  # scripted group (container) (typed FeaturePython)
  n = 0.002
FEATURE [App::DocumentObjectGroupPython] P_element010  label="P_element : 0.108"  # scripted group (container) (typed FeaturePython)
  n = 0.001
FEATURE [App::DocumentObjectGroupPython] S_element021  label="S_element : 0.022"  # scripted group (container) (typed FeaturePython)
  n = 0.002
FEATURE [App::DocumentObjectGroupPython] Cl_element024  label="Cl_element : 0.002"  # scripted group (container) (typed FeaturePython)
  n = 0.002
FEATURE [App::DocumentObjectGroupPython] K_element011  label="K_element : 0.017"  # scripted group (container) (typed FeaturePython)
  n = 0.002
FEATURE [App::DocumentObjectGroupPython] G4_TESTIS_ICRP  # scripted group (container) (typed FeaturePython)
  Dunit = g/cm3
  Dvalue = 1.04
  Group = -> [H_element099,C_element108,N_element041,O_element093,Na_element018,P_element010,S_element021,Cl_element024,K_element011]
  conduct = 2
  density = 1
  expand = 3
  formula = G4_TESTIS_ICRP
  name = G4_TESTIS_ICRP
  specific = 4
FEATURE [App::DocumentObjectGroupPython] C_element109  label="C_element : 060"  # scripted group (container) (typed FeaturePython)
  n = 2
  ref = C_element
FEATURE [App::DocumentObjectGroupPython] Cl_element025  label="Cl_element : 012"  # scripted group (container) (typed FeaturePython)
  n = 4
  ref = Cl_element
FEATURE [App::DocumentObjectGroupPython] G4_TETRACHLOROETHYLENE  # scripted group (container) (typed FeaturePython)
  Dunit = g/cm3
  Dvalue = 1.625
  Group = -> [C_element109,Cl_element025]
  conduct = 2
  density = 1
  expand = 3
  formula = G4_TETRACHLOROETHYLENE
  name = G4_TETRACHLOROETHYLENE
  specific = 4
FEATURE [App::DocumentObjectGroupPython] Tl_element001  label="Tl_element : 1"  # scripted group (container) (typed FeaturePython)
  n = 1
  ref = Tl_element
FEATURE [App::DocumentObjectGroupPython] Cl_element026  label="Cl_element : 013"  # scripted group (container) (typed FeaturePython)
  n = 1
  ref = Cl_element
FEATURE [App::DocumentObjectGroupPython] G4_THALLIUM_CHLORIDE  # scripted group (container) (typed FeaturePython)
  Dunit = g/cm3
  Dvalue = 7.004
  Group = -> [Tl_element001,Cl_element026]
  conduct = 2
  density = 1
  expand = 3
  formula = G4_THALLIUM_CHLORIDE
  name = G4_THALLIUM_CHLORIDE
  specific = 4
FEATURE [App::DocumentObjectGroupPython] H_element100  label="H_element : 0.147"  # scripted group (container) (typed FeaturePython)
  n = 0.105
FEATURE [App::DocumentObjectGroupPython] C_element110  label="C_element : 0.256"  # scripted group (container) (typed FeaturePython)
  n = 0.256
FEATURE [App::DocumentObjectGroupPython] N_element042  label="N_element : 0.760"  # scripted group (container) (typed FeaturePython)
  n = 0.027
FEATURE [App::DocumentObjectGroupPython] O_element094  label="O_element : 0.602"  # scripted group (container) (typed FeaturePython)
  n = 0.602
FEATURE [App::DocumentObjectGroupPython] Na_element019  label="Na_element : 0.102"  # scripted group (container) (typed FeaturePython)
  n = 0.001
FEATURE [App::DocumentObjectGroupPython] P_element011  label="P_element : 0.109"  # scripted group (container) (typed FeaturePython)
  n = 0.002
FEATURE [App::DocumentObjectGroupPython] S_element022  label="S_element : 0.023"  # scripted group (container) (typed FeaturePython)
  n = 0.003
FEATURE [App::DocumentObjectGroupPython] Cl_element027  label="Cl_element : 0.591"  # scripted group (container) (typed FeaturePython)
  n = 0.002
FEATURE [App::DocumentObjectGroupPython] K_element012  label="K_element : 0.018"  # scripted group (container) (typed FeaturePython)
  n = 0.002
FEATURE [App::DocumentObjectGroupPython] G4_TISSUE_SOFT_ICRP  # scripted group (container) (typed FeaturePython)
  Dunit = g/cm3
  Dvalue = 1.03
  Group = -> [H_element100,C_element110,N_element042,O_element094,Na_element019,P_element011,S_element022,Cl_element027,K_element012]
  conduct = 2
  density = 1
  expand = 3
  formula = G4_TISSUE_SOFT_ICRP
  name = G4_TISSUE_SOFT_ICRP
  specific = 4
FEATURE [App::DocumentObjectGroupPython] H_element101  label="H_element : 0.148"  # scripted group (container) (typed FeaturePython)
  n = 0.101
FEATURE [App::DocumentObjectGroupPython] C_element111  label="C_element : 0.111"  # scripted group (container) (typed FeaturePython)
  n = 0.111
FEATURE [App::DocumentObjectGroupPython] N_element043  label="N_element : 0.026"  # scripted group (container) (typed FeaturePython)
  n = 0.026
FEATURE [App::DocumentObjectGroupPython] O_element095  label="O_element : 0.762"  # scripted group (container) (typed FeaturePython)
  n = 0.762
FEATURE [App::DocumentObjectGroupPython] G4_TISSUE_SOFT_ICRU_4  label="G4_TISSUE_SOFT_ICRU-4"  # scripted group (container) (typed FeaturePython)
  Dunit = g/cm3
  Dvalue = 1
  Group = -> [H_element101,C_element111,N_element043,O_element095]
  conduct = 2
  density = 1
  expand = 3
  formula = G4_TISSUE_SOFT_ICRU-4
  name = G4_TISSUE_SOFT_ICRU-4
  specific = 4
FEATURE [App::DocumentObjectGroupPython] H_element102  label="H_element : 0.149"  # scripted group (container) (typed FeaturePython)
  n = 0.101869
FEATURE [App::DocumentObjectGroupPython] C_element112  label="C_element : 0.456"  # scripted group (container) (typed FeaturePython)
  n = 0.456179
FEATURE [App::DocumentObjectGroupPython] N_element044  label="N_element : 0.761"  # scripted group (container) (typed FeaturePython)
  n = 0.035172
FEATURE [App::DocumentObjectGroupPython] O_element096  label="O_element : 0.407"  # scripted group (container) (typed FeaturePython)
  n = 0.40678
FEATURE [App::DocumentObjectGroupPython] G4_TISSUE_METHANE  label="G4_TISSUE-METHANE"  # scripted group (container) (typed FeaturePython)
  Dunit = g/cm3
  Dvalue = 0.00106409
  Group = -> [H_element102,C_element112,N_element044,O_element096]
  conduct = 2
  density = 1
  expand = 3
  formula = G4_TISSUE-METHANE
  name = G4_TISSUE-METHANE
  specific = 4
FEATURE [App::DocumentObjectGroupPython] H_element103  label="H_element : 0.103"  # scripted group (container) (typed FeaturePython)
  n = 0.102672
FEATURE [App::DocumentObjectGroupPython] C_element113  label="C_element : 0.569"  # scripted group (container) (typed FeaturePython)
  n = 0.56894
FEATURE [App::DocumentObjectGroupPython] N_element045  label="N_element : 0.762"  # scripted group (container) (typed FeaturePython)
  n = 0.035022
FEATURE [App::DocumentObjectGroupPython] O_element097  label="O_element : 0.293"  # scripted group (container) (typed FeaturePython)
  n = 0.293366
FEATURE [App::DocumentObjectGroupPython] G4_TISSUE_PROPANE  label="G4_TISSUE-PROPANE"  # scripted group (container) (typed FeaturePython)
  Dunit = g/cm3
  Dvalue = 0.00182628
  Group = -> [H_element103,C_element113,N_element045,O_element097]
  conduct = 2
  density = 1
  expand = 3
  formula = G4_TISSUE-PROPANE
  name = G4_TISSUE-PROPANE
  specific = 4
FEATURE [App::DocumentObjectGroupPython] Ti_element003  label="Ti_element : 1"  # scripted group (container) (typed FeaturePython)
  n = 1
  ref = Ti_element
FEATURE [App::DocumentObjectGroupPython] O_element098  label="O_element : 052"  # scripted group (container) (typed FeaturePython)
  n = 2
  ref = O_element
FEATURE [App::DocumentObjectGroupPython] G4_TITANIUM_DIOXIDE  # scripted group (container) (typed FeaturePython)
  Dunit = g/cm3
  Dvalue = 4.26
  Group = -> [Ti_element003,O_element098]
  conduct = 2
  density = 1
  expand = 3
  formula = G4_TITANIUM_DIOXIDE
  name = G4_TITANIUM_DIOXIDE
  specific = 4
FEATURE [App::DocumentObjectGroupPython] C_element114  label="C_element : 061"  # scripted group (container) (typed FeaturePython)
  n = 7
  ref = C_element
FEATURE [App::DocumentObjectGroupPython] H_element104  label="H_element : 055"  # scripted group (container) (typed FeaturePython)
  n = 8
  ref = H_element
FEATURE [App::DocumentObjectGroupPython] G4_TOLUENE  # scripted group (container) (typed FeaturePython)
  Dunit = g/cm3
  Dvalue = 0.8669
  Group = -> [C_element114,H_element104]
  conduct = 2
  density = 1
  expand = 3
  formula = G4_TOLUENE
  name = G4_TOLUENE
  specific = 4
FEATURE [App::DocumentObjectGroupPython] C_element115  label="C_element : 062"  # scripted group (container) (typed FeaturePython)
  n = 2
  ref = C_element
FEATURE [App::DocumentObjectGroupPython] H_element105  label="H_element : 056"  # scripted group (container) (typed FeaturePython)
  n = 1
  ref = H_element
FEATURE [App::DocumentObjectGroupPython] Cl_element028  label="Cl_element : 014"  # scripted group (container) (typed FeaturePython)
  n = 3
  ref = Cl_element
FEATURE [App::DocumentObjectGroupPython] G4_TRICHLOROETHYLENE  # scripted group (container) (typed FeaturePython)
  Dunit = g/cm3
  Dvalue = 1.46
  Group = -> [C_element115,H_element105,Cl_element028]
  conduct = 2
  density = 1
  expand = 3
  formula = G4_TRICHLOROETHYLENE
  name = G4_TRICHLOROETHYLENE
  specific = 4
FEATURE [App::DocumentObjectGroupPython] C_element116  label="C_element : 063"  # scripted group (container) (typed FeaturePython)
  n = 6
  ref = C_element
FEATURE [App::DocumentObjectGroupPython] H_element106  label="H_element : 15"  # scripted group (container) (typed FeaturePython)
  n = 15
  ref = H_element
FEATURE [App::DocumentObjectGroupPython] O_element099  label="O_element : 053"  # scripted group (container) (typed FeaturePython)
  n = 4
  ref = O_element
FEATURE [App::DocumentObjectGroupPython] P_element012  label="P_element : 1"  # scripted group (container) (typed FeaturePython)
  n = 1
  ref = P_element
FEATURE [App::DocumentObjectGroupPython] G4_TRIETHYL_PHOSPHATE  # scripted group (container) (typed FeaturePython)
  Dunit = g/cm3
  Dvalue = 1.07
  Group = -> [C_element116,H_element106,O_element099,P_element012]
  conduct = 2
  density = 1
  expand = 3
  formula = G4_TRIETHYL_PHOSPHATE
  name = G4_TRIETHYL_PHOSPHATE
  specific = 4
FEATURE [App::DocumentObjectGroupPython] W_element003  label="W_element : 003"  # scripted group (container) (typed FeaturePython)
  n = 1
  ref = W_element
FEATURE [App::DocumentObjectGroupPython] F_element017  label="F_element : 6"  # scripted group (container) (typed FeaturePython)
  n = 6
  ref = F_element
FEATURE [App::DocumentObjectGroupPython] G4_TUNGSTEN_HEXAFLUORIDE  # scripted group (container) (typed FeaturePython)
  Dunit = g/cm3
  Dvalue = 2.4
  Group = -> [W_element003,F_element017]
  conduct = 2
  density = 1
  expand = 3
  formula = G4_TUNGSTEN_HEXAFLUORIDE
  name = G4_TUNGSTEN_HEXAFLUORIDE
  specific = 4
FEATURE [App::DocumentObjectGroupPython] U_element001  label="U_element : 1"  # scripted group (container) (typed FeaturePython)
  n = 1
  ref = U_element
FEATURE [App::DocumentObjectGroupPython] C_element117  label="C_element : 064"  # scripted group (container) (typed FeaturePython)
  n = 2
  ref = C_element
FEATURE [App::DocumentObjectGroupPython] G4_URANIUM_DICARBIDE  # scripted group (container) (typed FeaturePython)
  Dunit = g/cm3
  Dvalue = 11.28
  Group = -> [U_element001,C_element117]
  conduct = 2
  density = 1
  expand = 3
  formula = G4_URANIUM_DICARBIDE
  name = G4_URANIUM_DICARBIDE
  specific = 4
FEATURE [App::DocumentObjectGroupPython] U_element002  label="U_element : 002"  # scripted group (container) (typed FeaturePython)
  n = 1
  ref = U_element
FEATURE [App::DocumentObjectGroupPython] C_element118  label="C_element : 065"  # scripted group (container) (typed FeaturePython)
  n = 1
  ref = C_element
FEATURE [App::DocumentObjectGroupPython] G4_URANIUM_MONOCARBIDE  # scripted group (container) (typed FeaturePython)
  Dunit = g/cm3
  Dvalue = 13.63
  Group = -> [U_element002,C_element118]
  conduct = 2
  density = 1
  expand = 3
  formula = G4_URANIUM_MONOCARBIDE
  name = G4_URANIUM_MONOCARBIDE
  specific = 4
FEATURE [App::DocumentObjectGroupPython] U_element003  label="U_element : 003"  # scripted group (container) (typed FeaturePython)
  n = 1
  ref = U_element
FEATURE [App::DocumentObjectGroupPython] O_element100  label="O_element : 054"  # scripted group (container) (typed FeaturePython)
  n = 2
  ref = O_element
FEATURE [App::DocumentObjectGroupPython] G4_URANIUM_OXIDE  # scripted group (container) (typed FeaturePython)
  Dunit = g/cm3
  Dvalue = 10.96
  Group = -> [U_element003,O_element100]
  conduct = 2
  density = 1
  expand = 3
  formula = G4_URANIUM_OXIDE
  name = G4_URANIUM_OXIDE
  specific = 4
FEATURE [App::DocumentObjectGroupPython] C_element119  label="C_element : 066"  # scripted group (container) (typed FeaturePython)
  n = 1
  ref = C_element
FEATURE [App::DocumentObjectGroupPython] H_element107  label="H_element : 057"  # scripted group (container) (typed FeaturePython)
  n = 4
  ref = H_element
FEATURE [App::DocumentObjectGroupPython] N_element046  label="N_element : 019"  # scripted group (container) (typed FeaturePython)
  n = 2
  ref = N_element
FEATURE [App::DocumentObjectGroupPython] O_element101  label="O_element : 055"  # scripted group (container) (typed FeaturePython)
  n = 1
  ref = O_element
FEATURE [App::DocumentObjectGroupPython] G4_UREA  # scripted group (container) (typed FeaturePython)
  Dunit = g/cm3
  Dvalue = 1.323
  Group = -> [C_element119,H_element107,N_element046,O_element101]
  conduct = 2
  density = 1
  expand = 3
  formula = G4_UREA
  name = G4_UREA
  specific = 4
FEATURE [App::DocumentObjectGroupPython] C_element120  label="C_element : 067"  # scripted group (container) (typed FeaturePython)
  n = 5
  ref = C_element
FEATURE [App::DocumentObjectGroupPython] H_element108  label="H_element : 058"  # scripted group (container) (typed FeaturePython)
  n = 11
  ref = H_element
FEATURE [App::DocumentObjectGroupPython] N_element047  label="N_element : 020"  # scripted group (container) (typed FeaturePython)
  n = 1
  ref = N_element
FEATURE [App::DocumentObjectGroupPython] O_element102  label="O_element : 056"  # scripted group (container) (typed FeaturePython)
  n = 2
  ref = O_element
FEATURE [App::DocumentObjectGroupPython] G4_VALINE  # scripted group (container) (typed FeaturePython)
  Dunit = g/cm3
  Dvalue = 1.23
  Group = -> [C_element120,H_element108,N_element047,O_element102]
  conduct = 2
  density = 1
  expand = 3
  formula = G4_VALINE
  name = G4_VALINE
  specific = 4
FEATURE [App::DocumentObjectGroupPython] H_element109  label="H_element : 0.009"  # scripted group (container) (typed FeaturePython)
  n = 0.009417
FEATURE [App::DocumentObjectGroupPython] C_element121  label="C_element : 0.281"  # scripted group (container) (typed FeaturePython)
  n = 0.280555
FEATURE [App::DocumentObjectGroupPython] F_element018  label="F_element : 0.710"  # scripted group (container) (typed FeaturePython)
  n = 0.710028
FEATURE [App::DocumentObjectGroupPython] G4_VITON  # scripted group (container) (typed FeaturePython)
  Dunit = g/cm3
  Dvalue = 1.8
  Group = -> [H_element109,C_element121,F_element018]
  conduct = 2
  density = 1
  expand = 3
  formula = G4_VITON
  name = G4_VITON
  specific = 4
FEATURE [App::DocumentObjectGroupPython] H_element110  label="H_element : 059"  # scripted group (container) (typed FeaturePython)
  n = 2
  ref = H_element
FEATURE [App::DocumentObjectGroupPython] O_element103  label="O_element : 057"  # scripted group (container) (typed FeaturePython)
  n = 1
  ref = O_element
FEATURE [App::DocumentObjectGroupPython] G4_WATER  # scripted group (container) (typed FeaturePython)
  Dunit = g/cm3
  Dvalue = 1
  Group = -> [H_element110,O_element103]
  conduct = 2
  density = 1
  expand = 3
  formula = G4_WATER
  name = G4_WATER
  specific = 4
FEATURE [App::DocumentObjectGroupPython] H_element111  label="H_element : 060"  # scripted group (container) (typed FeaturePython)
  n = 2
  ref = H_element
FEATURE [App::DocumentObjectGroupPython] O_element104  label="O_element : 058"  # scripted group (container) (typed FeaturePython)
  n = 1
  ref = O_element
FEATURE [App::DocumentObjectGroupPython] G4_WATER_VAPOR  # scripted group (container) (typed FeaturePython)
  Dunit = g/cm3
  Dvalue = 0.000756182
  Group = -> [H_element111,O_element104]
  conduct = 2
  density = 1
  expand = 3
  formula = G4_WATER_VAPOR
  name = G4_WATER_VAPOR
  specific = 4
FEATURE [App::DocumentObjectGroupPython] C_element122  label="C_element : 068"  # scripted group (container) (typed FeaturePython)
  n = 8
  ref = C_element
FEATURE [App::DocumentObjectGroupPython] H_element112  label="H_element : 061"  # scripted group (container) (typed FeaturePython)
  n = 10
  ref = H_element
FEATURE [App::DocumentObjectGroupPython] G4_XYLENE  # scripted group (container) (typed FeaturePython)
  Dunit = g/cm3
  Dvalue = 0.87
  Group = -> [C_element122,H_element112]
  conduct = 2
  density = 1
  expand = 3
  formula = G4_XYLENE
  name = G4_XYLENE
  specific = 4
FEATURE [App::DocumentObjectGroupPython] C_element123  label="C_element : 069"  # scripted group (container) (typed FeaturePython)
  n = 1
  ref = C_element
FEATURE [App::DocumentObjectGroupPython] G4_GRAPHITE  # scripted group (container) (typed FeaturePython)
  Dunit = g/cm3
  Dvalue = 2.21
  Group = -> [C_element123]
  conduct = 2
  density = 1
  expand = 3
  formula = G4_GRAPHITE
  name = G4_GRAPHITE
  specific = 4
FEATURE [App::DocumentObjectGroupPython] NIST  # scripted group (container) (typed FeaturePython)
  Group = -> [G4_A_150_TISSUE,G4_ACETONE,G4_ACETYLENE,G4_ADENINE,G4_ADIPOSE_TISSUE_ICRP,G4_AIR,G4_ALANINE,G4_ALUMINUM_OXIDE,G4_AMBER,G4_AMMONIA,G4_ANILINE,G4_ANTHRACENE,G4_B_100_BONE,G4_BAKELITE,G4_BARIUM_FLUORIDE,G4_BARIUM_SULFATE,G4_BENZENE,G4_BERYLLIUM_OXIDE,G4_BGO,G4_BLOOD_ICRP,G4_BONE_COMPACT_ICRU,G4_BONE_CORTICAL_ICRP,G4_BORON_CARBIDE,G4_BORON_OXIDE,G4_BRAIN_ICRP,G4_BUTANE,G4_N_BUTYL_ALCOHOL,G4_C_552,+152 more]
FEATURE [App::DocumentObjectGroupPython] H_element113  label="H_element : 062"  # scripted group (container) (typed FeaturePython)
  n = 1
  ref = H_element
FEATURE [App::DocumentObjectGroupPython] G4_H  # scripted group (container) (typed FeaturePython)
  Dunit = g/cm3
  Dvalue = 8.3748e-05
  Group = -> [H_element113]
  conduct = 2
  density = 1
  expand = 3
  formula = H
  name = G4_H
  specific = 4
FEATURE [App::DocumentObjectGroupPython] He_element001  label="He_element : 1"  # scripted group (container) (typed FeaturePython)
  n = 1
  ref = He_element
FEATURE [App::DocumentObjectGroupPython] G4_He  # scripted group (container) (typed FeaturePython)
  Dunit = g/cm3
  Dvalue = 0.000166322
  Group = -> [He_element001]
  conduct = 2
  density = 1
  expand = 3
  formula = He
  name = G4_He
  specific = 4
FEATURE [App::DocumentObjectGroupPython] Li_element008  label="Li_element : 008"  # scripted group (container) (typed FeaturePython)
  n = 1
  ref = Li_element
FEATURE [App::DocumentObjectGroupPython] G4_Li  # scripted group (container) (typed FeaturePython)
  Dunit = g/cm3
  Dvalue = 0.534
  Group = -> [Li_element008]
  conduct = 2
  density = 1
  expand = 3
  formula = Li
  name = G4_Li
  specific = 4
FEATURE [App::DocumentObjectGroupPython] Be_element002  label="Be_element : 002"  # scripted group (container) (typed FeaturePython)
  n = 1
  ref = Be_element
FEATURE [App::DocumentObjectGroupPython] G4_Be  # scripted group (container) (typed FeaturePython)
  Dunit = g/cm3
  Dvalue = 1.848
  Group = -> [Be_element002]
  conduct = 2
  density = 1
  expand = 3
  formula = Be
  name = G4_Be
  specific = 4
FEATURE [App::DocumentObjectGroupPython] B_element007  label="B_element : 007"  # scripted group (container) (typed FeaturePython)
  n = 1
  ref = B_element
FEATURE [App::DocumentObjectGroupPython] G4_B  # scripted group (container) (typed FeaturePython)
  Dunit = g/cm3
  Dvalue = 2.37
  Group = -> [B_element007]
  conduct = 2
  density = 1
  expand = 3
  formula = B
  name = G4_B
  specific = 4
FEATURE [App::DocumentObjectGroupPython] C_element124  label="C_element : 070"  # scripted group (container) (typed FeaturePython)
  n = 1
  ref = C_element
FEATURE [App::DocumentObjectGroupPython] G4_C  # scripted group (container) (typed FeaturePython)
  Dunit = g/cm3
  Dvalue = 2
  Group = -> [C_element124]
  conduct = 2
  density = 1
  expand = 3
  formula = C
  name = G4_C
  specific = 4
FEATURE [App::DocumentObjectGroupPython] N_element048  label="N_element : 021"  # scripted group (container) (typed FeaturePython)
  n = 1
  ref = N_element
FEATURE [App::DocumentObjectGroupPython] G4_N  # scripted group (container) (typed FeaturePython)
  Dunit = g/cm3
  Dvalue = 0.0011652
  Group = -> [N_element048]
  conduct = 2
  density = 1
  expand = 3
  formula = N
  name = G4_N
  specific = 4
FEATURE [App::DocumentObjectGroupPython] O_element105  label="O_element : 059"  # scripted group (container) (typed FeaturePython)
  n = 1
  ref = O_element
FEATURE [App::DocumentObjectGroupPython] G4_O  # scripted group (container) (typed FeaturePython)
  Dunit = g/cm3
  Dvalue = 0.00133151
  Group = -> [O_element105]
  conduct = 2
  density = 1
  expand = 3
  formula = O
  name = G4_O
  specific = 4
FEATURE [App::DocumentObjectGroupPython] F_element019  label="F_element : 008"  # scripted group (container) (typed FeaturePython)
  n = 1
  ref = F_element
FEATURE [App::DocumentObjectGroupPython] G4_F  # scripted group (container) (typed FeaturePython)
  Dunit = g/cm3
  Dvalue = 0.00158029
  Group = -> [F_element019]
  conduct = 2
  density = 1
  expand = 3
  formula = F
  name = G4_F
  specific = 4
FEATURE [App::DocumentObjectGroupPython] Ne_element001  label="Ne_element : 1"  # scripted group (container) (typed FeaturePython)
  n = 1
  ref = Ne_element
FEATURE [App::DocumentObjectGroupPython] G4_Ne  # scripted group (container) (typed FeaturePython)
  Dunit = g/cm3
  Dvalue = 0.000838505
  Group = -> [Ne_element001]
  conduct = 2
  density = 1
  expand = 3
  formula = Ne
  name = G4_Ne
  specific = 4
FEATURE [App::DocumentObjectGroupPython] Na_element020  label="Na_element : 005"  # scripted group (container) (typed FeaturePython)
  n = 1
  ref = Na_element
FEATURE [App::DocumentObjectGroupPython] G4_Na  # scripted group (container) (typed FeaturePython)
  Dunit = g/cm3
  Dvalue = 0.971
  Group = -> [Na_element020]
  conduct = 2
  density = 1
  expand = 3
  formula = Na
  name = G4_Na
  specific = 4
FEATURE [App::DocumentObjectGroupPython] Mg_element011  label="Mg_element : 005"  # scripted group (container) (typed FeaturePython)
  n = 1
  ref = Mg_element
FEATURE [App::DocumentObjectGroupPython] G4_Mg  # scripted group (container) (typed FeaturePython)
  Dunit = g/cm3
  Dvalue = 1.74
  Group = -> [Mg_element011]
  conduct = 2
  density = 1
  expand = 3
  formula = Mg
  name = G4_Mg
  specific = 4
FEATURE [App::DocumentObjectGroupPython] Al_element004  label="Al_element : 1"  # scripted group (container) (typed FeaturePython)
  n = 1
  ref = Al_element
FEATURE [App::DocumentObjectGroupPython] G4_Al  # scripted group (container) (typed FeaturePython)
  Dunit = g/cm3
  Dvalue = 2.699
  Group = -> [Al_element004]
  conduct = 2
  density = 1
  expand = 3
  formula = Al
  name = G4_Al
  specific = 4
FEATURE [App::DocumentObjectGroupPython] Si_element007  label="Si_element : 002"  # scripted group (container) (typed FeaturePython)
  n = 1
  ref = Si_element
FEATURE [App::DocumentObjectGroupPython] G4_Si  # scripted group (container) (typed FeaturePython)
  Dunit = g/cm3
  Dvalue = 2.33
  Group = -> [Si_element007]
  conduct = 2
  density = 1
  expand = 3
  formula = Si
  name = G4_Si
  specific = 4
FEATURE [App::DocumentObjectGroupPython] P_element013  label="P_element : 002"  # scripted group (container) (typed FeaturePython)
  n = 1
  ref = P_element
FEATURE [App::DocumentObjectGroupPython] G4_P  # scripted group (container) (typed FeaturePython)
  Dunit = g/cm3
  Dvalue = 2.2
  Group = -> [P_element013]
  conduct = 2
  density = 1
  expand = 3
  formula = P
  name = G4_P
  specific = 4
FEATURE [App::DocumentObjectGroupPython] S_element023  label="S_element : 007"  # scripted group (container) (typed FeaturePython)
  n = 1
  ref = S_element
FEATURE [App::DocumentObjectGroupPython] G4_S  # scripted group (container) (typed FeaturePython)
  Dunit = g/cm3
  Dvalue = 2
  Group = -> [S_element023]
  conduct = 2
  density = 1
  expand = 3
  formula = S
  name = G4_S
  specific = 4
FEATURE [App::DocumentObjectGroupPython] Cl_element029  label="Cl_element : 015"  # scripted group (container) (typed FeaturePython)
  n = 1
  ref = Cl_element
FEATURE [App::DocumentObjectGroupPython] G4_Cl  # scripted group (container) (typed FeaturePython)
  Dunit = g/cm3
  Dvalue = 0.00299473
  Group = -> [Cl_element029]
  conduct = 2
  density = 1
  expand = 3
  formula = Cl
  name = G4_Cl
  specific = 4
FEATURE [App::DocumentObjectGroupPython] Ar_element002  label="Ar_element : 1"  # scripted group (container) (typed FeaturePython)
  n = 1
  ref = Ar_element
FEATURE [App::DocumentObjectGroupPython] G4_Ar  # scripted group (container) (typed FeaturePython)
  Dunit = g/cm3
  Dvalue = 0.00166201
  Group = -> [Ar_element002]
  conduct = 2
  density = 1
  expand = 3
  formula = Ar
  name = G4_Ar
  specific = 4
FEATURE [App::DocumentObjectGroupPython] K_element013  label="K_element : 003"  # scripted group (container) (typed FeaturePython)
  n = 1
  ref = K_element
FEATURE [App::DocumentObjectGroupPython] G4_K  # scripted group (container) (typed FeaturePython)
  Dunit = g/cm3
  Dvalue = 0.862
  Group = -> [K_element013]
  conduct = 2
  density = 1
  expand = 3
  formula = K
  name = G4_K
  specific = 4
FEATURE [App::DocumentObjectGroupPython] Ca_element014  label="Ca_element : 007"  # scripted group (container) (typed FeaturePython)
  n = 1
  ref = Ca_element
FEATURE [App::DocumentObjectGroupPython] G4_Ca  # scripted group (container) (typed FeaturePython)
  Dunit = g/cm3
  Dvalue = 1.55
  Group = -> [Ca_element014]
  conduct = 2
  density = 1
  expand = 3
  formula = Ca
  name = G4_Ca
  specific = 4
FEATURE [App::DocumentObjectGroupPython] Sc_element001  label="Sc_element : 1"  # scripted group (container) (typed FeaturePython)
  n = 1
  ref = Sc_element
FEATURE [App::DocumentObjectGroupPython] G4_Sc  # scripted group (container) (typed FeaturePython)
  Dunit = g/cm3
  Dvalue = 2.989
  Group = -> [Sc_element001]
  conduct = 2
  density = 1
  expand = 3
  formula = Sc
  name = G4_Sc
  specific = 4
FEATURE [App::DocumentObjectGroupPython] Ti_element004  label="Ti_element : 002"  # scripted group (container) (typed FeaturePython)
  n = 1
  ref = Ti_element
FEATURE [App::DocumentObjectGroupPython] G4_Ti  # scripted group (container) (typed FeaturePython)
  Dunit = g/cm3
  Dvalue = 4.54
  Group = -> [Ti_element004]
  conduct = 2
  density = 1
  expand = 3
  formula = Ti
  name = G4_Ti
  specific = 4
FEATURE [App::DocumentObjectGroupPython] V_element001  label="V_element : 1"  # scripted group (container) (typed FeaturePython)
  n = 1
  ref = V_element
FEATURE [App::DocumentObjectGroupPython] G4_V  # scripted group (container) (typed FeaturePython)
  Dunit = g/cm3
  Dvalue = 6.11
  Group = -> [V_element001]
  conduct = 2
  density = 1
  expand = 3
  formula = V
  name = G4_V
  specific = 4
FEATURE [App::DocumentObjectGroupPython] Cr_element001  label="Cr_element : 1"  # scripted group (container) (typed FeaturePython)
  n = 1
  ref = Cr_element
FEATURE [App::DocumentObjectGroupPython] G4_Cr  # scripted group (container) (typed FeaturePython)
  Dunit = g/cm3
  Dvalue = 7.18
  Group = -> [Cr_element001]
  conduct = 2
  density = 1
  expand = 3
  formula = Cr
  name = G4_Cr
  specific = 4
FEATURE [App::DocumentObjectGroupPython] Mn_element001  label="Mn_element : 1"  # scripted group (container) (typed FeaturePython)
  n = 1
  ref = Mn_element
FEATURE [App::DocumentObjectGroupPython] G4_Mn  # scripted group (container) (typed FeaturePython)
  Dunit = g/cm3
  Dvalue = 7.44
  Group = -> [Mn_element001]
  conduct = 2
  density = 1
  expand = 3
  formula = Mn
  name = G4_Mn
  specific = 4
FEATURE [App::DocumentObjectGroupPython] Fe_element007  label="Fe_element : 004"  # scripted group (container) (typed FeaturePython)
  n = 1
  ref = Fe_element
FEATURE [App::DocumentObjectGroupPython] G4_Fe  # scripted group (container) (typed FeaturePython)
  Dunit = g/cm3
  Dvalue = 7.874
  Group = -> [Fe_element007]
  conduct = 2
  density = 1
  expand = 3
  formula = Fe
  name = G4_Fe
  specific = 4
FEATURE [App::DocumentObjectGroupPython] Co_element001  label="Co_element : 1"  # scripted group (container) (typed FeaturePython)
  n = 1
  ref = Co_element
FEATURE [App::DocumentObjectGroupPython] G4_Co  # scripted group (container) (typed FeaturePython)
  Dunit = g/cm3
  Dvalue = 8.9
  Group = -> [Co_element001]
  conduct = 2
  density = 1
  expand = 3
  formula = Co
  name = G4_Co
  specific = 4
FEATURE [App::DocumentObjectGroupPython] Ni_element001  label="Ni_element : 1"  # scripted group (container) (typed FeaturePython)
  n = 1
  ref = Ni_element
FEATURE [App::DocumentObjectGroupPython] G4_Ni  # scripted group (container) (typed FeaturePython)
  Dunit = g/cm3
  Dvalue = 8.902
  Group = -> [Ni_element001]
  conduct = 2
  density = 1
  expand = 3
  formula = Ni
  name = G4_Ni
  specific = 4
FEATURE [App::DocumentObjectGroupPython] Cu_element001  label="Cu_element : 1"  # scripted group (container) (typed FeaturePython)
  n = 1
  ref = Cu_element
FEATURE [App::DocumentObjectGroupPython] G4_Cu  # scripted group (container) (typed FeaturePython)
  Dunit = g/cm3
  Dvalue = 8.96
  Group = -> [Cu_element001]
  conduct = 2
  density = 1
  expand = 3
  formula = Cu
  name = G4_Cu
  specific = 4
FEATURE [App::DocumentObjectGroupPython] Zn_element001  label="Zn_element : 1"  # scripted group (container) (typed FeaturePython)
  n = 1
  ref = Zn_element
FEATURE [App::DocumentObjectGroupPython] G4_Zn  # scripted group (container) (typed FeaturePython)
  Dunit = g/cm3
  Dvalue = 7.133
  Group = -> [Zn_element001]
  conduct = 2
  density = 1
  expand = 3
  formula = Zn
  name = G4_Zn
  specific = 4
FEATURE [App::DocumentObjectGroupPython] Ga_element002  label="Ga_element : 002"  # scripted group (container) (typed FeaturePython)
  n = 1
  ref = Ga_element
FEATURE [App::DocumentObjectGroupPython] G4_Ga  # scripted group (container) (typed FeaturePython)
  Dunit = g/cm3
  Dvalue = 5.904
  Group = -> [Ga_element002]
  conduct = 2
  density = 1
  expand = 3
  formula = Ga
  name = G4_Ga
  specific = 4
FEATURE [App::DocumentObjectGroupPython] Ge_element002  label="Ge_element : 1"  # scripted group (container) (typed FeaturePython)
  n = 1
  ref = Ge_element
FEATURE [App::DocumentObjectGroupPython] G4_Ge  # scripted group (container) (typed FeaturePython)
  Dunit = g/cm3
  Dvalue = 5.323
  Group = -> [Ge_element002]
  conduct = 2
  density = 1
  expand = 3
  formula = Ge
  name = G4_Ge
  specific = 4
FEATURE [App::DocumentObjectGroupPython] As_element003  label="As_element : 002"  # scripted group (container) (typed FeaturePython)
  n = 1
  ref = As_element
FEATURE [App::DocumentObjectGroupPython] G4_As  # scripted group (container) (typed FeaturePython)
  Dunit = g/cm3
  Dvalue = 5.73
  Group = -> [As_element003]
  conduct = 2
  density = 1
  expand = 3
  formula = As
  name = G4_As
  specific = 4
FEATURE [App::DocumentObjectGroupPython] Se_element001  label="Se_element : 1"  # scripted group (container) (typed FeaturePython)
  n = 1
  ref = Se_element
FEATURE [App::DocumentObjectGroupPython] G4_Se  # scripted group (container) (typed FeaturePython)
  Dunit = g/cm3
  Dvalue = 4.5
  Group = -> [Se_element001]
  conduct = 2
  density = 1
  expand = 3
  formula = Se
  name = G4_Se
  specific = 4
FEATURE [App::DocumentObjectGroupPython] Br_element007  label="Br_element : 004"  # scripted group (container) (typed FeaturePython)
  n = 1
  ref = Br_element
FEATURE [App::DocumentObjectGroupPython] G4_Br  # scripted group (container) (typed FeaturePython)
  Dunit = g/cm3
  Dvalue = 0.0070721
  Group = -> [Br_element007]
  conduct = 2
  density = 1
  expand = 3
  formula = Br
  name = G4_Br
  specific = 4
FEATURE [App::DocumentObjectGroupPython] Kr_element001  label="Kr_element : 1"  # scripted group (container) (typed FeaturePython)
  n = 1
  ref = Kr_element
FEATURE [App::DocumentObjectGroupPython] G4_Kr  # scripted group (container) (typed FeaturePython)
  Dunit = g/cm3
  Dvalue = 0.00347832
  Group = -> [Kr_element001]
  conduct = 2
  density = 1
  expand = 3
  formula = Kr
  name = G4_Kr
  specific = 4
FEATURE [App::DocumentObjectGroupPython] Rb_element001  label="Rb_element : 1"  # scripted group (container) (typed FeaturePython)
  n = 1
  ref = Rb_element
FEATURE [App::DocumentObjectGroupPython] G4_Rb  # scripted group (container) (typed FeaturePython)
  Dunit = g/cm3
  Dvalue = 1.532
  Group = -> [Rb_element001]
  conduct = 2
  density = 1
  expand = 3
  formula = Rb
  name = G4_Rb
  specific = 4
FEATURE [App::DocumentObjectGroupPython] Sr_element001  label="Sr_element : 1"  # scripted group (container) (typed FeaturePython)
  n = 1
  ref = Sr_element
FEATURE [App::DocumentObjectGroupPython] G4_Sr  # scripted group (container) (typed FeaturePython)
  Dunit = g/cm3
  Dvalue = 2.54
  Group = -> [Sr_element001]
  conduct = 2
  density = 1
  expand = 3
  formula = Sr
  name = G4_Sr
  specific = 4
FEATURE [App::DocumentObjectGroupPython] Y_element001  label="Y_element : 1"  # scripted group (container) (typed FeaturePython)
  n = 1
  ref = Y_element
FEATURE [App::DocumentObjectGroupPython] G4_Y  # scripted group (container) (typed FeaturePython)
  Dunit = g/cm3
  Dvalue = 4.469
  Group = -> [Y_element001]
  conduct = 2
  density = 1
  expand = 3
  formula = Y
  name = G4_Y
  specific = 4
FEATURE [App::DocumentObjectGroupPython] Zr_element001  label="Zr_element : 1"  # scripted group (container) (typed FeaturePython)
  n = 1
  ref = Zr_element
FEATURE [App::DocumentObjectGroupPython] G4_Zr  # scripted group (container) (typed FeaturePython)
  Dunit = g/cm3
  Dvalue = 6.506
  Group = -> [Zr_element001]
  conduct = 2
  density = 1
  expand = 3
  formula = Zr
  name = G4_Zr
  specific = 4
FEATURE [App::DocumentObjectGroupPython] Nb_element001  label="Nb_element : 1"  # scripted group (container) (typed FeaturePython)
  n = 1
  ref = Nb_element
FEATURE [App::DocumentObjectGroupPython] G4_Nb  # scripted group (container) (typed FeaturePython)
  Dunit = g/cm3
  Dvalue = 8.57
  Group = -> [Nb_element001]
  conduct = 2
  density = 1
  expand = 3
  formula = Nb
  name = G4_Nb
  specific = 4
FEATURE [App::DocumentObjectGroupPython] Mo_element001  label="Mo_element : 1"  # scripted group (container) (typed FeaturePython)
  n = 1
  ref = Mo_element
FEATURE [App::DocumentObjectGroupPython] G4_Mo  # scripted group (container) (typed FeaturePython)
  Dunit = g/cm3
  Dvalue = 10.22
  Group = -> [Mo_element001]
  conduct = 2
  density = 1
  expand = 3
  formula = Mo
  name = G4_Mo
  specific = 4
FEATURE [App::DocumentObjectGroupPython] Tc_element001  label="Tc_element : 1"  # scripted group (container) (typed FeaturePython)
  n = 1
  ref = Tc_element
FEATURE [App::DocumentObjectGroupPython] G4_Tc  # scripted group (container) (typed FeaturePython)
  Dunit = g/cm3
  Dvalue = 11.5
  Group = -> [Tc_element001]
  conduct = 2
  density = 1
  expand = 3
  formula = Tc
  name = G4_Tc
  specific = 4
FEATURE [App::DocumentObjectGroupPython] Ru_element001  label="Ru_element : 1"  # scripted group (container) (typed FeaturePython)
  n = 1
  ref = Ru_element
FEATURE [App::DocumentObjectGroupPython] G4_Ru  # scripted group (container) (typed FeaturePython)
  Dunit = g/cm3
  Dvalue = 12.41
  Group = -> [Ru_element001]
  conduct = 2
  density = 1
  expand = 3
  formula = Ru
  name = G4_Ru
  specific = 4
FEATURE [App::DocumentObjectGroupPython] Rh_element001  label="Rh_element : 1"  # scripted group (container) (typed FeaturePython)
  n = 1
  ref = Rh_element
FEATURE [App::DocumentObjectGroupPython] G4_Rh  # scripted group (container) (typed FeaturePython)
  Dunit = g/cm3
  Dvalue = 12.41
  Group = -> [Rh_element001]
  conduct = 2
  density = 1
  expand = 3
  formula = Rh
  name = G4_Rh
  specific = 4
FEATURE [App::DocumentObjectGroupPython] Pd_element001  label="Pd_element : 1"  # scripted group (container) (typed FeaturePython)
  n = 1
  ref = Pd_element
FEATURE [App::DocumentObjectGroupPython] G4_Pd  # scripted group (container) (typed FeaturePython)
  Dunit = g/cm3
  Dvalue = 12.02
  Group = -> [Pd_element001]
  conduct = 2
  density = 1
  expand = 3
  formula = Pd
  name = G4_Pd
  specific = 4
FEATURE [App::DocumentObjectGroupPython] Ag_element006  label="Ag_element : 004"  # scripted group (container) (typed FeaturePython)
  n = 1
  ref = Ag_element
FEATURE [App::DocumentObjectGroupPython] G4_Ag  # scripted group (container) (typed FeaturePython)
  Dunit = g/cm3
  Dvalue = 10.5
  Group = -> [Ag_element006]
  conduct = 2
  density = 1
  expand = 3
  formula = Ag
  name = G4_Ag
  specific = 4
FEATURE [App::DocumentObjectGroupPython] Cd_element003  label="Cd_element : 003"  # scripted group (container) (typed FeaturePython)
  n = 1
  ref = Cd_element
FEATURE [App::DocumentObjectGroupPython] G4_Cd  # scripted group (container) (typed FeaturePython)
  Dunit = g/cm3
  Dvalue = 8.65
  Group = -> [Cd_element003]
  conduct = 2
  density = 1
  expand = 3
  formula = Cd
  name = G4_Cd
  specific = 4
FEATURE [App::DocumentObjectGroupPython] In_element001  label="In_element : 1"  # scripted group (container) (typed FeaturePython)
  n = 1
  ref = In_element
FEATURE [App::DocumentObjectGroupPython] G4_In  # scripted group (container) (typed FeaturePython)
  Dunit = g/cm3
  Dvalue = 7.31
  Group = -> [In_element001]
  conduct = 2
  density = 1
  expand = 3
  formula = In
  name = G4_In
  specific = 4
FEATURE [App::DocumentObjectGroupPython] Sn_element001  label="Sn_element : 1"  # scripted group (container) (typed FeaturePython)
  n = 1
  ref = Sn_element
FEATURE [App::DocumentObjectGroupPython] G4_Sn  # scripted group (container) (typed FeaturePython)
  Dunit = g/cm3
  Dvalue = 7.31
  Group = -> [Sn_element001]
  conduct = 2
  density = 1
  expand = 3
  formula = Sn
  name = G4_Sn
  specific = 4
FEATURE [App::DocumentObjectGroupPython] Sb_element001  label="Sb_element : 1"  # scripted group (container) (typed FeaturePython)
  n = 1
  ref = Sb_element
FEATURE [App::DocumentObjectGroupPython] G4_Sb  # scripted group (container) (typed FeaturePython)
  Dunit = g/cm3
  Dvalue = 6.691
  Group = -> [Sb_element001]
  conduct = 2
  density = 1
  expand = 3
  formula = Sb
  name = G4_Sb
  specific = 4
FEATURE [App::DocumentObjectGroupPython] Te_element002  label="Te_element : 002"  # scripted group (container) (typed FeaturePython)
  n = 1
  ref = Te_element
FEATURE [App::DocumentObjectGroupPython] G4_Te  # scripted group (container) (typed FeaturePython)
  Dunit = g/cm3
  Dvalue = 6.24
  Group = -> [Te_element002]
  conduct = 2
  density = 1
  expand = 3
  formula = Te
  name = G4_Te
  specific = 4
FEATURE [App::DocumentObjectGroupPython] I_element010  label="I_element : 006"  # scripted group (container) (typed FeaturePython)
  n = 1
  ref = I_element
FEATURE [App::DocumentObjectGroupPython] G4_I  # scripted group (container) (typed FeaturePython)
  Dunit = g/cm3
  Dvalue = 4.93
  Group = -> [I_element010]
  conduct = 2
  density = 1
  expand = 3
  formula = I
  name = G4_I
  specific = 4
FEATURE [App::DocumentObjectGroupPython] Xe_element001  label="Xe_element : 1"  # scripted group (container) (typed FeaturePython)
  n = 1
  ref = Xe_element
FEATURE [App::DocumentObjectGroupPython] G4_Xe  # scripted group (container) (typed FeaturePython)
  Dunit = g/cm3
  Dvalue = 0.00548536
  Group = -> [Xe_element001]
  conduct = 2
  density = 1
  expand = 3
  formula = Xe
  name = G4_Xe
  specific = 4
FEATURE [App::DocumentObjectGroupPython] Cs_element003  label="Cs_element : 003"  # scripted group (container) (typed FeaturePython)
  n = 1
  ref = Cs_element
FEATURE [App::DocumentObjectGroupPython] G4_Cs  # scripted group (container) (typed FeaturePython)
  Dunit = g/cm3
  Dvalue = 1.873
  Group = -> [Cs_element003]
  conduct = 2
  density = 1
  expand = 3
  formula = Cs
  name = G4_Cs
  specific = 4
FEATURE [App::DocumentObjectGroupPython] Ba_element003  label="Ba_element : 003"  # scripted group (container) (typed FeaturePython)
  n = 1
  ref = Ba_element
FEATURE [App::DocumentObjectGroupPython] G4_Ba  # scripted group (container) (typed FeaturePython)
  Dunit = g/cm3
  Dvalue = 3.5
  Group = -> [Ba_element003]
  conduct = 2
  density = 1
  expand = 3
  formula = Ba
  name = G4_Ba
  specific = 4
FEATURE [App::DocumentObjectGroupPython] La_element003  label="La_element : 003"  # scripted group (container) (typed FeaturePython)
  n = 1
  ref = La_element
FEATURE [App::DocumentObjectGroupPython] G4_La  # scripted group (container) (typed FeaturePython)
  Dunit = g/cm3
  Dvalue = 6.154
  Group = -> [La_element003]
  conduct = 2
  density = 1
  expand = 3
  formula = La
  name = G4_La
  specific = 4
FEATURE [App::DocumentObjectGroupPython] Ce_element002  label="Ce_element : 1"  # scripted group (container) (typed FeaturePython)
  n = 1
  ref = Ce_element
FEATURE [App::DocumentObjectGroupPython] G4_Ce  # scripted group (container) (typed FeaturePython)
  Dunit = g/cm3
  Dvalue = 6.657
  Group = -> [Ce_element002]
  conduct = 2
  density = 1
  expand = 3
  formula = Ce
  name = G4_Ce
  specific = 4
FEATURE [App::DocumentObjectGroupPython] Pr_element001  label="Pr_element : 1"  # scripted group (container) (typed FeaturePython)
  n = 1
  ref = Pr_element
FEATURE [App::DocumentObjectGroupPython] G4_Pr  # scripted group (container) (typed FeaturePython)
  Dunit = g/cm3
  Dvalue = 6.71
  Group = -> [Pr_element001]
  conduct = 2
  density = 1
  expand = 3
  formula = Pr
  name = G4_Pr
  specific = 4
FEATURE [App::DocumentObjectGroupPython] Nd_element001  label="Nd_element : 1"  # scripted group (container) (typed FeaturePython)
  n = 1
  ref = Nd_element
FEATURE [App::DocumentObjectGroupPython] G4_Nd  # scripted group (container) (typed FeaturePython)
  Dunit = g/cm3
  Dvalue = 6.9
  Group = -> [Nd_element001]
  conduct = 2
  density = 1
  expand = 3
  formula = Nd
  name = G4_Nd
  specific = 4
FEATURE [App::DocumentObjectGroupPython] Pm_element001  label="Pm_element : 1"  # scripted group (container) (typed FeaturePython)
  n = 1
  ref = Pm_element
FEATURE [App::DocumentObjectGroupPython] G4_Pm  # scripted group (container) (typed FeaturePython)
  Dunit = g/cm3
  Dvalue = 7.22
  Group = -> [Pm_element001]
  conduct = 2
  density = 1
  expand = 3
  formula = Pm
  name = G4_Pm
  specific = 4
FEATURE [App::DocumentObjectGroupPython] Sm_element001  label="Sm_element : 1"  # scripted group (container) (typed FeaturePython)
  n = 1
  ref = Sm_element
FEATURE [App::DocumentObjectGroupPython] G4_Sm  # scripted group (container) (typed FeaturePython)
  Dunit = g/cm3
  Dvalue = 7.46
  Group = -> [Sm_element001]
  conduct = 2
  density = 1
  expand = 3
  formula = Sm
  name = G4_Sm
  specific = 4
FEATURE [App::DocumentObjectGroupPython] Eu_element001  label="Eu_element : 1"  # scripted group (container) (typed FeaturePython)
  n = 1
  ref = Eu_element
FEATURE [App::DocumentObjectGroupPython] G4_Eu  # scripted group (container) (typed FeaturePython)
  Dunit = g/cm3
  Dvalue = 5.243
  Group = -> [Eu_element001]
  conduct = 2
  density = 1
  expand = 3
  formula = Eu
  name = G4_Eu
  specific = 4
FEATURE [App::DocumentObjectGroupPython] Gd_element002  label="Gd_element : 1"  # scripted group (container) (typed FeaturePython)
  n = 1
  ref = Gd_element
FEATURE [App::DocumentObjectGroupPython] G4_Gd  # scripted group (container) (typed FeaturePython)
  Dunit = g/cm3
  Dvalue = 7.9004
  Group = -> [Gd_element002]
  conduct = 2
  density = 1
  expand = 3
  formula = Gd
  name = G4_Gd
  specific = 4
FEATURE [App::DocumentObjectGroupPython] Tb_element001  label="Tb_element : 1"  # scripted group (container) (typed FeaturePython)
  n = 1
  ref = Tb_element
FEATURE [App::DocumentObjectGroupPython] G4_Tb  # scripted group (container) (typed FeaturePython)
  Dunit = g/cm3
  Dvalue = 8.229
  Group = -> [Tb_element001]
  conduct = 2
  density = 1
  expand = 3
  formula = Tb
  name = G4_Tb
  specific = 4
FEATURE [App::DocumentObjectGroupPython] Dy_element001  label="Dy_element : 1"  # scripted group (container) (typed FeaturePython)
  n = 1
  ref = Dy_element
FEATURE [App::DocumentObjectGroupPython] G4_Dy  # scripted group (container) (typed FeaturePython)
  Dunit = g/cm3
  Dvalue = 8.55
  Group = -> [Dy_element001]
  conduct = 2
  density = 1
  expand = 3
  formula = Dy
  name = G4_Dy
  specific = 4
FEATURE [App::DocumentObjectGroupPython] Ho_element001  label="Ho_element : 1"  # scripted group (container) (typed FeaturePython)
  n = 1
  ref = Ho_element
FEATURE [App::DocumentObjectGroupPython] G4_Ho  # scripted group (container) (typed FeaturePython)
  Dunit = g/cm3
  Dvalue = 8.795
  Group = -> [Ho_element001]
  conduct = 2
  density = 1
  expand = 3
  formula = Ho
  name = G4_Ho
  specific = 4
FEATURE [App::DocumentObjectGroupPython] Er_element001  label="Er_element : 1"  # scripted group (container) (typed FeaturePython)
  n = 1
  ref = Er_element
FEATURE [App::DocumentObjectGroupPython] G4_Er  # scripted group (container) (typed FeaturePython)
  Dunit = g/cm3
  Dvalue = 9.066
  Group = -> [Er_element001]
  conduct = 2
  density = 1
  expand = 3
  formula = Er
  name = G4_Er
  specific = 4
FEATURE [App::DocumentObjectGroupPython] Tm_element001  label="Tm_element : 1"  # scripted group (container) (typed FeaturePython)
  n = 1
  ref = Tm_element
FEATURE [App::DocumentObjectGroupPython] G4_Tm  # scripted group (container) (typed FeaturePython)
  Dunit = g/cm3
  Dvalue = 9.321
  Group = -> [Tm_element001]
  conduct = 2
  density = 1
  expand = 3
  formula = Tm
  name = G4_Tm
  specific = 4
FEATURE [App::DocumentObjectGroupPython] Yb_element001  label="Yb_element : 1"  # scripted group (container) (typed FeaturePython)
  n = 1
  ref = Yb_element
FEATURE [App::DocumentObjectGroupPython] G4_Yb  # scripted group (container) (typed FeaturePython)
  Dunit = g/cm3
  Dvalue = 6.73
  Group = -> [Yb_element001]
  conduct = 2
  density = 1
  expand = 3
  formula = Yb
  name = G4_Yb
  specific = 4
FEATURE [App::DocumentObjectGroupPython] Lu_element001  label="Lu_element : 1"  # scripted group (container) (typed FeaturePython)
  n = 1
  ref = Lu_element
FEATURE [App::DocumentObjectGroupPython] G4_Lu  # scripted group (container) (typed FeaturePython)
  Dunit = g/cm3
  Dvalue = 9.84
  Group = -> [Lu_element001]
  conduct = 2
  density = 1
  expand = 3
  formula = Lu
  name = G4_Lu
  specific = 4
FEATURE [App::DocumentObjectGroupPython] Hf_element001  label="Hf_element : 1"  # scripted group (container) (typed FeaturePython)
  n = 1
  ref = Hf_element
FEATURE [App::DocumentObjectGroupPython] G4_Hf  # scripted group (container) (typed FeaturePython)
  Dunit = g/cm3
  Dvalue = 13.31
  Group = -> [Hf_element001]
  conduct = 2
  density = 1
  expand = 3
  formula = Hf
  name = G4_Hf
  specific = 4
FEATURE [App::DocumentObjectGroupPython] Ta_element001  label="Ta_element : 1"  # scripted group (container) (typed FeaturePython)
  n = 1
  ref = Ta_element
FEATURE [App::DocumentObjectGroupPython] G4_Ta  # scripted group (container) (typed FeaturePython)
  Dunit = g/cm3
  Dvalue = 16.654
  Group = -> [Ta_element001]
  conduct = 2
  density = 1
  expand = 3
  formula = Ta
  name = G4_Ta
  specific = 4
FEATURE [App::DocumentObjectGroupPython] W_element004  label="W_element : 004"  # scripted group (container) (typed FeaturePython)
  n = 1
  ref = W_element
FEATURE [App::DocumentObjectGroupPython] G4_W  # scripted group (container) (typed FeaturePython)
  Dunit = g/cm3
  Dvalue = 19.3
  Group = -> [W_element004]
  conduct = 2
  density = 1
  expand = 3
  formula = W
  name = G4_W
  specific = 4
FEATURE [App::DocumentObjectGroupPython] Re_element001  label="Re_element : 1"  # scripted group (container) (typed FeaturePython)
  n = 1
  ref = Re_element
FEATURE [App::DocumentObjectGroupPython] G4_Re  # scripted group (container) (typed FeaturePython)
  Dunit = g/cm3
  Dvalue = 21.02
  Group = -> [Re_element001]
  conduct = 2
  density = 1
  expand = 3
  formula = Re
  name = G4_Re
  specific = 4
FEATURE [App::DocumentObjectGroupPython] Os_element001  label="Os_element : 1"  # scripted group (container) (typed FeaturePython)
  n = 1
  ref = Os_element
FEATURE [App::DocumentObjectGroupPython] G4_Os  # scripted group (container) (typed FeaturePython)
  Dunit = g/cm3
  Dvalue = 22.57
  Group = -> [Os_element001]
  conduct = 2
  density = 1
  expand = 3
  formula = Os
  name = G4_Os
  specific = 4
FEATURE [App::DocumentObjectGroupPython] Ir_element001  label="Ir_element : 1"  # scripted group (container) (typed FeaturePython)
  n = 1
  ref = Ir_element
FEATURE [App::DocumentObjectGroupPython] G4_Ir  # scripted group (container) (typed FeaturePython)
  Dunit = g/cm3
  Dvalue = 22.42
  Group = -> [Ir_element001]
  conduct = 2
  density = 1
  expand = 3
  formula = Ir
  name = G4_Ir
  specific = 4
FEATURE [App::DocumentObjectGroupPython] Pt_element001  label="Pt_element : 1"  # scripted group (container) (typed FeaturePython)
  n = 1
  ref = Pt_element
FEATURE [App::DocumentObjectGroupPython] G4_Pt  # scripted group (container) (typed FeaturePython)
  Dunit = g/cm3
  Dvalue = 21.45
  Group = -> [Pt_element001]
  conduct = 2
  density = 1
  expand = 3
  formula = Pt
  name = G4_Pt
  specific = 4
FEATURE [App::DocumentObjectGroupPython] Au_element001  label="Au_element : 1"  # scripted group (container) (typed FeaturePython)
  n = 1
  ref = Au_element
FEATURE [App::DocumentObjectGroupPython] G4_Au  # scripted group (container) (typed FeaturePython)
  Dunit = g/cm3
  Dvalue = 19.32
  Group = -> [Au_element001]
  conduct = 2
  density = 1
  expand = 3
  formula = Au
  name = G4_Au
  specific = 4
FEATURE [App::DocumentObjectGroupPython] Hg_element002  label="Hg_element : 002"  # scripted group (container) (typed FeaturePython)
  n = 1
  ref = Hg_element
FEATURE [App::DocumentObjectGroupPython] G4_Hg  # scripted group (container) (typed FeaturePython)
  Dunit = g/cm3
  Dvalue = 13.546
  Group = -> [Hg_element002]
  conduct = 2
  density = 1
  expand = 3
  formula = Hg
  name = G4_Hg
  specific = 4
FEATURE [App::DocumentObjectGroupPython] Tl_element002  label="Tl_element : 002"  # scripted group (container) (typed FeaturePython)
  n = 1
  ref = Tl_element
FEATURE [App::DocumentObjectGroupPython] G4_Tl  # scripted group (container) (typed FeaturePython)
  Dunit = g/cm3
  Dvalue = 11.72
  Group = -> [Tl_element002]
  conduct = 2
  density = 1
  expand = 3
  formula = Tl
  name = G4_Tl
  specific = 4
FEATURE [App::DocumentObjectGroupPython] Pb_element003  label="Pb_element : 1"  # scripted group (container) (typed FeaturePython)
  n = 1
  ref = Pb_element
FEATURE [App::DocumentObjectGroupPython] G4_Pb  # scripted group (container) (typed FeaturePython)
  Dunit = g/cm3
  Dvalue = 11.35
  Group = -> [Pb_element003]
  conduct = 2
  density = 1
  expand = 3
  formula = Pb
  name = G4_Pb
  specific = 4
FEATURE [App::DocumentObjectGroupPython] Bi_element002  label="Bi_element : 1"  # scripted group (container) (typed FeaturePython)
  n = 1
  ref = Bi_element
FEATURE [App::DocumentObjectGroupPython] G4_Bi  # scripted group (container) (typed FeaturePython)
  Dunit = g/cm3
  Dvalue = 9.747
  Group = -> [Bi_element002]
  conduct = 2
  density = 1
  expand = 3
  formula = Bi
  name = G4_Bi
  specific = 4
FEATURE [App::DocumentObjectGroupPython] Po_element001  label="Po_element : 1"  # scripted group (container) (typed FeaturePython)
  n = 1
  ref = Po_element
FEATURE [App::DocumentObjectGroupPython] G4_Po  # scripted group (container) (typed FeaturePython)
  Dunit = g/cm3
  Dvalue = 9.32
  Group = -> [Po_element001]
  conduct = 2
  density = 1
  expand = 3
  formula = Po
  name = G4_Po
  specific = 4
FEATURE [App::DocumentObjectGroupPython] At_element001  label="At_element : 1"  # scripted group (container) (typed FeaturePython)
  n = 1
  ref = At_element
FEATURE [App::DocumentObjectGroupPython] G4_At  # scripted group (container) (typed FeaturePython)
  Dunit = g/cm3
  Dvalue = 9.32
  Group = -> [At_element001]
  conduct = 2
  density = 1
  expand = 3
  formula = At
  name = G4_At
  specific = 4
FEATURE [App::DocumentObjectGroupPython] Rn_element001  label="Rn_element : 1"  # scripted group (container) (typed FeaturePython)
  n = 1
  ref = Rn_element
FEATURE [App::DocumentObjectGroupPython] G4_Rn  # scripted group (container) (typed FeaturePython)
  Dunit = g/cm3
  Dvalue = 0.00900662
  Group = -> [Rn_element001]
  conduct = 2
  density = 1
  expand = 3
  formula = Rn
  name = G4_Rn
  specific = 4
FEATURE [App::DocumentObjectGroupPython] Fr_element001  label="Fr_element : 1"  # scripted group (container) (typed FeaturePython)
  n = 1
  ref = Fr_element
FEATURE [App::DocumentObjectGroupPython] G4_Fr  # scripted group (container) (typed FeaturePython)
  Dunit = g/cm3
  Dvalue = 1
  Group = -> [Fr_element001]
  conduct = 2
  density = 1
  expand = 3
  formula = Fr
  name = G4_Fr
  specific = 4
FEATURE [App::DocumentObjectGroupPython] Ra_element001  label="Ra_element : 1"  # scripted group (container) (typed FeaturePython)
  n = 1
  ref = Ra_element
FEATURE [App::DocumentObjectGroupPython] G4_Ra  # scripted group (container) (typed FeaturePython)
  Dunit = g/cm3
  Dvalue = 5
  Group = -> [Ra_element001]
  conduct = 2
  density = 1
  expand = 3
  formula = Ra
  name = G4_Ra
  specific = 4
FEATURE [App::DocumentObjectGroupPython] Ac_element001  label="Ac_element : 1"  # scripted group (container) (typed FeaturePython)
  n = 1
  ref = Ac_element
FEATURE [App::DocumentObjectGroupPython] G4_Ac  # scripted group (container) (typed FeaturePython)
  Dunit = g/cm3
  Dvalue = 10.07
  Group = -> [Ac_element001]
  conduct = 2
  density = 1
  expand = 3
  formula = Ac
  name = G4_Ac
  specific = 4
FEATURE [App::DocumentObjectGroupPython] Th_element001  label="Th_element : 1"  # scripted group (container) (typed FeaturePython)
  n = 1
  ref = Th_element
FEATURE [App::DocumentObjectGroupPython] G4_Th  # scripted group (container) (typed FeaturePython)
  Dunit = g/cm3
  Dvalue = 11.72
  Group = -> [Th_element001]
  conduct = 2
  density = 1
  expand = 3
  formula = Th
  name = G4_Th
  specific = 4
FEATURE [App::DocumentObjectGroupPython] Pa_element001  label="Pa_element : 1"  # scripted group (container) (typed FeaturePython)
  n = 1
  ref = Pa_element
FEATURE [App::DocumentObjectGroupPython] G4_Pa  # scripted group (container) (typed FeaturePython)
  Dunit = g/cm3
  Dvalue = 15.37
  Group = -> [Pa_element001]
  conduct = 2
  density = 1
  expand = 3
  formula = Pa
  name = G4_Pa
  specific = 4
FEATURE [App::DocumentObjectGroupPython] U_element004  label="U_element : 004"  # scripted group (container) (typed FeaturePython)
  n = 1
  ref = U_element
FEATURE [App::DocumentObjectGroupPython] G4_U  # scripted group (container) (typed FeaturePython)
  Dunit = g/cm3
  Dvalue = 18.95
  Group = -> [U_element004]
  conduct = 2
  density = 1
  expand = 3
  formula = U
  name = G4_U
  specific = 4
FEATURE [App::DocumentObjectGroupPython] Np_element001  label="Np_element : 1"  # scripted group (container) (typed FeaturePython)
  n = 1
  ref = Np_element
FEATURE [App::DocumentObjectGroupPython] G4_Np  # scripted group (container) (typed FeaturePython)
  Dunit = g/cm3
  Dvalue = 20.25
  Group = -> [Np_element001]
  conduct = 2
  density = 1
  expand = 3
  formula = Np
  name = G4_Np
  specific = 4
FEATURE [App::DocumentObjectGroupPython] Pu_element002  label="Pu_element : 002"  # scripted group (container) (typed FeaturePython)
  n = 1
  ref = Pu_element
FEATURE [App::DocumentObjectGroupPython] G4_Pu  # scripted group (container) (typed FeaturePython)
  Dunit = g/cm3
  Dvalue = 19.84
  Group = -> [Pu_element002]
  conduct = 2
  density = 1
  expand = 3
  formula = Pu
  name = G4_Pu
  specific = 4
FEATURE [App::DocumentObjectGroupPython] Am_element001  label="Am_element : 1"  # scripted group (container) (typed FeaturePython)
  n = 1
  ref = Am_element
FEATURE [App::DocumentObjectGroupPython] G4_Am  # scripted group (container) (typed FeaturePython)
  Dunit = g/cm3
  Dvalue = 13.67
  Group = -> [Am_element001]
  conduct = 2
  density = 1
  expand = 3
  formula = Am
  name = G4_Am
  specific = 4
FEATURE [App::DocumentObjectGroupPython] Cm_element001  label="Cm_element : 1"  # scripted group (container) (typed FeaturePython)
  n = 1
  ref = Cm_element
FEATURE [App::DocumentObjectGroupPython] G4_Cm  # scripted group (container) (typed FeaturePython)
  Dunit = g/cm3
  Dvalue = 13.51
  Group = -> [Cm_element001]
  conduct = 2
  density = 1
  expand = 3
  formula = Cm
  name = G4_Cm
  specific = 4
FEATURE [App::DocumentObjectGroupPython] Bk_element001  label="Bk_element : 1"  # scripted group (container) (typed FeaturePython)
  n = 1
  ref = Bk_element
FEATURE [App::DocumentObjectGroupPython] G4_Bk  # scripted group (container) (typed FeaturePython)
  Dunit = g/cm3
  Dvalue = 14
  Group = -> [Bk_element001]
  conduct = 2
  density = 1
  expand = 3
  formula = Bk
  name = G4_Bk
  specific = 4
FEATURE [App::DocumentObjectGroupPython] Cf_element001  label="Cf_element : 1"  # scripted group (container) (typed FeaturePython)
  n = 1
  ref = Cf_element
FEATURE [App::DocumentObjectGroupPython] G4_Cf  # scripted group (container) (typed FeaturePython)
  Dunit = g/cm3
  Dvalue = 10
  Group = -> [Cf_element001]
  conduct = 2
  density = 1
  expand = 3
  formula = Cf
  name = G4_Cf
  specific = 4
FEATURE [App::DocumentObjectGroupPython] Element  # scripted group (container) (typed FeaturePython)
  Group = -> [G4_H,G4_He,G4_Li,G4_Be,G4_B,G4_C,G4_N,G4_O,G4_F,G4_Ne,G4_Na,G4_Mg,G4_Al,G4_Si,G4_P,G4_S,G4_Cl,G4_Ar,G4_K,G4_Ca,G4_Sc,G4_Ti,G4_V,G4_Cr,G4_Mn,G4_Fe,G4_Co,G4_Ni,G4_Cu,G4_Zn,G4_Ga,G4_Ge,G4_As,G4_Se,G4_Br,G4_Kr,G4_Rb,G4_Sr,G4_Y,G4_Zr,G4_Nb,G4_Mo,G4_Tc,G4_Ru,G4_Rh,G4_Pd,G4_Ag,G4_Cd,G4_In,G4_Sn,G4_Sb,G4_Te,G4_I,G4_Xe,G4_Cs,G4_Ba,G4_La,G4_Ce,G4_Pr,G4_Nd,G4_Pm,G4_Sm,G4_Eu,G4_Gd,G4_Tb,G4_Dy,G4_Ho,G4_Er,+30 more]
FEATURE [App::DocumentObjectGroupPython] H_element114  label="H_element : 063"  # scripted group (container) (typed FeaturePython)
  n = 2
  ref = H_element
FEATURE [App::DocumentObjectGroupPython] G4_lH2  # scripted group (container) (typed FeaturePython)
  Dunit = g/cm3
  Dvalue = 0.0708
  Group = -> [H_element114]
  conduct = 2
  density = 1
  expand = 3
  formula = G4_lH2
  name = G4_lH2
  specific = 4
FEATURE [App::DocumentObjectGroupPython] N_element049  label="N_element : 022"  # scripted group (container) (typed FeaturePython)
  n = 2
  ref = N_element
FEATURE [App::DocumentObjectGroupPython] G4_lN2  # scripted group (container) (typed FeaturePython)
  Dunit = g/cm3
  Dvalue = 0.807
  Group = -> [N_element049]
  conduct = 2
  density = 1
  expand = 3
  formula = G4_lN2
  name = G4_lN2
  specific = 4
FEATURE [App::DocumentObjectGroupPython] O_element106  label="O_element : 060"  # scripted group (container) (typed FeaturePython)
  n = 2
  ref = O_element
FEATURE [App::DocumentObjectGroupPython] G4_lO2  # scripted group (container) (typed FeaturePython)
  Dunit = g/cm3
  Dvalue = 1.141
  Group = -> [O_element106]
  conduct = 2
  density = 1
  expand = 3
  formula = G4_lO2
  name = G4_lO2
  specific = 4
FEATURE [App::DocumentObjectGroupPython] Ar  label="Ar : 1"  # scripted group (container) (typed FeaturePython)
  n = 1
  ref = Ar
FEATURE [App::DocumentObjectGroupPython] G4_lAr  # scripted group (container) (typed FeaturePython)
  Dunit = g/cm3
  Dvalue = 1.396
  Group = -> [Ar]
  conduct = 2
  density = 1
  expand = 3
  formula = G4_lAr
  name = G4_lAr
  specific = 4
FEATURE [App::DocumentObjectGroupPython] Br  label="Br : 1"  # scripted group (container) (typed FeaturePython)
  n = 1
  ref = Br
FEATURE [App::DocumentObjectGroupPython] G4_lBr  # scripted group (container) (typed FeaturePython)
  Dunit = g/cm3
  Dvalue = 3.1028
  Group = -> [Br]
  conduct = 2
  density = 1
  expand = 3
  formula = G4_lBr
  name = G4_lBr
  specific = 4
FEATURE [App::DocumentObjectGroupPython] Kr  label="Kr : 1"  # scripted group (container) (typed FeaturePython)
  n = 1
  ref = Kr
FEATURE [App::DocumentObjectGroupPython] G4_lKr  # scripted group (container) (typed FeaturePython)
  Dunit = g/cm3
  Dvalue = 2.418
  Group = -> [Kr]
  conduct = 2
  density = 1
  expand = 3
  formula = G4_lKr
  name = G4_lKr
  specific = 4
FEATURE [App::DocumentObjectGroupPython] Xe  label="Xe : 1"  # scripted group (container) (typed FeaturePython)
  n = 1
  ref = Xe
FEATURE [App::DocumentObjectGroupPython] G4_lXe  # scripted group (container) (typed FeaturePython)
  Dunit = g/cm3
  Dvalue = 2.953
  Group = -> [Xe]
  conduct = 2
  density = 1
  expand = 3
  formula = G4_lXe
  name = G4_lXe
  specific = 4
FEATURE [App::DocumentObjectGroupPython] O_element107  label="O_element : 061"  # scripted group (container) (typed FeaturePython)
  n = 4
  ref = O_element
FEATURE [App::DocumentObjectGroupPython] Pb_element004  label="Pb_element : 002"  # scripted group (container) (typed FeaturePython)
  n = 1
  ref = Pb_element
FEATURE [App::DocumentObjectGroupPython] W_element005  label="W_element : 005"  # scripted group (container) (typed FeaturePython)
  n = 1
  ref = W_element
FEATURE [App::DocumentObjectGroupPython] G4_PbWO4  # scripted group (container) (typed FeaturePython)
  Dunit = g/cm3
  Dvalue = 8.28
  Group = -> [O_element107,Pb_element004,W_element005]
  conduct = 2
  density = 1
  expand = 3
  formula = G4_PbWO4
  name = G4_PbWO4
  specific = 4
FEATURE [App::DocumentObjectGroupPython] alactic  label="alactic : 1"  # scripted group (container) (typed FeaturePython)
  n = 1
  ref = alactic
FEATURE [App::DocumentObjectGroupPython] G4_Galactic  # scripted group (container) (typed FeaturePython)
  Dunit = g/cm3
  Dvalue = 0
  Group = -> [alactic]
  conduct = 2
  density = 1
  expand = 3
  formula = G4_Galactic
  name = G4_Galactic
  specific = 4
FEATURE [App::DocumentObjectGroupPython] RAPHITE_POROUS  label="RAPHITE_POROUS : 1"  # scripted group (container) (typed FeaturePython)
  n = 1
  ref = RAPHITE_POROUS
FEATURE [App::DocumentObjectGroupPython] G4_GRAPHITE_POROUS  # scripted group (container) (typed FeaturePython)
  Dunit = g/cm3
  Dvalue = 1.7
  Group = -> [RAPHITE_POROUS]
  conduct = 2
  density = 1
  expand = 3
  formula = G4_GRAPHITE_POROUS
  name = G4_GRAPHITE_POROUS
  specific = 4
FEATURE [App::DocumentObjectGroupPython] H_element115  label="H_element : 0.150"  # scripted group (container) (typed FeaturePython)
  n = 0.080538
FEATURE [App::DocumentObjectGroupPython] C_element125  label="C_element : 0.600"  # scripted group (container) (typed FeaturePython)
  n = 0.599848
FEATURE [App::DocumentObjectGroupPython] O_element108  label="O_element : 0.320"  # scripted group (container) (typed FeaturePython)
  n = 0.319614
FEATURE [App::DocumentObjectGroupPython] G4_LUCITE  # scripted group (container) (typed FeaturePython)
  Dunit = g/cm3
  Dvalue = 1.19
  Group = -> [H_element115,C_element125,O_element108]
  conduct = 2
  density = 1
  expand = 3
  formula = G4_LUCITE
  name = G4_LUCITE
  specific = 4
FEATURE [App::DocumentObjectGroupPython] Cu_element002  label="Cu_element : 62"  # scripted group (container) (typed FeaturePython)
  n = 62
  ref = Cu_element
FEATURE [App::DocumentObjectGroupPython] Zn_element002  label="Zn_element : 35"  # scripted group (container) (typed FeaturePython)
  n = 35
  ref = Zn_element
FEATURE [App::DocumentObjectGroupPython] Pb_element005  label="Pb_element : 3"  # scripted group (container) (typed FeaturePython)
  n = 3
  ref = Pb_element
FEATURE [App::DocumentObjectGroupPython] G4_BRASS  # scripted group (container) (typed FeaturePython)
  Dunit = g/cm3
  Dvalue = 8.52
  Group = -> [Cu_element002,Zn_element002,Pb_element005]
  conduct = 2
  density = 1
  expand = 3
  formula = G4_BRASS
  name = G4_BRASS
  specific = 4
FEATURE [App::DocumentObjectGroupPython] Cu_element003  label="Cu_element : 89"  # scripted group (container) (typed FeaturePython)
  n = 89
  ref = Cu_element
FEATURE [App::DocumentObjectGroupPython] Zn_element003  label="Zn_element : 9"  # scripted group (container) (typed FeaturePython)
  n = 9
  ref = Zn_element
FEATURE [App::DocumentObjectGroupPython] Pb_element006  label="Pb_element : 2"  # scripted group (container) (typed FeaturePython)
  n = 2
  ref = Pb_element
FEATURE [App::DocumentObjectGroupPython] G4_BRONZE  # scripted group (container) (typed FeaturePython)
  Dunit = g/cm3
  Dvalue = 8.82
  Group = -> [Cu_element003,Zn_element003,Pb_element006]
  conduct = 2
  density = 1
  expand = 3
  formula = G4_BRONZE
  name = G4_BRONZE
  specific = 4
FEATURE [App::DocumentObjectGroupPython] Fe_element008  label="Fe_element : 74"  # scripted group (container) (typed FeaturePython)
  n = 74
  ref = Fe_element
FEATURE [App::DocumentObjectGroupPython] Cr_element002  label="Cr_element : 18"  # scripted group (container) (typed FeaturePython)
  n = 18
  ref = Cr_element
FEATURE [App::DocumentObjectGroupPython] Ni_element002  label="Ni_element : 8"  # scripted group (container) (typed FeaturePython)
  n = 8
  ref = Ni_element
FEATURE [App::DocumentObjectGroupPython] G4_STAINLESS_STEEL  label="G4_STAINLESS-STEEL"  # scripted group (container) (typed FeaturePython)
  Dunit = g/cm3
  Dvalue = 8
  Group = -> [Fe_element008,Cr_element002,Ni_element002]
  conduct = 2
  density = 1
  expand = 3
  formula = G4_STAINLESS-STEEL
  name = G4_STAINLESS-STEEL
  specific = 4
FEATURE [App::DocumentObjectGroupPython] H_element116  label="H_element : 064"  # scripted group (container) (typed FeaturePython)
  n = 18
  ref = H_element
FEATURE [App::DocumentObjectGroupPython] C_element126  label="C_element : 071"  # scripted group (container) (typed FeaturePython)
  n = 12
  ref = C_element
FEATURE [App::DocumentObjectGroupPython] O_element109  label="O_element : 062"  # scripted group (container) (typed FeaturePython)
  n = 7
  ref = O_element
FEATURE [App::DocumentObjectGroupPython] G4_CR39  # scripted group (container) (typed FeaturePython)
  Dunit = g/cm3
  Dvalue = 1.32
  Group = -> [H_element116,C_element126,O_element109]
  conduct = 2
  density = 1
  expand = 3
  formula = G4_CR39
  name = G4_CR39
  specific = 4
FEATURE [App::DocumentObjectGroupPython] H_element117  label="H_element : 38"  # scripted group (container) (typed FeaturePython)
  n = 38
  ref = H_element
FEATURE [App::DocumentObjectGroupPython] C_element127  label="C_element : 072"  # scripted group (container) (typed FeaturePython)
  n = 18
  ref = C_element
FEATURE [App::DocumentObjectGroupPython] O_element110  label="O_element : 063"  # scripted group (container) (typed FeaturePython)
  n = 1
  ref = O_element
FEATURE [App::DocumentObjectGroupPython] G4_OCTADECANOL  # scripted group (container) (typed FeaturePython)
  Dunit = g/cm3
  Dvalue = 0.812
  Group = -> [H_element117,C_element127,O_element110]
  conduct = 2
  density = 1
  expand = 3
  formula = G4_OCTADECANOL
  name = G4_OCTADECANOL
  specific = 4
FEATURE [App::DocumentObjectGroupPython] HEP  # scripted group (container) (typed FeaturePython)
  Group = -> [G4_lH2,G4_lN2,G4_lO2,G4_lAr,G4_lBr,G4_lKr,G4_lXe,G4_PbWO4,G4_Galactic,G4_GRAPHITE_POROUS,G4_LUCITE,G4_BRASS,G4_BRONZE,G4_STAINLESS_STEEL,G4_CR39,G4_OCTADECANOL]
FEATURE [App::DocumentObjectGroupPython] C_element128  label="C_element : 073"  # scripted group (container) (typed FeaturePython)
  n = 14
  ref = C_element
FEATURE [App::DocumentObjectGroupPython] H_element118  label="H_element : 065"  # scripted group (container) (typed FeaturePython)
  n = 10
  ref = H_element
FEATURE [App::DocumentObjectGroupPython] O_element111  label="O_element : 064"  # scripted group (container) (typed FeaturePython)
  n = 2
  ref = O_element
FEATURE [App::DocumentObjectGroupPython] N_element050  label="N_element : 023"  # scripted group (container) (typed FeaturePython)
  n = 2
  ref = N_element
FEATURE [App::DocumentObjectGroupPython] G4_KEVLAR  # scripted group (container) (typed FeaturePython)
  Dunit = g/cm3
  Dvalue = 1.44
  Group = -> [C_element128,H_element118,O_element111,N_element050]
  conduct = 2
  density = 1
  expand = 3
  formula = G4_KEVLAR
  name = G4_KEVLAR
  specific = 4
FEATURE [App::DocumentObjectGroupPython] C_element129  label="C_element : 074"  # scripted group (container) (typed FeaturePython)
  n = 10
  ref = C_element
FEATURE [App::DocumentObjectGroupPython] H_element119  label="H_element : 066"  # scripted group (container) (typed FeaturePython)
  n = 8
  ref = H_element
FEATURE [App::DocumentObjectGroupPython] O_element112  label="O_element : 065"  # scripted group (container) (typed FeaturePython)
  n = 4
  ref = O_element
FEATURE [App::DocumentObjectGroupPython] G4_DACRON  # scripted group (container) (typed FeaturePython)
  Dunit = g/cm3
  Dvalue = 1.4
  Group = -> [C_element129,H_element119,O_element112]
  conduct = 2
  density = 1
  expand = 3
  formula = G4_DACRON
  name = G4_DACRON
  specific = 4
FEATURE [App::DocumentObjectGroupPython] C_element130  label="C_element : 075"  # scripted group (container) (typed FeaturePython)
  n = 4
  ref = C_element
FEATURE [App::DocumentObjectGroupPython] H_element120  label="H_element : 067"  # scripted group (container) (typed FeaturePython)
  n = 5
  ref = H_element
FEATURE [App::DocumentObjectGroupPython] Cl_element030  label="Cl_element : 016"  # scripted group (container) (typed FeaturePython)
  n = 1
  ref = Cl_element
FEATURE [App::DocumentObjectGroupPython] G4_NEOPRENE  # scripted group (container) (typed FeaturePython)
  Dunit = g/cm3
  Dvalue = 1.23
  Group = -> [C_element130,H_element120,Cl_element030]
  conduct = 2
  density = 1
  expand = 3
  formula = G4_NEOPRENE
  name = G4_NEOPRENE
  specific = 4
FEATURE [App::DocumentObjectGroupPython] Space  # scripted group (container) (typed FeaturePython)
  Group = -> [G4_KEVLAR,G4_DACRON,G4_NEOPRENE]
FEATURE [App::DocumentObjectGroupPython] H_element121  label="H_element : 068"  # scripted group (container) (typed FeaturePython)
  n = 5
  ref = H_element
FEATURE [App::DocumentObjectGroupPython] C_element131  label="C_element : 076"  # scripted group (container) (typed FeaturePython)
  n = 4
  ref = C_element
FEATURE [App::DocumentObjectGroupPython] N_element051  label="N_element : 3"  # scripted group (container) (typed FeaturePython)
  n = 3
  ref = N_element
FEATURE [App::DocumentObjectGroupPython] O_element113  label="O_element : 066"  # scripted group (container) (typed FeaturePython)
  n = 1
  ref = O_element
FEATURE [App::DocumentObjectGroupPython] G4_CYTOSINE  # scripted group (container) (typed FeaturePython)
  Dunit = g/cm3
  Dvalue = 1.55
  Group = -> [H_element121,C_element131,N_element051,O_element113]
  conduct = 2
  density = 1
  expand = 3
  formula = G4_CYTOSINE
  name = G4_CYTOSINE
  specific = 4
FEATURE [App::DocumentObjectGroupPython] H_element122  label="H_element : 069"  # scripted group (container) (typed FeaturePython)
  n = 6
  ref = H_element
FEATURE [App::DocumentObjectGroupPython] C_element132  label="C_element : 077"  # scripted group (container) (typed FeaturePython)
  n = 5
  ref = C_element
FEATURE [App::DocumentObjectGroupPython] N_element052  label="N_element : 024"  # scripted group (container) (typed FeaturePython)
  n = 2
  ref = N_element
FEATURE [App::DocumentObjectGroupPython] O_element114  label="O_element : 067"  # scripted group (container) (typed FeaturePython)
  n = 2
  ref = O_element
FEATURE [App::DocumentObjectGroupPython] G4_THYMINE  # scripted group (container) (typed FeaturePython)
  Dunit = g/cm3
  Dvalue = 1.23
  Group = -> [H_element122,C_element132,N_element052,O_element114]
  conduct = 2
  density = 1
  expand = 3
  formula = G4_THYMINE
  name = G4_THYMINE
  specific = 4
FEATURE [App::DocumentObjectGroupPython] H_element123  label="H_element : 070"  # scripted group (container) (typed FeaturePython)
  n = 4
  ref = H_element
FEATURE [App::DocumentObjectGroupPython] C_element133  label="C_element : 078"  # scripted group (container) (typed FeaturePython)
  n = 4
  ref = C_element
FEATURE [App::DocumentObjectGroupPython] N_element053  label="N_element : 025"  # scripted group (container) (typed FeaturePython)
  n = 2
  ref = N_element
FEATURE [App::DocumentObjectGroupPython] O_element115  label="O_element : 068"  # scripted group (container) (typed FeaturePython)
  n = 2
  ref = O_element
FEATURE [App::DocumentObjectGroupPython] G4_URACIL  # scripted group (container) (typed FeaturePython)
  Dunit = g/cm3
  Dvalue = 1.32
  Group = -> [H_element123,C_element133,N_element053,O_element115]
  conduct = 2
  density = 1
  expand = 3
  formula = G4_URACIL
  name = G4_URACIL
  specific = 4
FEATURE [App::DocumentObjectGroupPython] H_element124  label="H_element : 071"  # scripted group (container) (typed FeaturePython)
  n = 4
  ref = H_element
FEATURE [App::DocumentObjectGroupPython] C_element134  label="C_element : 079"  # scripted group (container) (typed FeaturePython)
  n = 5
  ref = C_element
FEATURE [App::DocumentObjectGroupPython] N_element054  label="N_element : 026"  # scripted group (container) (typed FeaturePython)
  n = 5
  ref = N_element
FEATURE [App::DocumentObjectGroupPython] G4_DNA_ADENINE  # scripted group (container) (typed FeaturePython)
  Dunit = g/cm3
  Dvalue = 1
  Group = -> [H_element124,C_element134,N_element054]
  conduct = 2
  density = 1
  expand = 3
  formula = G4_DNA_ADENINE
  name = G4_DNA_ADENINE
  specific = 4
FEATURE [App::DocumentObjectGroupPython] H_element125  label="H_element : 072"  # scripted group (container) (typed FeaturePython)
  n = 4
  ref = H_element
FEATURE [App::DocumentObjectGroupPython] C_element135  label="C_element : 080"  # scripted group (container) (typed FeaturePython)
  n = 5
  ref = C_element
FEATURE [App::DocumentObjectGroupPython] N_element055  label="N_element : 027"  # scripted group (container) (typed FeaturePython)
  n = 5
  ref = N_element
FEATURE [App::DocumentObjectGroupPython] O_element116  label="O_element : 069"  # scripted group (container) (typed FeaturePython)
  n = 1
  ref = O_element
FEATURE [App::DocumentObjectGroupPython] G4_DNA_GUANINE  # scripted group (container) (typed FeaturePython)
  Dunit = g/cm3
  Dvalue = 1
  Group = -> [H_element125,C_element135,N_element055,O_element116]
  conduct = 2
  density = 1
  expand = 3
  formula = G4_DNA_GUANINE
  name = G4_DNA_GUANINE
  specific = 4
FEATURE [App::DocumentObjectGroupPython] H_element126  label="H_element : 073"  # scripted group (container) (typed FeaturePython)
  n = 4
  ref = H_element
FEATURE [App::DocumentObjectGroupPython] C_element136  label="C_element : 081"  # scripted group (container) (typed FeaturePython)
  n = 4
  ref = C_element
FEATURE [App::DocumentObjectGroupPython] N_element056  label="N_element : 028"  # scripted group (container) (typed FeaturePython)
  n = 3
  ref = N_element
FEATURE [App::DocumentObjectGroupPython] O_element117  label="O_element : 070"  # scripted group (container) (typed FeaturePython)
  n = 1
  ref = O_element
FEATURE [App::DocumentObjectGroupPython] G4_DNA_CYTOSINE  # scripted group (container) (typed FeaturePython)
  Dunit = g/cm3
  Dvalue = 1
  Group = -> [H_element126,C_element136,N_element056,O_element117]
  conduct = 2
  density = 1
  expand = 3
  formula = G4_DNA_CYTOSINE
  name = G4_DNA_CYTOSINE
  specific = 4
FEATURE [App::DocumentObjectGroupPython] H_element127  label="H_element : 074"  # scripted group (container) (typed FeaturePython)
  n = 5
  ref = H_element
FEATURE [App::DocumentObjectGroupPython] C_element137  label="C_element : 082"  # scripted group (container) (typed FeaturePython)
  n = 5
  ref = C_element
FEATURE [App::DocumentObjectGroupPython] N_element057  label="N_element : 029"  # scripted group (container) (typed FeaturePython)
  n = 2
  ref = N_element
FEATURE [App::DocumentObjectGroupPython] O_element118  label="O_element : 071"  # scripted group (container) (typed FeaturePython)
  n = 2
  ref = O_element
FEATURE [App::DocumentObjectGroupPython] G4_DNA_THYMINE  # scripted group (container) (typed FeaturePython)
  Dunit = g/cm3
  Dvalue = 1
  Group = -> [H_element127,C_element137,N_element057,O_element118]
  conduct = 2
  density = 1
  expand = 3
  formula = G4_DNA_THYMINE
  name = G4_DNA_THYMINE
  specific = 4
FEATURE [App::DocumentObjectGroupPython] H_element128  label="H_element : 075"  # scripted group (container) (typed FeaturePython)
  n = 3
  ref = H_element
FEATURE [App::DocumentObjectGroupPython] C_element138  label="C_element : 083"  # scripted group (container) (typed FeaturePython)
  n = 4
  ref = C_element
FEATURE [App::DocumentObjectGroupPython] N_element058  label="N_element : 030"  # scripted group (container) (typed FeaturePython)
  n = 2
  ref = N_element
FEATURE [App::DocumentObjectGroupPython] O_element119  label="O_element : 072"  # scripted group (container) (typed FeaturePython)
  n = 2
  ref = O_element
FEATURE [App::DocumentObjectGroupPython] G4_DNA_URACIL  # scripted group (container) (typed FeaturePython)
  Dunit = g/cm3
  Dvalue = 1
  Group = -> [H_element128,C_element138,N_element058,O_element119]
  conduct = 2
  density = 1
  expand = 3
  formula = G4_DNA_URACIL
  name = G4_DNA_URACIL
  specific = 4
FEATURE [App::DocumentObjectGroupPython] H_element129  label="H_element : 076"  # scripted group (container) (typed FeaturePython)
  n = 10
  ref = H_element
FEATURE [App::DocumentObjectGroupPython] C_element139  label="C_element : 084"  # scripted group (container) (typed FeaturePython)
  n = 10
  ref = C_element
FEATURE [App::DocumentObjectGroupPython] N_element059  label="N_element : 031"  # scripted group (container) (typed FeaturePython)
  n = 5
  ref = N_element
FEATURE [App::DocumentObjectGroupPython] O_element120  label="O_element : 073"  # scripted group (container) (typed FeaturePython)
  n = 4
  ref = O_element
FEATURE [App::DocumentObjectGroupPython] G4_DNA_ADENOSINE  # scripted group (container) (typed FeaturePython)
  Dunit = g/cm3
  Dvalue = 1
  Group = -> [H_element129,C_element139,N_element059,O_element120]
  conduct = 2
  density = 1
  expand = 3
  formula = G4_DNA_ADENOSINE
  name = G4_DNA_ADENOSINE
  specific = 4
FEATURE [App::DocumentObjectGroupPython] H_element130  label="H_element : 077"  # scripted group (container) (typed FeaturePython)
  n = 10
  ref = H_element
FEATURE [App::DocumentObjectGroupPython] C_element140  label="C_element : 085"  # scripted group (container) (typed FeaturePython)
  n = 10
  ref = C_element
FEATURE [App::DocumentObjectGroupPython] N_element060  label="N_element : 032"  # scripted group (container) (typed FeaturePython)
  n = 5
  ref = N_element
FEATURE [App::DocumentObjectGroupPython] O_element121  label="O_element : 074"  # scripted group (container) (typed FeaturePython)
  n = 5
  ref = O_element
FEATURE [App::DocumentObjectGroupPython] G4_DNA_GUANOSINE  # scripted group (container) (typed FeaturePython)
  Dunit = g/cm3
  Dvalue = 1
  Group = -> [H_element130,C_element140,N_element060,O_element121]
  conduct = 2
  density = 1
  expand = 3
  formula = G4_DNA_GUANOSINE
  name = G4_DNA_GUANOSINE
  specific = 4
FEATURE [App::DocumentObjectGroupPython] H_element131  label="H_element : 078"  # scripted group (container) (typed FeaturePython)
  n = 10
  ref = H_element
FEATURE [App::DocumentObjectGroupPython] C_element141  label="C_element : 086"  # scripted group (container) (typed FeaturePython)
  n = 9
  ref = C_element
FEATURE [App::DocumentObjectGroupPython] N_element061  label="N_element : 033"  # scripted group (container) (typed FeaturePython)
  n = 3
  ref = N_element
FEATURE [App::DocumentObjectGroupPython] O_element122  label="O_element : 075"  # scripted group (container) (typed FeaturePython)
  n = 5
  ref = O_element
FEATURE [App::DocumentObjectGroupPython] G4_DNA_CYTIDINE  # scripted group (container) (typed FeaturePython)
  Dunit = g/cm3
  Dvalue = 1
  Group = -> [H_element131,C_element141,N_element061,O_element122]
  conduct = 2
  density = 1
  expand = 3
  formula = G4_DNA_CYTIDINE
  name = G4_DNA_CYTIDINE
  specific = 4
FEATURE [App::DocumentObjectGroupPython] H_element132  label="H_element : 079"  # scripted group (container) (typed FeaturePython)
  n = 9
  ref = H_element
FEATURE [App::DocumentObjectGroupPython] C_element142  label="C_element : 087"  # scripted group (container) (typed FeaturePython)
  n = 9
  ref = C_element
FEATURE [App::DocumentObjectGroupPython] N_element062  label="N_element : 034"  # scripted group (container) (typed FeaturePython)
  n = 2
  ref = N_element
FEATURE [App::DocumentObjectGroupPython] O_element123  label="O_element : 076"  # scripted group (container) (typed FeaturePython)
  n = 6
  ref = O_element
FEATURE [App::DocumentObjectGroupPython] G4_DNA_URIDINE  # scripted group (container) (typed FeaturePython)
  Dunit = g/cm3
  Dvalue = 1
  Group = -> [H_element132,C_element142,N_element062,O_element123]
  conduct = 2
  density = 1
  expand = 3
  formula = G4_DNA_URIDINE
  name = G4_DNA_URIDINE
  specific = 4
FEATURE [App::DocumentObjectGroupPython] H_element133  label="H_element : 080"  # scripted group (container) (typed FeaturePython)
  n = 11
  ref = H_element
FEATURE [App::DocumentObjectGroupPython] C_element143  label="C_element : 088"  # scripted group (container) (typed FeaturePython)
  n = 10
  ref = C_element
FEATURE [App::DocumentObjectGroupPython] N_element063  label="N_element : 035"  # scripted group (container) (typed FeaturePython)
  n = 2
  ref = N_element
FEATURE [App::DocumentObjectGroupPython] O_element124  label="O_element : 077"  # scripted group (container) (typed FeaturePython)
  n = 6
  ref = O_element
FEATURE [App::DocumentObjectGroupPython] G4_DNA_METHYLURIDINE  # scripted group (container) (typed FeaturePython)
  Dunit = g/cm3
  Dvalue = 1
  Group = -> [H_element133,C_element143,N_element063,O_element124]
  conduct = 2
  density = 1
  expand = 3
  formula = G4_DNA_METHYLURIDINE
  name = G4_DNA_METHYLURIDINE
  specific = 4
FEATURE [App::DocumentObjectGroupPython] P_element014  label="P_element : 003"  # scripted group (container) (typed FeaturePython)
  n = 1
  ref = P_element
FEATURE [App::DocumentObjectGroupPython] O_element125  label="O_element : 078"  # scripted group (container) (typed FeaturePython)
  n = 3
  ref = O_element
FEATURE [App::DocumentObjectGroupPython] G4_DNA_MONOPHOSPHATE  # scripted group (container) (typed FeaturePython)
  Dunit = g/cm3
  Dvalue = 1
  Group = -> [P_element014,O_element125]
  conduct = 2
  density = 1
  expand = 3
  formula = G4_DNA_MONOPHOSPHATE
  name = G4_DNA_MONOPHOSPHATE
  specific = 4
FEATURE [App::DocumentObjectGroupPython] H_element134  label="H_element : 081"  # scripted group (container) (typed FeaturePython)
  n = 10
  ref = H_element
FEATURE [App::DocumentObjectGroupPython] C_element144  label="C_element : 089"  # scripted group (container) (typed FeaturePython)
  n = 10
  ref = C_element
FEATURE [App::DocumentObjectGroupPython] N_element064  label="N_element : 036"  # scripted group (container) (typed FeaturePython)
  n = 5
  ref = N_element
FEATURE [App::DocumentObjectGroupPython] O_element126  label="O_element : 079"  # scripted group (container) (typed FeaturePython)
  n = 7
  ref = O_element
FEATURE [App::DocumentObjectGroupPython] P_element015  label="P_element : 004"  # scripted group (container) (typed FeaturePython)
  n = 1
  ref = P_element
FEATURE [App::DocumentObjectGroupPython] G4_DNA_A  # scripted group (container) (typed FeaturePython)
  Dunit = g/cm3
  Dvalue = 1
  Group = -> [H_element134,C_element144,N_element064,O_element126,P_element015]
  conduct = 2
  density = 1
  expand = 3
  formula = G4_DNA_A
  name = G4_DNA_A
  specific = 4
FEATURE [App::DocumentObjectGroupPython] H_element135  label="H_element : 082"  # scripted group (container) (typed FeaturePython)
  n = 10
  ref = H_element
FEATURE [App::DocumentObjectGroupPython] C_element145  label="C_element : 090"  # scripted group (container) (typed FeaturePython)
  n = 10
  ref = C_element
FEATURE [App::DocumentObjectGroupPython] N_element065  label="N_element : 037"  # scripted group (container) (typed FeaturePython)
  n = 5
  ref = N_element
FEATURE [App::DocumentObjectGroupPython] O_element127  label="O_element : 8"  # scripted group (container) (typed FeaturePython)
  n = 8
  ref = O_element
FEATURE [App::DocumentObjectGroupPython] P_element016  label="P_element : 005"  # scripted group (container) (typed FeaturePython)
  n = 1
  ref = P_element
FEATURE [App::DocumentObjectGroupPython] G4_DNA_G  # scripted group (container) (typed FeaturePython)
  Dunit = g/cm3
  Dvalue = 1
  Group = -> [H_element135,C_element145,N_element065,O_element127,P_element016]
  conduct = 2
  density = 1
  expand = 3
  formula = G4_DNA_G
  name = G4_DNA_G
  specific = 4
FEATURE [App::DocumentObjectGroupPython] H_element136  label="H_element : 083"  # scripted group (container) (typed FeaturePython)
  n = 10
  ref = H_element
FEATURE [App::DocumentObjectGroupPython] C_element146  label="C_element : 091"  # scripted group (container) (typed FeaturePython)
  n = 9
  ref = C_element
FEATURE [App::DocumentObjectGroupPython] N_element066  label="N_element : 038"  # scripted group (container) (typed FeaturePython)
  n = 3
  ref = N_element
FEATURE [App::DocumentObjectGroupPython] O_element128  label="O_element : 080"  # scripted group (container) (typed FeaturePython)
  n = 8
  ref = O_element
FEATURE [App::DocumentObjectGroupPython] P_element017  label="P_element : 006"  # scripted group (container) (typed FeaturePython)
  n = 1
  ref = P_element
FEATURE [App::DocumentObjectGroupPython] G4_DNA_C  # scripted group (container) (typed FeaturePython)
  Dunit = g/cm3
  Dvalue = 1
  Group = -> [H_element136,C_element146,N_element066,O_element128,P_element017]
  conduct = 2
  density = 1
  expand = 3
  formula = G4_DNA_C
  name = G4_DNA_C
  specific = 4
FEATURE [App::DocumentObjectGroupPython] H_element137  label="H_element : 084"  # scripted group (container) (typed FeaturePython)
  n = 9
  ref = H_element
FEATURE [App::DocumentObjectGroupPython] C_element147  label="C_element : 092"  # scripted group (container) (typed FeaturePython)
  n = 9
  ref = C_element
FEATURE [App::DocumentObjectGroupPython] N_element067  label="N_element : 039"  # scripted group (container) (typed FeaturePython)
  n = 2
  ref = N_element
FEATURE [App::DocumentObjectGroupPython] O_element129  label="O_element : 9"  # scripted group (container) (typed FeaturePython)
  n = 9
  ref = O_element
FEATURE [App::DocumentObjectGroupPython] P_element018  label="P_element : 007"  # scripted group (container) (typed FeaturePython)
  n = 1
  ref = P_element
FEATURE [App::DocumentObjectGroupPython] G4_DNA_U  # scripted group (container) (typed FeaturePython)
  Dunit = g/cm3
  Dvalue = 1
  Group = -> [H_element137,C_element147,N_element067,O_element129,P_element018]
  conduct = 2
  density = 1
  expand = 3
  formula = G4_DNA_U
  name = G4_DNA_U
  specific = 4
FEATURE [App::DocumentObjectGroupPython] H_element138  label="H_element : 085"  # scripted group (container) (typed FeaturePython)
  n = 11
  ref = H_element
FEATURE [App::DocumentObjectGroupPython] C_element148  label="C_element : 093"  # scripted group (container) (typed FeaturePython)
  n = 10
  ref = C_element
FEATURE [App::DocumentObjectGroupPython] N_element068  label="N_element : 040"  # scripted group (container) (typed FeaturePython)
  n = 2
  ref = N_element
FEATURE [App::DocumentObjectGroupPython] O_element130  label="O_element : 081"  # scripted group (container) (typed FeaturePython)
  n = 9
  ref = O_element
FEATURE [App::DocumentObjectGroupPython] P_element019  label="P_element : 008"  # scripted group (container) (typed FeaturePython)
  n = 1
  ref = P_element
FEATURE [App::DocumentObjectGroupPython] G4_DNA_MU  # scripted group (container) (typed FeaturePython)
  Dunit = g/cm3
  Dvalue = 1
  Group = -> [H_element138,C_element148,N_element068,O_element130,P_element019]
  conduct = 2
  density = 1
  expand = 3
  formula = G4_DNA_MU
  name = G4_DNA_MU
  specific = 4
FEATURE [App::DocumentObjectGroupPython] BioChemical  # scripted group (container) (typed FeaturePython)
  Group = -> [G4_CYTOSINE,G4_THYMINE,G4_URACIL,G4_DNA_ADENINE,G4_DNA_GUANINE,G4_DNA_CYTOSINE,G4_DNA_THYMINE,G4_DNA_URACIL,G4_DNA_ADENOSINE,G4_DNA_GUANOSINE,G4_DNA_CYTIDINE,G4_DNA_URIDINE,G4_DNA_METHYLURIDINE,G4_DNA_MONOPHOSPHATE,G4_DNA_A,G4_DNA_G,G4_DNA_C,G4_DNA_U,G4_DNA_MU]
FEATURE [App::DocumentObjectGroupPython] G4Materials  # scripted group (container) (typed FeaturePython)
  Group = -> [NIST,Element,HEP,Space,BioChemical]
  version = 1
FEATURE [App::DocumentObjectGroupPython] Geant4  # scripted group (container) (typed FeaturePython)
  Group = -> [G4Isotopes,G4Elements,G4Materials]
FEATURE [App::DocumentObjectGroupPython] Materials  # scripted group (container) (typed FeaturePython)
  Group = -> [Geant4]
FEATURE [Part::FeaturePython] GDMLBox_WorldBox  # WARN: FeaturePython — macro-defined, semantics opaque (R4)
  lunit = 2
  material = 5
  x = 26
  y = 27.5772
  z = 33.0792
FEATURE [Part::Cone] Cone
  Angle = 360
  AttacherType = Attacher::AttachEngine3D
  Height = 2
  Radius1 = 0
  Radius2 = 1
FEATURE [Part::Vertex] Vertex
  AttacherType = Attacher::AttachEngine3D
  Placement = pos=(5,0,0) rot=(0,0,1;0.349066rad)
  X = 0
  Y = 0
  Z = 0
FEATURE [Part::Vertex] Vertex001
  AttacherType = Attacher::AttachEngine3D
  Placement = pos=(5,5,0) rot=(0,0,1;0rad)
  X = 0
  Y = 0
  Z = 0
FEATURE [Part::Vertex] Vertex002
  AttacherType = Attacher::AttachEngine3D
  Placement = pos=(3,3,0) rot=(0,0,1;0rad)
  X = 0
  Y = 0
  Z = 0
FEATURE [Part::Vertex] Vertex003
  AttacherType = Attacher::AttachEngine3D
  X = 0
  Y = 0
  Z = 0
FEATURE [Part::Vertex] Vertex004
  AttacherType = Attacher::AttachEngine3D
  Placement = pos=(0,4,0) rot=(0,0,1;0rad)
  X = 0
  Y = 0
  Z = 0
FEATURE [Part::Compound] Compound
  Links = -> [Vertex,Vertex001,Vertex002,Vertex003,Vertex004]
FEATURE [Part::FeaturePython] PointArray  # Draft array (typed FeaturePython)
  Base = -> Cone
  Count = 5
  PointObject = -> Compound
FEATURE [App::Part] Part
  Group = -> [Vertex,Cone,Vertex002,Compound,Vertex003,Vertex004,Vertex001,PointArray]
  Origin = -> Origin001
FEATURE [App::Part] worldVOL
  Group = -> [GDMLBox_WorldBox,Part]
  Origin = -> Origin
